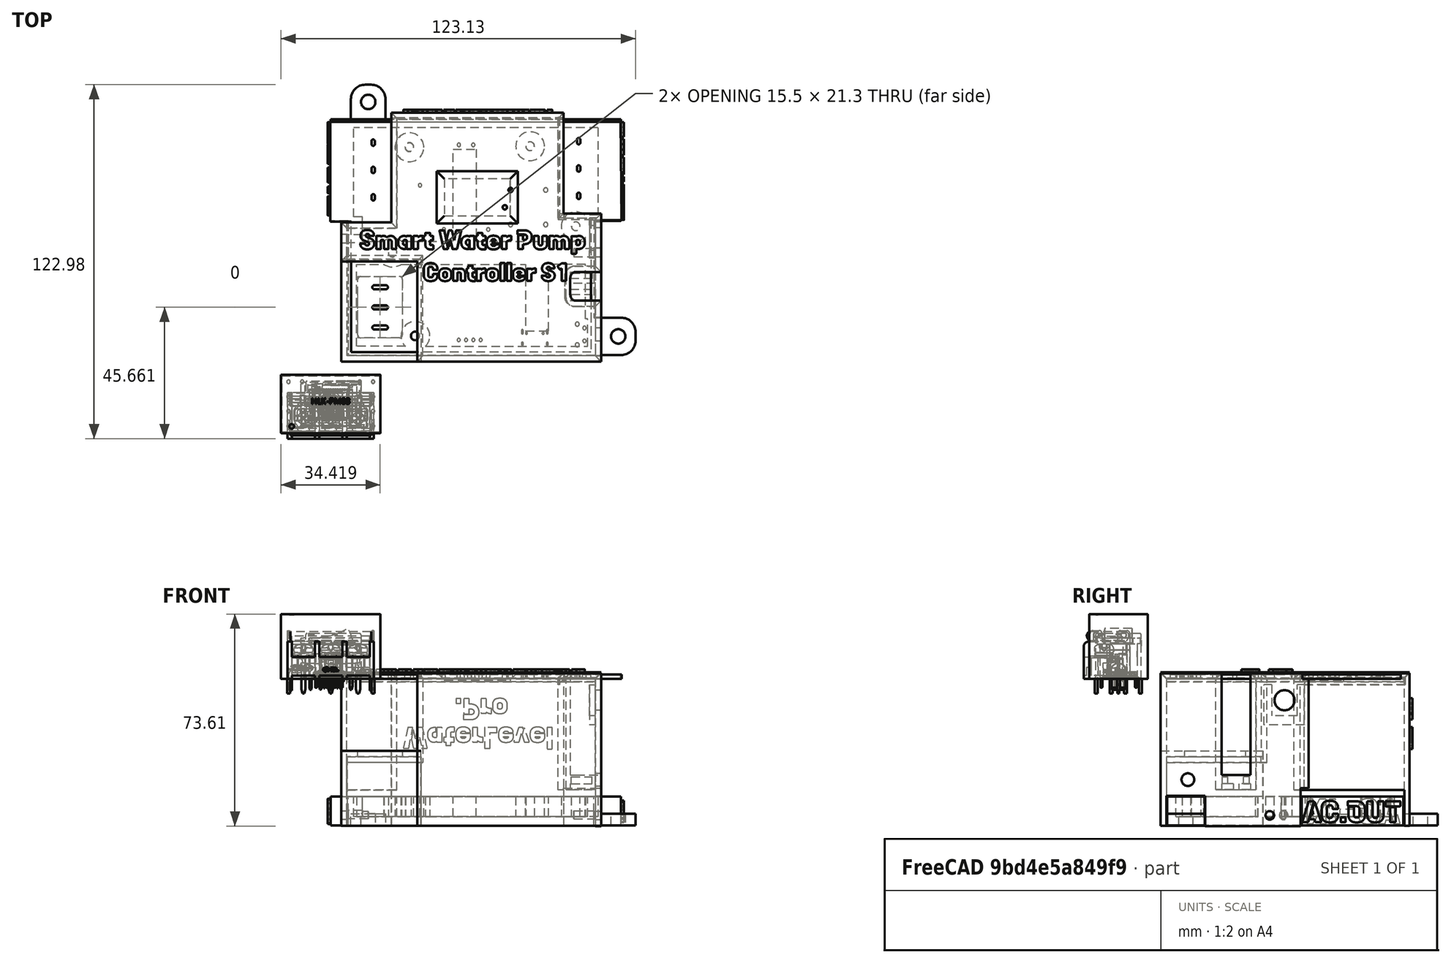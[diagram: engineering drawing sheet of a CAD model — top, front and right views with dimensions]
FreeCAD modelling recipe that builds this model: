
FCSTD DOCUMENT  (FreeCAD 0.21R33771 (Git))
Label: PumpControllerS1_caseV5
License: GPLv3
LicenseURL: https://en.wikipedia.org/wiki/All_rights_reserved
objects: Part::Feature×416, PartDesign::Pad×159, Sketcher::SketchObject×120, PartDesign::Pocket×106, App::Part×69, Part::Part2DObjectPython×20, PartDesign::Fillet×11, PartDesign::Draft×8, PartDesign::Chamfer×8, PartDesign::Body×7, PartDesign::Boolean×3, Part::Cut×1
note: 1151 computed .brp shape members not serialized (recipe doc carries the construction recipe); baked Part::Feature solids carry a one-line shape summary decoded from their .brp

FEATURE [Sketcher::SketchObject] Sketch
  FullyConstrained = true
  MapMode = 5
  Support = -> [XY_Plane049]
  sketch-geometry (8):
    g0: LineSegment StartX=0 StartY=63.64 StartZ=0 EndX=0 EndY=97.92 EndZ=0
    g1: LineSegment StartX=0 StartY=97.92 StartZ=0 EndX=100.82 EndY=97.92 EndZ=0
    g2: LineSegment StartX=100.82 StartY=97.92 StartZ=0 EndX=100.82 EndY=63.64 EndZ=0
    g3: LineSegment StartX=100.82 StartY=63.64 StartZ=0 EndX=90.46 EndY=63.64 EndZ=0
    g4: LineSegment StartX=90.46 StartY=63.64 StartZ=0 EndX=90.46 EndY=17.97 EndZ=0
    g5: LineSegment StartX=90.46 StartY=17.97 StartZ=0 EndX=6.99 EndY=17.97 EndZ=0
    g6: LineSegment StartX=6.99 StartY=17.97 StartZ=0 EndX=6.99 EndY=63.64 EndZ=0
    g7: LineSegment StartX=6.99 StartY=63.64 StartZ=0 EndX=0 EndY=63.64 EndZ=0
  constraints (24):
    c: PointOnObject(g0,g-2)
    c: Coincident(g0,g1)
    c: Horizontal(g1)
    c: Coincident(g1,g2)
    c: Vertical(g2)
    c: Coincident(g2,g3)
    c: Horizontal(g3)
    c: Coincident(g3,g4)
    c: Vertical(g4)
    c: Coincident(g4,g5)
    c: Horizontal(g5)
    c: Coincident(g5,g6)
    c: Vertical(g6)
    c: Coincident(g6,g7)
    c: Coincident(g7,g0)
    c: Horizontal(g7)
    c: DistanceX(g0,g1) = 100.82
    c: DistanceX(g5,g4) = 83.47
    c: DistanceX(g3,g2) = 10.36
    c: DistanceY(g2,g1) = 34.28
    c: DistanceY(g4,g3) = 45.67
    c: DistanceY(g-1,g5) = 17.97
    c: Vertical(g0)
    c: Equal(g0,g2)
FEATURE [PartDesign::Pad] Pad
  Direction = (0,0,1)
  Length = 3
  Length2 = 10
  Profile = -> Sketch
  ReferenceAxis = -> Sketch [N_Axis]
  Refine = true
  Type = 0
FEATURE [Sketcher::SketchObject] Sketch001
  FullyConstrained = true
  MapMode = 5
  Placement = pos=(0,0,3) rot=(0,0,1;0rad)
  Support = -> [Pad]
  sketch-geometry (10):
    g0: Circle CenterX=29.39 CenterY=23.62 CenterZ=0 NormalX=0 NormalY=0 NormalZ=1 AngleXU=0 Radius=5
    g1: Circle CenterX=21.48 CenterY=52.55 CenterZ=0 NormalX=0 NormalY=0 NormalZ=1 AngleXU=0 Radius=5
    g2: Circle CenterX=85.08 CenterY=61.73 CenterZ=0 NormalX=0 NormalY=0 NormalZ=1 AngleXU=0 Radius=5
    g3: Circle CenterX=69.27 CenterY=89.53 CenterZ=0 NormalX=0 NormalY=0 NormalZ=1 AngleXU=0 Radius=5
    g4: Circle CenterX=27.31 CenterY=89.16 CenterZ=0 NormalX=0 NormalY=0 NormalZ=1 AngleXU=0 Radius=5
    g5: Circle CenterX=29.39 CenterY=23.62 CenterZ=0 NormalX=0 NormalY=0 NormalZ=1 AngleXU=0 Radius=1.5
    g6: Circle CenterX=21.48 CenterY=52.55 CenterZ=0 NormalX=0 NormalY=0 NormalZ=1 AngleXU=0 Radius=1.5
    g7: Circle CenterX=27.31 CenterY=89.16 CenterZ=0 NormalX=0 NormalY=0 NormalZ=1 AngleXU=0 Radius=1.5
    g8: Circle CenterX=69.27 CenterY=89.53 CenterZ=0 NormalX=0 NormalY=0 NormalZ=1 AngleXU=0 Radius=1.5
    g9: Circle CenterX=85.08 CenterY=61.73 CenterZ=0 NormalX=0 NormalY=0 NormalZ=1 AngleXU=0 Radius=1.5
  constraints (25):
    c: Diameter(g4) = 10
    c: Diameter(g1) = 10
    c: Diameter(g0) = 10
    c: Diameter(g2) = 10
    c: Diameter(g3) = 10
    c: DistanceX(g4,g3) = 41.96
    c: DistanceX(g1,g4) = 5.83
    c: DistanceX(g3,g2) = 15.81
    c: DistanceX(g1,g0) = 7.91
    c: DistanceX(g-1,g0) = 29.39
    c: DistanceY(g4,g3) = 0.37
    c: DistanceY(g2,g3) = 27.8
    c: DistanceY(g1,g4) = 36.61
    c: DistanceY(g0,g1) = 28.93
    c: DistanceY(g-1,g0) = 23.62
    c: Coincident(g5,g0)
    c: Diameter(g5) = 3
    c: Coincident(g6,g1)
    c: Coincident(g7,g4)
    c: Coincident(g8,g3)
    c: Coincident(g9,g2)
    c: Diameter(g7) = 3
    c: Diameter(g8) = 3
    c: Diameter(g9) = 3
    c: Diameter(g6) = 3
FEATURE [PartDesign::Pad] Pad001
  BaseFeature = -> Pad
  Direction = (0,0,1)
  Length = 7
  Length2 = 10
  Profile = -> Sketch001
  ReferenceAxis = -> Sketch001 [N_Axis]
  Refine = true
  Type = 0
FEATURE [Sketcher::SketchObject] Sketch002
  ExternalGeometry = -> [Pad001]
  FullyConstrained = false
  MapMode = 5
  Placement = pos=(0,0,3) rot=(0,0,1;0rad)
  Support = -> [Pad001]
  sketch-geometry (21):
    g0: LineSegment StartX=90.46 StartY=56.5 StartZ=0 EndX=90.46 EndY=48.4293 EndZ=0
    g1: LineSegment StartX=7 StartY=48.5 StartZ=0 EndX=7 EndY=56.5 EndZ=0
    g2: Circle CenterX=21.48 CenterY=52.55 CenterZ=0 NormalX=0 NormalY=0 NormalZ=1 AngleXU=0 Radius=1.5
    g3: LineSegment StartX=42.46 StartY=56.5 StartZ=0 EndX=42.46 EndY=88.5 EndZ=0
    g4: LineSegment StartX=42.46 StartY=88.5 StartZ=0 EndX=50.46 EndY=88.5 EndZ=0
    g5: LineSegment StartX=50.46 StartY=88.5 StartZ=0 EndX=50.46 EndY=56.5 EndZ=0
    g6: LineSegment StartX=67.69 StartY=48.5 StartZ=0 EndX=67.69 EndY=25.4293 EndZ=0
    g7: LineSegment StartX=67.69 StartY=25.4293 StartZ=0 EndX=75.69 EndY=25.4293 EndZ=0
    g8: LineSegment StartX=75.69 StartY=25.4293 StartZ=0 EndX=75.69 EndY=48.4293 EndZ=0
    g9: LineSegment StartX=8 StartY=97.92 StartZ=0 EndX=0 EndY=97.92 EndZ=0
    g10: LineSegment StartX=0 StartY=97.92 StartZ=0 EndX=0 EndY=63.64 EndZ=0
    g11: LineSegment StartX=0 StartY=63.64 StartZ=0 EndX=8 EndY=63.64 EndZ=0
    g12: LineSegment StartX=8 StartY=63.64 StartZ=0 EndX=8 EndY=97.92 EndZ=0
    g13: LineSegment StartX=100.82 StartY=97.92 StartZ=0 EndX=92.82 EndY=97.92 EndZ=0
    g14: LineSegment StartX=92.82 StartY=97.92 StartZ=0 EndX=92.82 EndY=63.64 EndZ=0
    g15: LineSegment StartX=92.82 StartY=63.64 StartZ=0 EndX=100.82 EndY=63.64 EndZ=0
    g16: LineSegment StartX=100.82 StartY=63.64 StartZ=0 EndX=100.82 EndY=97.92 EndZ=0
    g17: LineSegment StartX=7 StartY=56.5 StartZ=0 EndX=42.46 EndY=56.5 EndZ=0
    g18: LineSegment StartX=7 StartY=48.5 StartZ=0 EndX=67.69 EndY=48.5 EndZ=0
    g19: LineSegment StartX=50.46 StartY=56.5 StartZ=0 EndX=90.46 EndY=56.5 EndZ=0
    g20: LineSegment StartX=90.46 StartY=48.4293 StartZ=0 EndX=75.69 EndY=48.4293 EndZ=0
  constraints (58):
    c: Vertical(g0)
    c: Vertical(g1)
    c: DistanceY(g1,g1) = 8
    c: DistanceY(g-1,g1) = 48.5
    c: Coincident(g2,g-3)
    c: Diameter(g2) = 3
    c: Coincident(g3,g4)
    c: Coincident(g4,g5)
    c: Horizontal(g4)
    c: Vertical(g3)
    c: Vertical(g5)
    c: Coincident(g6,g7)
    c: Coincident(g7,g8)
    c: Horizontal(g7)
    c: Vertical(g6)
    c: Vertical(g8)
    c: DistanceX(g4,g4) = 8
    c: DistanceX(g7,g7) = 8
    c: Coincident(g9,g10)
    c: Coincident(g10,g11)
    c: Coincident(g11,g12)
    c: Coincident(g12,g9)
    c: Horizontal(g9)
    c: Horizontal(g11)
    c: Vertical(g10)
    c: Vertical(g12)
    c: PointOnObject(g9,g-4)
    c: Coincident(g10,g-8)
    c: Coincident(g13,g14)
    c: Coincident(g14,g15)
    c: Coincident(g15,g16)
    c: Coincident(g16,g13)
    c: Horizontal(g13)
    c: Horizontal(g15)
    c: Vertical(g14)
    c: Vertical(g16)
    c: Coincident(g13,g-7)
    c: PointOnObject(g14,g-6)
    c: DistanceX(g13,g13) = 8
    c: DistanceX(g9,g9) = 8
    c: DistanceY(g8,g8) = 23
    c: DistanceY(g5,g5) = 32
    c: DistanceX(g5,g0) = 40
    c: DistanceX(g-1,g1) = 7
    c: DistanceX(g1,g0) = 83.46
    c: DistanceX(g8,g0) = 14.77
    c: Coincident(g1,g17)
    c: Coincident(g17,g3)
    c: Horizontal(g17)
    c: Coincident(g1,g18)
    c: Coincident(g18,g6)
    c: Horizontal(g18)
    c: Coincident(g5,g19)
    c: Coincident(g19,g0)
    c: Horizontal(g19)
    c: Coincident(g0,g20)
    c: Coincident(g20,g8)
    c: Horizontal(g20)
FEATURE [PartDesign::Pad] Pad002
  BaseFeature = -> Pad001
  Direction = (0,0,1)
  Length = 7
  Length2 = 10
  Profile = -> Sketch002
  ReferenceAxis = -> Sketch002 [N_Axis]
  Refine = true
  Type = 0
FEATURE [Sketcher::SketchObject] Sketch003
  ExternalGeometry = -> [Pad002]
  FullyConstrained = true
  MapMode = 5
  Placement = pos=(0,0,3) rot=(0,0,1;0rad)
  Support = -> [Pad002]
  sketch-geometry (20):
    g0: LineSegment StartX=5 StartY=97.92 StartZ=0 EndX=94 EndY=97.92 EndZ=0
    g1: LineSegment StartX=94 StartY=97.92 StartZ=0 EndX=94 EndY=95.92 EndZ=0
    g2: LineSegment StartX=94 StartY=95.92 StartZ=0 EndX=5 EndY=95.92 EndZ=0
    g3: LineSegment StartX=5 StartY=95.92 StartZ=0 EndX=5 EndY=97.92 EndZ=0
    g4: LineSegment StartX=6.99 StartY=17.97 StartZ=0 EndX=8.99 EndY=17.97 EndZ=0
    g5: LineSegment StartX=8.99 StartY=17.97 StartZ=0 EndX=8.99 EndY=64.97 EndZ=0
    g6: LineSegment StartX=8.99 StartY=64.97 StartZ=0 EndX=6.99 EndY=64.97 EndZ=0
    g7: LineSegment StartX=6.99 StartY=64.97 StartZ=0 EndX=6.99 EndY=17.97 EndZ=0
    g8: LineSegment StartX=90.46 StartY=29.6 StartZ=0 EndX=88.46 EndY=29.6 EndZ=0
    g9: LineSegment StartX=88.46 StartY=29.6 StartZ=0 EndX=88.46 EndY=64.6 EndZ=0
    g10: LineSegment StartX=88.46 StartY=64.6 StartZ=0 EndX=90.46 EndY=64.6 EndZ=0
    g11: LineSegment StartX=90.46 StartY=64.6 StartZ=0 EndX=90.46 EndY=29.6 EndZ=0
    g12: LineSegment StartX=90.46 StartY=17.97 StartZ=0 EndX=89.21 EndY=17.97 EndZ=0
    g13: LineSegment StartX=89.21 StartY=17.97 StartZ=0 EndX=89.21 EndY=26.97 EndZ=0
    g14: LineSegment StartX=89.21 StartY=26.97 StartZ=0 EndX=90.46 EndY=26.97 EndZ=0
    g15: LineSegment StartX=90.46 StartY=26.97 StartZ=0 EndX=90.46 EndY=17.97 EndZ=0
    g16: LineSegment StartX=35.93 StartY=17.97 StartZ=0 EndX=75.93 EndY=17.97 EndZ=0
    g17: LineSegment StartX=75.93 StartY=17.97 StartZ=0 EndX=75.93 EndY=19.97 EndZ=0
    g18: LineSegment StartX=75.93 StartY=19.97 StartZ=0 EndX=35.93 EndY=19.97 EndZ=0
    g19: LineSegment StartX=35.93 StartY=19.97 StartZ=0 EndX=35.93 EndY=17.97 EndZ=0
  constraints (58):
    c: Coincident(g0,g1)
    c: Coincident(g1,g2)
    c: Coincident(g2,g3)
    c: Coincident(g3,g0)
    c: Horizontal(g0)
    c: Horizontal(g2)
    c: Vertical(g1)
    c: Vertical(g3)
    c: PointOnObject(g0,g-3)
    c: DistanceY(g1,g1) = 2
    c: DistanceX(g-1,g0) = 5
    c: DistanceX(g0,g0) = 89
    c: Coincident(g4,g5)
    c: Coincident(g5,g6)
    c: Coincident(g6,g7)
    c: Coincident(g7,g4)
    c: Horizontal(g4)
    c: Horizontal(g6)
    c: Vertical(g5)
    c: Vertical(g7)
    c: Coincident(g4,g-7)
    c: DistanceY(g5,g5) = 47
    c: DistanceX(g6,g5) = 2
    c: Coincident(g8,g9)
    c: Coincident(g9,g10)
    c: Coincident(g10,g11)
    c: Coincident(g11,g8)
    c: Horizontal(g8)
    c: Horizontal(g10)
    c: Vertical(g9)
    c: Vertical(g11)
    c: PointOnObject(g8,g-8)
    c: DistanceX(g9,g10) = 2
    c: DistanceY(g9,g9) = 35
    c: DistanceY(g-8,g8) = 11.63
    c: Coincident(g12,g13)
    c: Coincident(g13,g14)
    c: Coincident(g14,g15)
    c: Coincident(g15,g12)
    c: Horizontal(g12)
    c: Horizontal(g14)
    c: Vertical(g13)
    c: Vertical(g15)
    c: Coincident(g12,g-8)
    c: DistanceX(g14,g14) = 1.25
    c: DistanceY(g13,g13) = 9
    c: Coincident(g16,g17)
    c: Coincident(g17,g18)
    c: Coincident(g18,g19)
    c: Coincident(g19,g16)
    c: Horizontal(g16)
    c: Horizontal(g18)
    c: Vertical(g17)
    c: Vertical(g19)
    c: PointOnObject(g16,g-7)
    c: DistanceY(g17,g17) = 2
    c: DistanceX(g18,g18) = 40
    c: DistanceX(g-1,g16) = 35.93
FEATURE [PartDesign::Pad] Pad003
  BaseFeature = -> Pad002
  Direction = (0,0,1)
  Length = 7
  Length2 = 10
  Profile = -> Sketch003
  ReferenceAxis = -> Sketch003 [N_Axis]
  Refine = true
  Type = 0
FEATURE [PartDesign::Pad] Pad004
  BaseFeature = -> Pad003
  Direction = (0,1,0)
  Length = 4
  Length2 = 10
  Profile = -> Pad003 [Face33]
  Refine = true
  Type = 0
FEATURE [PartDesign::Pad] Pad005
  BaseFeature = -> Pad004
  Direction = (1,0,0)
  Length = 14
  Length2 = 10
  Profile = -> Pad004 [Face13]
  Refine = true
  Type = 0
FEATURE [PartDesign::Pad] Pad006
  BaseFeature = -> Pad005
  Direction = (-1,0,0)
  Length = 28
  Length2 = 10
  Profile = -> Pad005 [Face36]
  Refine = true
  Type = 0
FEATURE [Sketcher::SketchObject] Sketch004
  ExternalGeometry = -> [Pad006]
  FullyConstrained = true
  MapMode = 5
  Placement = pos=(92.82,0,0) rot=(0.57735,-0.57735,-0.57735;2.0944rad)
  Support = -> [Pad006]
  sketch-geometry (4):
    g0: LineSegment StartX=-63.64 StartY=3 StartZ=0 EndX=-65.64 EndY=3 EndZ=0
    g1: LineSegment StartX=-65.64 StartY=3 StartZ=0 EndX=-65.64 EndY=10 EndZ=0
    g2: LineSegment StartX=-65.64 StartY=10 StartZ=0 EndX=-63.64 EndY=10 EndZ=0
    g3: LineSegment StartX=-63.64 StartY=10 StartZ=0 EndX=-63.64 EndY=3 EndZ=0
  constraints (11):
    c: Coincident(g0,g1)
    c: Coincident(g1,g2)
    c: Coincident(g2,g3)
    c: Coincident(g3,g0)
    c: Horizontal(g0)
    c: Horizontal(g2)
    c: Vertical(g1)
    c: Vertical(g3)
    c: Coincident(g0,g-5)
    c: PointOnObject(g1,g-4)
    c: DistanceX(g1,g2) = 2
FEATURE [PartDesign::Pad] Pad007
  BaseFeature = -> Pad006
  Direction = (-1,0,0)
  Length = 10
  Length2 = 10
  Profile = -> Sketch004
  ReferenceAxis = -> Sketch004 [N_Axis]
  Refine = true
  Type = 0
FEATURE [Sketcher::SketchObject] Sketch005
  ExternalGeometry = -> [Pad007]
  FullyConstrained = true
  MapMode = 5
  Placement = pos=(90.46,0,0) rot=(0.57735,0.57735,0.57735;2.0944rad)
  Support = -> [Pad007]
  sketch-geometry (4):
    g0: LineSegment StartX=17.97 StartY=10 StartZ=0 EndX=29.97 EndY=10 EndZ=0
    g1: LineSegment StartX=29.97 StartY=10 StartZ=0 EndX=29.97 EndY=0 EndZ=0
    g2: LineSegment StartX=29.97 StartY=0 StartZ=0 EndX=17.97 EndY=0 EndZ=0
    g3: LineSegment StartX=17.97 StartY=0 StartZ=0 EndX=17.97 EndY=10 EndZ=0
  constraints (11):
    c: Coincident(g0,g1)
    c: Coincident(g1,g2)
    c: Coincident(g2,g3)
    c: Coincident(g3,g0)
    c: Horizontal(g0)
    c: Horizontal(g2)
    c: Vertical(g1)
    c: Vertical(g3)
    c: Coincident(g0,g-4)
    c: PointOnObject(g1,g-5)
    c: DistanceX(g0,g0) = 12
FEATURE [PartDesign::Pad] Pad008
  BaseFeature = -> Pad007
  Direction = (1,0,0)
  Length = 1.5
  Length2 = 10
  Profile = -> Sketch005
  ReferenceAxis = -> Sketch005 [N_Axis]
  Refine = true
  Type = 0
FEATURE [Sketcher::SketchObject] Sketch006
  ExternalGeometry = -> [Pad008]
  FullyConstrained = true
  MapMode = 5
  Placement = pos=(0,0,10) rot=(0,0,1;0rad)
  Support = -> [Pad008]
  sketch-geometry (4):
    g0: LineSegment StartX=90.46 StartY=29.97 StartZ=0 EndX=91.96 EndY=29.97 EndZ=0
    g1: LineSegment StartX=91.96 StartY=29.97 StartZ=0 EndX=91.96 EndY=17.97 EndZ=0
    g2: LineSegment StartX=91.96 StartY=17.97 StartZ=0 EndX=90.46 EndY=17.97 EndZ=0
    g3: LineSegment StartX=90.46 StartY=17.97 StartZ=0 EndX=90.46 EndY=29.97 EndZ=0
  constraints (10):
    c: Coincident(g0,g1)
    c: Coincident(g1,g2)
    c: Coincident(g2,g3)
    c: Coincident(g3,g0)
    c: Horizontal(g0)
    c: Horizontal(g2)
    c: Vertical(g1)
    c: Vertical(g3)
    c: Coincident(g0,g-3)
    c: Coincident(g1,g-5)
FEATURE [PartDesign::Pad] Pad009
  BaseFeature = -> Pad008
  Direction = (0,0,1)
  Length = 12
  Length2 = 10
  Profile = -> Sketch006
  ReferenceAxis = -> Sketch006 [N_Axis]
  Refine = true
  Type = 0
FEATURE [Sketcher::SketchObject] Sketch007
  FullyConstrained = false
  MapMode = 5
  Placement = pos=(91.96,0,0) rot=(0.57735,0.57735,0.57735;2.0944rad)
  Support = -> [Pad009]
  sketch-geometry (1):
    g0: Circle CenterX=24.1415 CenterY=15.9066 CenterZ=0 NormalX=0 NormalY=0 NormalZ=1 AngleXU=0 Radius=2.2
  constraints (1):
    c: Diameter(g0) = 4.4
FEATURE [PartDesign::Pocket] Pocket
  BaseFeature = -> Pad009
  Direction = (-1,0,0)
  Length = 5
  Length2 = 5
  Profile = -> Sketch007
  ReferenceAxis = -> Sketch007 [N_Axis]
  Refine = true
  Type = 0
FEATURE [PartDesign::Pad] Pad010
  BaseFeature = -> Pocket
  Direction = (0,1,0)
  Length = 1
  Length2 = 10
  Profile = -> Pocket [Face4]
  Refine = true
  Type = 0
FEATURE [PartDesign::Pad] Pad011
  BaseFeature = -> Pad010
  Direction = (0,-1,0)
  Length = 1
  Length2 = 10
  Profile = -> Pad010 [Face5]
  Refine = true
  Type = 0
FEATURE [PartDesign::Pad] Pad012
  BaseFeature = -> Pad011
  Direction = (-1,0,0)
  Length = 1
  Length2 = 10
  Profile = -> Pad011 [Face59]
  Refine = true
  Type = 0
FEATURE [PartDesign::Pad] Pad013
  BaseFeature = -> Pad012
  Direction = (1,0,0)
  Length = 1
  Length2 = 10
  Profile = -> Pad012 [Face5]
  Refine = true
  Type = 0
FEATURE [Sketcher::SketchObject] Sketch008
  FullyConstrained = true
  MapMode = 5
  Support = -> [XY_Plane050]
  sketch-geometry (10):
    g0: LineSegment StartX=21 StartY=100.55 StartZ=0 EndX=21 EndY=64.55 EndZ=0
    g1: LineSegment StartX=21 StartY=64.55 StartZ=0 EndX=4.2 EndY=64.55 EndZ=0
    g2: LineSegment StartX=93.5 StartY=15.2 StartZ=0 EndX=93.5 EndY=65.2 EndZ=0
    g3: LineSegment StartX=93.5 StartY=65.2 StartZ=0 EndX=80.9 EndY=65.2 EndZ=0
    g4: LineSegment StartX=80.9 StartY=65.2 StartZ=0 EndX=80.9 EndY=100.55 EndZ=0
    g5: LineSegment StartX=80.9 StartY=100.55 StartZ=0 EndX=21 EndY=100.55 EndZ=0
    g6: LineSegment StartX=93.5 StartY=15.2 StartZ=0 EndX=30 EndY=15.2 EndZ=0
    g7: LineSegment StartX=30 StartY=15.2 StartZ=0 EndX=30 EndY=49.55 EndZ=0
    g8: LineSegment StartX=30 StartY=49.55 StartZ=0 EndX=4.2 EndY=49.55 EndZ=0
    g9: LineSegment StartX=4.2 StartY=49.55 StartZ=0 EndX=4.2 EndY=64.55 EndZ=0
  constraints (30):
    c: Vertical(g0)
    c: Coincident(g0,g1)
    c: Horizontal(g1)
    c: Vertical(g2)
    c: Coincident(g2,g3)
    c: Coincident(g3,g4)
    c: Vertical(g4)
    c: Coincident(g4,g5)
    c: Coincident(g5,g0)
    c: Horizontal(g5)
    c: Horizontal(g3)
    c: Coincident(g2,g6)
    c: Horizontal(g6)
    c: Coincident(g6,g7)
    c: Vertical(g7)
    c: Coincident(g7,g8)
    c: Horizontal(g8)
    c: Coincident(g8,g9)
    c: Coincident(g9,g1)
    c: Vertical(g9)
    c: DistanceY(g-1,g6) = 15.2
    c: DistanceX(g-1,g6) = 30
    c: DistanceX(g8,g7) = 25.8
    c: DistanceX(g6,g6) = 63.5
    c: DistanceY(g2,g2) = 50
    c: DistanceY(g7,g7) = 34.35
    c: DistanceY(g9,g9) = 15
    c: DistanceY(g0,g0) = 36
    c: DistanceX(g5,g5) = 59.9
    c: DistanceX(g3,g3) = 12.6
FEATURE [PartDesign::Pad] Pad014
  Direction = (0,0,1)
  Length = 2
  Length2 = 10
  Profile = -> Sketch008
  ReferenceAxis = -> Sketch008 [N_Axis]
  Refine = true
  Type = 0
FEATURE [Sketcher::SketchObject] Sketch009
  FullyConstrained = false
  MapMode = 5
  Support = -> [XY_Plane051]
  sketch-geometry (4):
    g0: LineSegment StartX=4.34912 StartY=50.7797 StartZ=0 EndX=32.5138 EndY=50.7797 EndZ=0
    g1: LineSegment StartX=32.5138 StartY=50.7797 StartZ=0 EndX=32.5138 EndY=14.7356 EndZ=0
    g2: LineSegment StartX=32.5138 StartY=14.7356 StartZ=0 EndX=4.34912 EndY=14.7356 EndZ=0
    g3: LineSegment StartX=4.34912 StartY=14.7356 StartZ=0 EndX=4.34912 EndY=50.7797 EndZ=0
  constraints (8):
    c: Coincident(g0,g1)
    c: Coincident(g1,g2)
    c: Coincident(g2,g3)
    c: Coincident(g3,g0)
    c: Horizontal(g0)
    c: Horizontal(g2)
    c: Vertical(g1)
    c: Vertical(g3)
FEATURE [PartDesign::Pad] Pad015
  Direction = (0,0,1)
  Length = 2
  Length2 = 10
  Profile = -> Sketch009
  ReferenceAxis = -> Sketch009 [N_Axis]
  Refine = true
  Type = 0
FEATURE [Sketcher::SketchObject] Sketch010
  ExternalGeometry = -> [Pad015]
  FullyConstrained = true
  MapMode = 5
  Placement = pos=(0,0,0) rot=(1,0,0;3.14159rad)
  Support = -> [Pad015]
  sketch-geometry (6):
    g0: LineSegment StartX=4.34912 StartY=-50.7797 StartZ=0 EndX=4.34912 EndY=-14.7356 EndZ=0
    g1: LineSegment StartX=4.34912 StartY=-14.7356 StartZ=0 EndX=32.5138 EndY=-14.7356 EndZ=0
    g2: LineSegment StartX=32.5138 StartY=-14.7356 StartZ=0 EndX=32.5138 EndY=-16.2356 EndZ=0
    g3: LineSegment StartX=32.5138 StartY=-16.2356 StartZ=0 EndX=5.84912 EndY=-16.2356 EndZ=0
    g4: LineSegment StartX=5.84912 StartY=-16.2356 StartZ=0 EndX=5.84912 EndY=-50.7797 EndZ=0
    g5: LineSegment StartX=5.84912 StartY=-50.7797 StartZ=0 EndX=4.34912 EndY=-50.7797 EndZ=0
  constraints (15):
    c: Coincident(g-3,g0)
    c: Coincident(g0,g-4)
    c: Coincident(g0,g1)
    c: Coincident(g1,g-4)
    c: Coincident(g1,g2)
    c: Vertical(g2)
    c: Coincident(g2,g3)
    c: Horizontal(g3)
    c: Coincident(g3,g4)
    c: Vertical(g4)
    c: Coincident(g4,g5)
    c: Coincident(g5,g0)
    c: DistanceY(g2,g1) = 1.5
    c: DistanceX(g0,g4) = 1.5
    c: PointOnObject(g4,g-5)
FEATURE [PartDesign::Pad] Pad016
  BaseFeature = -> Pad015
  Direction = (0,0,-1)
  Length = 22
  Length2 = 10
  Profile = -> Sketch010
  ReferenceAxis = -> Sketch010 [N_Axis]
  Refine = true
  Type = 0
FEATURE [Sketcher::SketchObject] Sketch011
  ExternalGeometry = -> [Pad016]
  FullyConstrained = true
  MapMode = 5
  Placement = pos=(0,0,2) rot=(0,0,1;0rad)
  Support = -> [Pad016]
  sketch-geometry (4):
    g0: LineSegment StartX=9.59912 StartY=43.7856 StartZ=0 EndX=25.0991 EndY=43.7856 EndZ=0
    g1: LineSegment StartX=25.0991 StartY=43.7856 StartZ=0 EndX=25.0991 EndY=22.4856 EndZ=0
    g2: LineSegment StartX=25.0991 StartY=22.4856 StartZ=0 EndX=9.59912 EndY=22.4856 EndZ=0
    g3: LineSegment StartX=9.59912 StartY=22.4856 StartZ=0 EndX=9.59912 EndY=43.7856 EndZ=0
  constraints (12):
    c: Coincident(g0,g1)
    c: Coincident(g1,g2)
    c: Coincident(g2,g3)
    c: Coincident(g3,g0)
    c: Horizontal(g0)
    c: Horizontal(g2)
    c: Vertical(g1)
    c: Vertical(g3)
    c: DistanceX(g0,g0) = 15.5
    c: DistanceY(g1,g0) = 21.3
    c: DistanceY(g-4,g2) = 7.75
    c: DistanceX(g-4,g2) = 5.25
FEATURE [PartDesign::Pocket] Pocket001
  BaseFeature = -> Pad016
  Direction = (0,0,-1)
  Length = 5
  Length2 = 5
  Profile = -> Sketch011
  ReferenceAxis = -> Sketch011 [N_Axis]
  Refine = true
  Type = 0
FEATURE [Sketcher::SketchObject] Sketch012
  ExternalGeometry = -> [Pad014]
  FullyConstrained = true
  MapMode = 5
  Placement = pos=(0,0,0) rot=(1,0,0;3.14159rad)
  Support = -> [Pad014]
  sketch-geometry (8):
    g0: LineSegment StartX=30 StartY=-15.2 StartZ=0 EndX=93.5 EndY=-15.2 EndZ=0
    g1: LineSegment StartX=93.5 StartY=-15.2 StartZ=0 EndX=93.5 EndY=-16.7 EndZ=0
    g2: LineSegment StartX=93.5 StartY=-16.7 StartZ=0 EndX=30 EndY=-16.7 EndZ=0
    g3: LineSegment StartX=30 StartY=-16.7 StartZ=0 EndX=30 EndY=-15.2 EndZ=0
    g4: LineSegment StartX=21 StartY=-100.55 StartZ=0 EndX=80.9 EndY=-100.55 EndZ=0
    g5: LineSegment StartX=80.9 StartY=-100.55 StartZ=0 EndX=80.9 EndY=-99.35 EndZ=0
    g6: LineSegment StartX=80.9 StartY=-99.35 StartZ=0 EndX=21 EndY=-99.35 EndZ=0
    g7: LineSegment StartX=21 StartY=-99.35 StartZ=0 EndX=21 EndY=-100.55 EndZ=0
  constraints (22):
    c: Coincident(g0,g1)
    c: Coincident(g1,g2)
    c: Coincident(g2,g3)
    c: Coincident(g3,g0)
    c: Horizontal(g0)
    c: Horizontal(g2)
    c: Vertical(g1)
    c: Vertical(g3)
    c: Coincident(g0,g-4)
    c: PointOnObject(g1,g-5)
    c: DistanceY(g1,g1) = 1.5
    c: Coincident(g4,g5)
    c: Coincident(g5,g6)
    c: Coincident(g6,g7)
    c: Coincident(g7,g4)
    c: Horizontal(g4)
    c: Horizontal(g6)
    c: Vertical(g5)
    c: Vertical(g7)
    c: Coincident(g4,g-10)
    c: DistanceY(g5,g5) = 1.2
    c: PointOnObject(g5,g-11)
FEATURE [PartDesign::Pad] Pad017
  BaseFeature = -> Pad014
  Direction = (0,0,-1)
  Length = 51
  Length2 = 10
  Profile = -> Sketch012
  ReferenceAxis = -> Sketch012 [N_Axis]
  Refine = true
  Type = 0
FEATURE [PartDesign::Pad] Pad018
  BaseFeature = -> Pad017
  Direction = (0,1,0)
  Length = 0.6
  Length2 = 10
  Profile = -> Pad017 [Face16]
  Refine = true
  Type = 0
FEATURE [PartDesign::Pad] Pad019
  BaseFeature = -> Pad018
  Direction = (0,-1,0)
  Length = 0.5
  Length2 = 10
  Profile = -> Pad018 [Face4]
  Refine = true
  Type = 0
FEATURE [PartDesign::Pad] Pad020
  BaseFeature = -> Pocket001
  Direction = (0,-1,0)
  Length = 0.5
  Length2 = 10
  Profile = -> Pocket001 [Face5]
  Refine = true
  Type = 0
FEATURE [PartDesign::Pad] Pad021
  BaseFeature = -> Pad020
  Direction = (-1,0,0)
  Length = 0.5
  Length2 = 10
  Profile = -> Pad020 [Face11]
  Refine = true
  Type = 0
FEATURE [Sketcher::SketchObject] Sketch013
  ExternalGeometry = -> [Pad019]
  FullyConstrained = true
  MapMode = 5
  Placement = pos=(0,0,0) rot=(1,0,0;3.14159rad)
  Support = -> [Pad019]
  sketch-geometry (6):
    g0: LineSegment StartX=30 StartY=-16.7 StartZ=0 EndX=32 EndY=-16.7 EndZ=0
    g1: LineSegment StartX=32 StartY=-16.7 StartZ=0 EndX=32 EndY=-51.55 EndZ=0
    g2: LineSegment StartX=32 StartY=-51.55 StartZ=0 EndX=4.2 EndY=-51.55 EndZ=0
    g3: LineSegment StartX=4.2 StartY=-51.55 StartZ=0 EndX=4.2 EndY=-49.55 EndZ=0
    g4: LineSegment StartX=4.2 StartY=-49.55 StartZ=0 EndX=30 EndY=-49.55 EndZ=0
    g5: LineSegment StartX=30 StartY=-49.55 StartZ=0 EndX=30 EndY=-16.7 EndZ=0
  constraints (15):
    c: Coincident(g-4,g0)
    c: PointOnObject(g0,g-4)
    c: Coincident(g0,g1)
    c: Vertical(g1)
    c: Coincident(g1,g2)
    c: Horizontal(g2)
    c: Coincident(g2,g3)
    c: Coincident(g3,g-5)
    c: Coincident(g3,g4)
    c: Coincident(g4,g-5)
    c: Coincident(g4,g5)
    c: Coincident(g5,g0)
    c: Vertical(g3)
    c: DistanceY(g3,g3) = 2
    c: DistanceX(g0,g0) = 2
FEATURE [PartDesign::Pad] Pad022
  BaseFeature = -> Pad019
  Direction = (0,0,-1)
  Length = 29
  Length2 = 10
  Profile = -> Sketch013
  ReferenceAxis = -> Sketch013 [N_Axis]
  Refine = true
  Type = 0
FEATURE [Sketcher::SketchObject] Sketch014
  ExternalGeometry = -> [Pad022]
  FullyConstrained = true
  MapMode = 5
  Placement = pos=(0,0,0) rot=(1,0,0;3.14159rad)
  Support = -> [Pad022]
  sketch-geometry (4):
    g0: LineSegment StartX=4.2 StartY=-64.55 StartZ=0 EndX=6.2 EndY=-64.55 EndZ=0
    g1: LineSegment StartX=6.2 StartY=-64.55 StartZ=0 EndX=6.2 EndY=-51.55 EndZ=0
    g2: LineSegment StartX=6.2 StartY=-51.55 StartZ=0 EndX=4.2 EndY=-51.55 EndZ=0
    g3: LineSegment StartX=4.2 StartY=-51.55 StartZ=0 EndX=4.2 EndY=-64.55 EndZ=0
  constraints (11):
    c: Coincident(g0,g1)
    c: Coincident(g1,g2)
    c: Coincident(g2,g3)
    c: Coincident(g3,g0)
    c: Horizontal(g0)
    c: Horizontal(g2)
    c: Vertical(g1)
    c: Vertical(g3)
    c: Coincident(g0,g-4)
    c: PointOnObject(g1,g-5)
    c: DistanceX(g2,g2) = 2
FEATURE [PartDesign::Pad] Pad023
  BaseFeature = -> Pad022
  Direction = (0,0,-1)
  Length = 51
  Length2 = 10
  Profile = -> Sketch014
  ReferenceAxis = -> Sketch014 [N_Axis]
  Refine = true
  Type = 0
FEATURE [PartDesign::Pocket] Pocket002
  BaseFeature = -> Pad023
  Direction = (0,-1,0)
  Length = 1.5
  Length2 = 5
  Profile = -> Pad023 [Face21]
  Refine = true
  Type = 0
FEATURE [PartDesign::Pad] Pad024
  BaseFeature = -> Pocket002
  Direction = (-1,0,0)
  Length = 0.55
  Length2 = 10
  Profile = -> Pocket002 [Face18]
  Refine = true
  Type = 0
FEATURE [PartDesign::Pad] Pad025
  BaseFeature = -> Pad024
  Direction = (0,-1,0)
  Length = 1
  Length2 = 10
  Profile = -> Pad024 [Face19]
  Refine = true
  Type = 0
FEATURE [Sketcher::SketchObject] Sketch015
  ExternalGeometry = -> [Pad025]
  FullyConstrained = true
  MapMode = 5
  Placement = pos=(0,0,0) rot=(1,0,0;3.14159rad)
  Support = -> [Pad025]
  sketch-geometry (6):
    g0: LineSegment StartX=6.2 StartY=-63.05 StartZ=0 EndX=21 EndY=-63.05 EndZ=0
    g1: LineSegment StartX=21 StartY=-63.05 StartZ=0 EndX=21 EndY=-99.35 EndZ=0
    g2: LineSegment StartX=21 StartY=-99.35 StartZ=0 EndX=23 EndY=-99.35 EndZ=0
    g3: LineSegment StartX=23 StartY=-99.35 StartZ=0 EndX=23 EndY=-61.05 EndZ=0
    g4: LineSegment StartX=23 StartY=-61.05 StartZ=0 EndX=6.2 EndY=-61.05 EndZ=0
    g5: LineSegment StartX=6.2 StartY=-61.05 StartZ=0 EndX=6.2 EndY=-63.05 EndZ=0
  constraints (15):
    c: Coincident(g-4,g0)
    c: Coincident(g0,g-4)
    c: Coincident(g0,g1)
    c: Coincident(g1,g-3)
    c: Coincident(g1,g2)
    c: Horizontal(g2)
    c: Coincident(g2,g3)
    c: Vertical(g3)
    c: Coincident(g3,g4)
    c: Horizontal(g4)
    c: Coincident(g4,g5)
    c: Coincident(g5,g0)
    c: Vertical(g5)
    c: DistanceX(g2,g2) = 2
    c: DistanceY(g5,g5) = 2
FEATURE [PartDesign::Pad] Pad026
  BaseFeature = -> Pad025
  Direction = (0,0,-1)
  Length = 38.6
  Length2 = 10
  Profile = -> Sketch015
  ReferenceAxis = -> Sketch015 [N_Axis]
  Refine = true
  Type = 0
FEATURE [Sketcher::SketchObject] Sketch016
  ExternalGeometry = -> [Pad026]
  FullyConstrained = true
  MapMode = 5
  Placement = pos=(0,0,0) rot=(1,0,0;3.14159rad)
  Support = -> [Pad026]
  sketch-geometry (4):
    g0: LineSegment StartX=93.5 StartY=-65.2 StartZ=0 EndX=91.5 EndY=-65.2 EndZ=0
    g1: LineSegment StartX=91.5 StartY=-65.2 StartZ=0 EndX=91.5 EndY=-16.7 EndZ=0
    g2: LineSegment StartX=91.5 StartY=-16.7 StartZ=0 EndX=93.5 EndY=-16.7 EndZ=0
    g3: LineSegment StartX=93.5 StartY=-16.7 StartZ=0 EndX=93.5 EndY=-65.2 EndZ=0
  constraints (11):
    c: Coincident(g0,g1)
    c: Coincident(g1,g2)
    c: Coincident(g2,g3)
    c: Coincident(g3,g0)
    c: Horizontal(g0)
    c: Horizontal(g2)
    c: Vertical(g1)
    c: Vertical(g3)
    c: Coincident(g0,g-5)
    c: PointOnObject(g1,g-4)
    c: DistanceX(g0,g0) = 2
FEATURE [PartDesign::Pad] Pad027
  BaseFeature = -> Pad026
  Direction = (0,0,-1)
  Length = 28.7
  Length2 = 10
  Profile = -> Sketch016
  ReferenceAxis = -> Sketch016 [N_Axis]
  Refine = true
  Type = 0
FEATURE [Sketcher::SketchObject] Sketch017
  ExternalGeometry = -> [Pad027]
  FullyConstrained = true
  MapMode = 5
  Placement = pos=(0,0,-28.7) rot=(1,0,0;3.14159rad)
  Support = -> [Pad027]
  sketch-geometry (4):
    g0: LineSegment StartX=91.5 StartY=-65.2 StartZ=0 EndX=93.5 EndY=-65.2 EndZ=0
    g1: LineSegment StartX=93.5 StartY=-65.2 StartZ=0 EndX=93.5 EndY=-30.4 EndZ=0
    g2: LineSegment StartX=93.5 StartY=-30.4 StartZ=0 EndX=91.5 EndY=-30.4 EndZ=0
    g3: LineSegment StartX=91.5 StartY=-30.4 StartZ=0 EndX=91.5 EndY=-65.2 EndZ=0
  constraints (11):
    c: Coincident(g0,g1)
    c: Coincident(g1,g2)
    c: Coincident(g2,g3)
    c: Coincident(g3,g0)
    c: Horizontal(g0)
    c: Horizontal(g2)
    c: Vertical(g1)
    c: Vertical(g3)
    c: Coincident(g0,g-5)
    c: PointOnObject(g1,g-3)
    c: DistanceY(g1,g1) = 34.8
FEATURE [PartDesign::Pad] Pad028
  BaseFeature = -> Pad027
  Direction = (0,0,-1)
  Length = 22.4
  Length2 = 10
  Profile = -> Sketch017
  ReferenceAxis = -> Sketch017 [N_Axis]
  Refine = true
  Type = 0
FEATURE [PartDesign::Pocket] Pocket003
  BaseFeature = -> Pad028
  Direction = (0,-1,0)
  Length = 1.9
  Length2 = 5
  Profile = -> Pad028 [Face27]
  Refine = true
  Type = 0
FEATURE [Sketcher::SketchObject] Sketch018
  ExternalGeometry = -> [Pocket003]
  FullyConstrained = true
  MapMode = 5
  Placement = pos=(0,0,0) rot=(1,0,0;3.14159rad)
  Support = -> [Pocket003]
  sketch-geometry (4):
    g0: LineSegment StartX=80.9 StartY=-63.3 StartZ=0 EndX=78.9 EndY=-63.3 EndZ=0
    g1: LineSegment StartX=78.9 StartY=-63.3 StartZ=0 EndX=78.9 EndY=-99.35 EndZ=0
    g2: LineSegment StartX=78.9 StartY=-99.35 StartZ=0 EndX=80.9 EndY=-99.35 EndZ=0
    g3: LineSegment StartX=80.9 StartY=-99.35 StartZ=0 EndX=80.9 EndY=-63.3 EndZ=0
  constraints (11):
    c: Coincident(g0,g1)
    c: Coincident(g1,g2)
    c: Coincident(g2,g3)
    c: Coincident(g3,g0)
    c: Horizontal(g0)
    c: Horizontal(g2)
    c: Vertical(g1)
    c: Vertical(g3)
    c: Coincident(g0,g-3)
    c: PointOnObject(g1,g-4)
    c: DistanceX(g0,g0) = 2
FEATURE [PartDesign::Pad] Pad029
  BaseFeature = -> Pocket003
  Direction = (0,0,-1)
  Length = 38.6
  Length2 = 10
  Profile = -> Sketch018
  ReferenceAxis = -> Sketch018 [N_Axis]
  Refine = true
  Type = 0
FEATURE [Sketcher::SketchObject] Sketch019
  ExternalGeometry = -> [Pad029]
  FullyConstrained = true
  MapMode = 5
  Placement = pos=(0,63.3,0) rot=(0,0.707107,0.707107;3.14159rad)
  Support = -> [Pad029]
  sketch-geometry (4):
    g0: LineSegment StartX=-93.5 StartY=2 StartZ=0 EndX=-91.5 EndY=2 EndZ=0
    g1: LineSegment StartX=-91.5 StartY=2 StartZ=0 EndX=-91.5 EndY=-38 EndZ=0
    g2: LineSegment StartX=-91.5 StartY=-38 StartZ=0 EndX=-93.5 EndY=-38 EndZ=0
    g3: LineSegment StartX=-93.5 StartY=-38 StartZ=0 EndX=-93.5 EndY=2 EndZ=0
  constraints (11):
    c: Coincident(g0,g1)
    c: Coincident(g1,g2)
    c: Coincident(g2,g3)
    c: Coincident(g3,g0)
    c: Horizontal(g0)
    c: Horizontal(g2)
    c: Vertical(g1)
    c: Vertical(g3)
    c: Coincident(g0,g-4)
    c: PointOnObject(g1,g-6)
    c: DistanceY(g3,g3) = 40
FEATURE [PartDesign::Pad] Pad030
  BaseFeature = -> Pad029
  Direction = (0,1,-2e-16)
  Length = 2.8
  Length2 = 10
  Profile = -> Sketch019
  ReferenceAxis = -> Sketch019 [N_Axis]
  Refine = true
  Type = 0
FEATURE [Sketcher::SketchObject] Sketch020
  ExternalGeometry = -> [Pad030]
  FullyConstrained = true
  MapMode = 5
  Placement = pos=(91.5,0,0) rot=(0.57735,-0.57735,-0.57735;2.0944rad)
  Support = -> [Pad030]
  sketch-geometry (4):
    g0: LineSegment StartX=-66.1 StartY=-38 StartZ=0 EndX=-64.6 EndY=-38 EndZ=0
    g1: LineSegment StartX=-64.6 StartY=-38 StartZ=0 EndX=-64.6 EndY=2 EndZ=0
    g2: LineSegment StartX=-64.6 StartY=2 StartZ=0 EndX=-66.1 EndY=2 EndZ=0
    g3: LineSegment StartX=-66.1 StartY=2 StartZ=0 EndX=-66.1 EndY=-38 EndZ=0
  constraints (11):
    c: Coincident(g0,g1)
    c: Coincident(g1,g2)
    c: Coincident(g2,g3)
    c: Coincident(g3,g0)
    c: Horizontal(g0)
    c: Horizontal(g2)
    c: Vertical(g1)
    c: Vertical(g3)
    c: Coincident(g0,g-5)
    c: PointOnObject(g1,g-4)
    c: DistanceX(g2,g2) = 1.5
FEATURE [PartDesign::Pad] Pad031
  BaseFeature = -> Pad030
  Direction = (-1,0,0)
  Length = 11
  Length2 = 10
  Profile = -> Sketch020
  ReferenceAxis = -> Sketch020 [N_Axis]
  Refine = true
  Type = 0
FEATURE [PartDesign::Pad] Pad032
  BaseFeature = -> Pad031
  Direction = (0,1,0)
  Length = 2
  Length2 = 10
  Profile = -> Pad031 [Face11]
  Refine = true
  Type = 0
FEATURE [PartDesign::Pocket] Pocket004
  BaseFeature = -> Pad032
  Direction = (-1,0,0)
  Length = 0.6
  Length2 = 5
  Profile = -> Pad032 [Face4]
  Refine = true
  Type = 0
FEATURE [PartDesign::Pocket] Pocket005
  BaseFeature = -> Pocket004
  Direction = (1,0,0)
  Length = 0.4
  Length2 = 5
  Profile = -> Pocket004 [Face10]
  Refine = true
  Type = 0
FEATURE [PartDesign::Pad] Pad033
  BaseFeature = -> Pocket005
  Direction = (1,0,-1e-16)
  Length = 0.4
  Length2 = 10
  Profile = -> Pocket005 [Face21]
  Refine = true
  Type = 0
FEATURE [Sketcher::SketchObject] Sketch021
  ExternalGeometry = -> [Pad033]
  FullyConstrained = true
  MapMode = 5
  Placement = pos=(93.9,1.9e-15,-1.13e-14) rot=(0.57735,0.57735,0.57735;2.0944rad)
  Support = -> [Pad033]
  sketch-geometry (1):
    g0: Circle CenterX=52.6 CenterY=-47.4 CenterZ=0 NormalX=0 NormalY=0 NormalZ=1 AngleXU=0 Radius=1.5
  constraints (3):
    c: Diameter(g0) = 3
    c: DistanceY(g-4,g0) = 3.7
    c: DistanceX(g0,g-4) = 10.7
FEATURE [PartDesign::Pocket] Pocket006
  BaseFeature = -> Pad033
  Direction = (-1,1e-16,1e-16)
  Length = 5
  Length2 = 5
  Profile = -> Sketch021
  ReferenceAxis = -> Sketch021 [N_Axis]
  Refine = true
  Type = 0
FEATURE [Sketcher::SketchObject] Sketch022
  ExternalGeometry = -> [Pad013]
  FullyConstrained = true
  MapMode = 5
  Placement = pos=(91.46,0,0) rot=(0.57735,0.57735,0.57735;2.0944rad)
  Support = -> [Pad013]
  sketch-geometry (1):
    g0: Circle CenterX=52.52 CenterY=3.72 CenterZ=0 NormalX=0 NormalY=0 NormalZ=1 AngleXU=0 Radius=1.4
  constraints (3):
    c: Diameter(g0) = 2.8
    c: DistanceY(g-3,g0) = 3.72
    c: DistanceX(g0,g-3) = 11.12
FEATURE [PartDesign::Pocket] Pocket007
  BaseFeature = -> Pad013
  Direction = (-1,0,0)
  Length = 7
  Length2 = 5
  Profile = -> Sketch022
  ReferenceAxis = -> Sketch022 [N_Axis]
  Refine = true
  Type = 0
FEATURE [Sketcher::SketchObject] Sketch023
  ExternalGeometry = -> [Pocket006]
  FullyConstrained = true
  MapMode = 5
  Placement = pos=(3.65,0,0) rot=(0.57735,-0.57735,-0.57735;2.0944rad)
  Support = -> [Pocket006]
  sketch-geometry (1):
    g0: Circle CenterX=-57.43 CenterY=-47.38 CenterZ=0 NormalX=0 NormalY=0 NormalZ=1 AngleXU=0 Radius=1.5
  constraints (3):
    c: Diameter(g0) = 3
    c: DistanceY(g-3,g0) = 3.62
    c: DistanceX(g-3,g0) = 5.62
FEATURE [PartDesign::Pocket] Pocket008
  BaseFeature = -> Pocket006
  Direction = (1,0,0)
  Length = 5
  Length2 = 5
  Profile = -> Sketch023
  ReferenceAxis = -> Sketch023 [N_Axis]
  Refine = true
  Type = 0
FEATURE [Sketcher::SketchObject] Sketch024
  ExternalGeometry = -> [Pocket007]
  FullyConstrained = true
  MapMode = 5
  Placement = pos=(5.99,0,0) rot=(0.57735,-0.57735,-0.57735;2.0944rad)
  Support = -> [Pocket007]
  sketch-geometry (1):
    g0: Circle CenterX=-57.37 CenterY=3.74 CenterZ=0 NormalX=0 NormalY=0 NormalZ=1 AngleXU=0 Radius=1.4
  constraints (3):
    c: Diameter(g0) = 2.8
    c: DistanceY(g-3,g0) = 3.74
    c: DistanceX(g-3,g0) = 6.27
FEATURE [PartDesign::Pocket] Pocket009
  BaseFeature = -> Pocket007
  Direction = (1,0,0)
  Length = 7
  Length2 = 5
  Profile = -> Sketch024
  ReferenceAxis = -> Sketch024 [N_Axis]
  Refine = true
  Type = 0
FEATURE [PartDesign::Pad] Pad034
  BaseFeature = -> Pocket009
  Direction = (1,0,0)
  Length = 2
  Length2 = 10
  Profile = -> Pocket009 [Face16]
  Refine = true
  Type = 0
FEATURE [PartDesign::Pocket] Pocket010
  BaseFeature = -> Pocket008
  Direction = (1,0,0)
  Length = 0.5
  Length2 = 5
  Profile = -> Pocket008 [Face19]
  Refine = true
  Type = 0
FEATURE [PartDesign::Pocket] Pocket011
  BaseFeature = -> Pocket010
  Direction = (0,1,0)
  Length = 1.2
  Length2 = 5
  Profile = -> Pocket010 [Face1]
  Refine = true
  Type = 0
FEATURE [Sketcher::SketchObject] Sketch025
  ExternalGeometry = -> [Pocket011]
  FullyConstrained = true
  MapMode = 5
  Placement = pos=(0,1e-16,2) rot=(0,0,1;0rad)
  Support = -> [Pocket011]
  sketch-geometry (2):
    g0: Circle CenterX=85.55 CenterY=36.6 CenterZ=0 NormalX=0 NormalY=0 NormalZ=1 AngleXU=0 Radius=2.5
    g1: Circle CenterX=85.55 CenterY=44 CenterZ=0 NormalX=0 NormalY=0 NormalZ=1 AngleXU=0 Radius=2.5
  constraints (6):
    c: Diameter(g1) = 5
    c: Diameter(g0) = 5
    c: DistanceY(g0,g1) = 7.4
    c: DistanceY(g-4,g0) = 21.9
    c: DistanceX(g0,g-4) = 8.35
    c: DistanceX(g1,g0) = 0
FEATURE [PartDesign::Pocket] Pocket012
  BaseFeature = -> Pocket011
  Direction = (0,0,-1)
  Length = 5
  Length2 = 5
  Profile = -> Sketch025
  ReferenceAxis = -> Sketch025 [N_Axis]
  Refine = true
  Type = 0
FEATURE [Sketcher::SketchObject] Sketch026
  ExternalGeometry = -> [Pocket012]
  FullyConstrained = true
  MapMode = 5
  Placement = pos=(0,0,0) rot=(1,0,0;3.14159rad)
  Support = -> [Pocket012]
  sketch-geometry (4):
    g0: Circle CenterX=85.55 CenterY=-36.6 CenterZ=0 NormalX=0 NormalY=0 NormalZ=1 AngleXU=0 Radius=2.5
    g1: Circle CenterX=85.55 CenterY=-44 CenterZ=0 NormalX=0 NormalY=0 NormalZ=1 AngleXU=0 Radius=2.5
    g2: Circle CenterX=85.55 CenterY=-36.6 CenterZ=0 NormalX=0 NormalY=0 NormalZ=1 AngleXU=0 Radius=4
    g3: Circle CenterX=85.55 CenterY=-44 CenterZ=0 NormalX=0 NormalY=0 NormalZ=1 AngleXU=0 Radius=4
  constraints (8):
    c: Coincident(g0,g-3)
    c: Coincident(g1,g-4)
    c: Diameter(g0) = 5
    c: Diameter(g1) = 5
    c: Coincident(g2,g0)
    c: Coincident(g3,g1)
    c: Diameter(g2) = 8
    c: Diameter(g3) = 8
FEATURE [Sketcher::SketchObject] Sketch032
  ExternalGeometry = -> [Pad034]
  FullyConstrained = true
  MapMode = 5
  Placement = pos=(91.96,0,0) rot=(0.57735,0.57735,0.57735;2.0944rad)
  Support = -> [Pad034]
  sketch-geometry (4):
    g0: LineSegment StartX=16.97 StartY=0 StartZ=0 EndX=29.97 EndY=0 EndZ=0
    g1: LineSegment StartX=29.97 StartY=0 StartZ=0 EndX=29.97 EndY=11 EndZ=0
    g2: LineSegment StartX=29.97 StartY=11 StartZ=0 EndX=16.97 EndY=11 EndZ=0
    g3: LineSegment StartX=16.97 StartY=11 StartZ=0 EndX=16.97 EndY=0 EndZ=0
  constraints (11):
    c: Coincident(g0,g1)
    c: Coincident(g1,g2)
    c: Coincident(g2,g3)
    c: Coincident(g3,g0)
    c: Horizontal(g0)
    c: Horizontal(g2)
    c: Vertical(g1)
    c: Vertical(g3)
    c: Coincident(g0,g-4)
    c: PointOnObject(g1,g-5)
    c: DistanceY(g1,g1) = 11
FEATURE [PartDesign::Pad] Pad039
  BaseFeature = -> Pad034
  Direction = (1,0,0)
  Length = 1.9
  Length2 = 10
  Profile = -> Sketch032
  ReferenceAxis = -> Sketch032 [N_Axis]
  Refine = true
  Type = 0
FEATURE [Sketcher::SketchObject] Sketch033
  ExternalGeometry = -> [Pad039]
  FullyConstrained = true
  MapMode = 5
  Placement = pos=(93.86,0,0) rot=(0.57735,0.57735,0.57735;2.0944rad)
  Support = -> [Pad039]
  sketch-geometry (4):
    g0: LineSegment StartX=16.97 StartY=0 StartZ=0 EndX=29.97 EndY=0 EndZ=0
    g1: LineSegment StartX=29.97 StartY=0 StartZ=0 EndX=29.97 EndY=4 EndZ=0
    g2: LineSegment StartX=29.97 StartY=4 StartZ=0 EndX=16.97 EndY=4 EndZ=0
    g3: LineSegment StartX=16.97 StartY=4 StartZ=0 EndX=16.97 EndY=0 EndZ=0
  constraints (11):
    c: Coincident(g0,g1)
    c: Coincident(g1,g2)
    c: Coincident(g2,g3)
    c: Coincident(g3,g0)
    c: Horizontal(g0)
    c: Horizontal(g2)
    c: Vertical(g1)
    c: Vertical(g3)
    c: Coincident(g0,g-4)
    c: PointOnObject(g1,g-5)
    c: DistanceY(g3,g3) = 4
FEATURE [PartDesign::Pad] Pad040
  BaseFeature = -> Pad039
  Direction = (1,0,0)
  Length = 12
  Length2 = 10
  Profile = -> Sketch033
  ReferenceAxis = -> Sketch033 [N_Axis]
  Refine = true
  Type = 0
FEATURE [Sketcher::SketchObject] Sketch034
  ExternalGeometry = -> [Pad040]
  FullyConstrained = true
  MapMode = 5
  Placement = pos=(0,0,4) rot=(0,0,1;0rad)
  Support = -> [Pad040]
  sketch-geometry (1):
    g0: Circle CenterX=99.86 CenterY=23.47 CenterZ=0 NormalX=0 NormalY=0 NormalZ=1 AngleXU=0 Radius=2.5
  constraints (5):
    c: Diameter(g0) = 5
    c: DistanceY(g0,g-5) = 6.5
    c: DistanceY(g-5,g0) = 6.5
    c: DistanceX(g-3,g0) = 6
    c: DistanceX(g0,g-5) = 6
FEATURE [PartDesign::Pocket] Pocket016
  BaseFeature = -> Pad040
  Direction = (0,0,-1)
  Length = 5
  Length2 = 5
  Profile = -> Sketch034
  ReferenceAxis = -> Sketch034 [N_Axis]
  Refine = true
  Type = 0
FEATURE [PartDesign::Fillet] Fillet
  Base = -> Pocket016 [Edge68,Edge72]
  BaseFeature = -> Pocket016
  Radius = 5
  Refine = true
  SupportTransform = false
  UseAllEdges = false
FEATURE [Sketcher::SketchObject] Sketch035
  ExternalGeometry = -> [Fillet]
  FullyConstrained = true
  MapMode = 5
  Placement = pos=(0,98.92,0) rot=(0,0.707107,0.707107;3.14159rad)
  Support = -> [Fillet]
  sketch-geometry (4):
    g0: LineSegment StartX=-19 StartY=0 StartZ=0 EndX=-7 EndY=0 EndZ=0
    g1: LineSegment StartX=-7 StartY=0 StartZ=0 EndX=-7 EndY=4 EndZ=0
    g2: LineSegment StartX=-7 StartY=4 StartZ=0 EndX=-19 EndY=4 EndZ=0
    g3: LineSegment StartX=-19 StartY=4 StartZ=0 EndX=-19 EndY=0 EndZ=0
  constraints (12):
    c: Coincident(g0,g1)
    c: Coincident(g1,g2)
    c: Coincident(g2,g3)
    c: Coincident(g3,g0)
    c: Horizontal(g0)
    c: Horizontal(g2)
    c: Vertical(g1)
    c: Vertical(g3)
    c: PointOnObject(g0,g-3)
    c: DistanceX(g2,g2) = 12
    c: DistanceY(g1,g1) = 4
    c: DistanceX(g0,g-3) = 7
FEATURE [PartDesign::Pad] Pad041
  BaseFeature = -> Fillet
  Direction = (0,1,-2e-16)
  Length = 12
  Length2 = 10
  Profile = -> Sketch035
  ReferenceAxis = -> Sketch035 [N_Axis]
  Refine = true
  Type = 0
FEATURE [Sketcher::SketchObject] Sketch036
  ExternalGeometry = -> [Pad041]
  FullyConstrained = true
  MapMode = 5
  Placement = pos=(0,9e-16,4) rot=(0,0,1;0rad)
  Support = -> [Pad041]
  sketch-geometry (1):
    g0: Circle CenterX=13 CenterY=104.92 CenterZ=0 NormalX=0 NormalY=0 NormalZ=1 AngleXU=0 Radius=2.5
  constraints (5):
    c: Diameter(g0) = 5
    c: DistanceX(g-4,g0) = 6
    c: DistanceX(g0,g-5) = 6
    c: DistanceY(g0,g-4) = 6
    c: DistanceY(g-3,g0) = 6
FEATURE [PartDesign::Pocket] Pocket017
  BaseFeature = -> Pad041
  Direction = (0,-2e-16,-1)
  Length = 5
  Length2 = 5
  Profile = -> Sketch036
  ReferenceAxis = -> Sketch036 [N_Axis]
  Refine = true
  Type = 0
FEATURE [PartDesign::Fillet] Fillet001
  Base = -> Pocket017 [Edge102,Edge105]
  BaseFeature = -> Pocket017
  Radius = 5
  Refine = true
  SupportTransform = false
  UseAllEdges = false
FEATURE [Part::Part2DObjectPython] ShapeString  # Draft 2D object (typed FeaturePython)
  FontFile = <userpath>/Documents/FreeCad/Fonts/Stencil_tenada/Tenada.ttf
  MakeFace = true
  Placement = pos=(0,98.11,0.84) rot=(0.57735,-0.57735,-0.57735;2.0944rad)
  Size = 3.5
  String = AC-IN
  Tracking = 0
FEATURE [PartDesign::Pad] Pad042
  BaseFeature = -> Fillet001
  Direction = (-1,0,0)
  Length = 1
  Length2 = 10
  Profile = -> ShapeString
  ReferenceAxis = -> ShapeString [N_Axis]
  Refine = true
  Type = 0
FEATURE [Part::Part2DObjectPython] ShapeString001  # Draft 2D object (typed FeaturePython)
  FontFile = <userpath>/Documents/FreeCad/Fonts/Stencil_tenada/Tenada.ttf
  MakeFace = true
  Placement = pos=(100.82,63.75,1.31) rot=(0.57735,0.57735,0.57735;2.0944rad)
  Size = 3
  String = AC.OUT
  Tracking = 0
FEATURE [PartDesign::Pad] Pad043
  BaseFeature = -> Pad042
  Direction = (1,0,0)
  Length = 1
  Length2 = 10
  Profile = -> ShapeString001
  ReferenceAxis = -> ShapeString001 [N_Axis]
  Refine = true
  Type = 0
FEATURE [PartDesign::Pocket] Pocket020
  BaseFeature = -> Pad021
  Direction = (0,-1,-1e-16)
  Length = 1
  Length2 = 5
  Profile = -> Pad021 [Face9]
  Refine = true
  Type = 0
FEATURE [PartDesign::Pocket] Pocket021
  BaseFeature = -> Pocket020
  Direction = (-1,0,0)
  Length = 1
  Length2 = 5
  Profile = -> Pocket020 [Face1]
  Refine = true
  Type = 0
FEATURE [PartDesign::Fillet] Fillet002
  Base = -> Pocket021 [Edge27,Edge22,Edge25,Edge23]
  BaseFeature = -> Pocket021
  Radius = 1
  Refine = true
  SupportTransform = false
  UseAllEdges = false
FEATURE [PartDesign::Pad] Pad045
  BaseFeature = -> Fillet002
  Direction = (0,0,1)
  Length = 2
  Length2 = 10
  Profile = -> Fillet002 [Face14]
  Refine = true
  Type = 0
FEATURE [PartDesign::Pocket] Pocket022
  BaseFeature = -> Pad045
  Direction = (0,0,1)
  Length = 2
  Length2 = 5
  Profile = -> Pad045 [Face1]
  Refine = true
  Type = 0
FEATURE [PartDesign::Body] Body002  label="LidBoton"
  Group = -> [Sketch009,Pad015,Sketch010,Pad016,Sketch011,Pocket001,Pad020,Pad021,Pocket020,Pocket021,Fillet002,Pad045,Pocket022]
  Origin = -> Origin051
  Placement = pos=(-0.2,0.465,-28.99) rot=(0,0,1;0rad)
  Tip = -> Pocket022
FEATURE [PartDesign::Pad] Pad035
  BaseFeature = -> Pocket012
  Direction = (0,0,-1)
  Length = 38
  Length2 = 10
  Profile = -> Sketch026
  ReferenceAxis = -> Sketch026 [N_Axis]
  Refine = true
  Type = 0
FEATURE [Sketcher::SketchObject] Sketch027
  ExternalGeometry = -> [Pad035]
  FullyConstrained = true
  MapMode = 5
  Placement = pos=(91.9,0,0) rot=(0.57735,-0.57735,-0.57735;2.0944rad)
  Support = -> [Pad035]
  sketch-geometry (4):
    g0: LineSegment StartX=-62.1 StartY=-11.8 StartZ=0 EndX=-53.3 EndY=-11.8 EndZ=0
    g1: LineSegment StartX=-53.3 StartY=-11.8 StartZ=0 EndX=-53.3 EndY=-3 EndZ=0
    g2: LineSegment StartX=-53.3 StartY=-3 StartZ=0 EndX=-62.1 EndY=-3 EndZ=0
    g3: LineSegment StartX=-62.1 StartY=-3 StartZ=0 EndX=-62.1 EndY=-11.8 EndZ=0
  constraints (12):
    c: Coincident(g0,g1)
    c: Coincident(g1,g2)
    c: Coincident(g2,g3)
    c: Coincident(g3,g0)
    c: Horizontal(g0)
    c: Horizontal(g2)
    c: Vertical(g1)
    c: Vertical(g3)
    c: DistanceY(g3,g3) = 8.8
    c: DistanceX(g2,g2) = 8.8
    c: DistanceY(g1,g-4) = 5
    c: DistanceX(g-4,g2) = 4
FEATURE [PartDesign::Pocket] Pocket013
  BaseFeature = -> Pad035
  Direction = (1,0,0)
  Length = 1
  Length2 = 5
  Profile = -> Sketch027
  ReferenceAxis = -> Sketch027 [N_Axis]
  Refine = true
  Type = 0
FEATURE [Sketcher::SketchObject] Sketch028
  ExternalGeometry = -> [Pocket013]
  FullyConstrained = true
  MapMode = 5
  Placement = pos=(92.9,0,0) rot=(0.57735,-0.57735,-0.57735;2.0944rad)
  Support = -> [Pocket013]
  sketch-geometry (1):
    g0: Circle CenterX=-57.7 CenterY=-7.4 CenterZ=0 NormalX=0 NormalY=0 NormalZ=1 AngleXU=0 Radius=3.5
  constraints (5):
    c: Diameter(g0) = 7
    c: DistanceX(g0,g-5) = 4.4
    c: DistanceX(g-4,g0) = 4.4
    c: DistanceY(g0,g-5) = 4.4
    c: DistanceY(g-5,g0) = 4.4
FEATURE [PartDesign::Pocket] Pocket014
  BaseFeature = -> Pocket013
  Direction = (1,0,0)
  Length = 5
  Length2 = 5
  Profile = -> Sketch028
  ReferenceAxis = -> Sketch028 [N_Axis]
  Refine = true
  Type = 0
FEATURE [Sketcher::SketchObject] Sketch029
  ExternalGeometry = -> [Pocket014]
  FullyConstrained = true
  MapMode = 5
  Placement = pos=(91.9,0,0) rot=(0.57735,-0.57735,-0.57735;2.0944rad)
  Support = -> [Pocket014]
  sketch-geometry (8):
    g0: LineSegment StartX=-64.6 StartY=-16 StartZ=0 EndX=-50.6 EndY=-16 EndZ=0
    g1: LineSegment StartX=-50.6 StartY=-16 StartZ=0 EndX=-50.6 EndY=0 EndZ=0
    g2: LineSegment StartX=-50.6 StartY=0 StartZ=0 EndX=-64.6 EndY=0 EndZ=0
    g3: LineSegment StartX=-64.6 StartY=0 StartZ=0 EndX=-64.6 EndY=-16 EndZ=0
    g4: LineSegment StartX=-62.1 StartY=-11.8 StartZ=0 EndX=-53.3 EndY=-11.8 EndZ=0
    g5: LineSegment StartX=-53.3 StartY=-11.8 StartZ=0 EndX=-53.3 EndY=-3 EndZ=0
    g6: LineSegment StartX=-53.3 StartY=-3 StartZ=0 EndX=-62.1 EndY=-3 EndZ=0
    g7: LineSegment StartX=-62.1 StartY=-3 StartZ=0 EndX=-62.1 EndY=-11.8 EndZ=0
  constraints (21):
    c: Coincident(g0,g1)
    c: Coincident(g1,g2)
    c: Coincident(g2,g3)
    c: Coincident(g3,g0)
    c: Horizontal(g0)
    c: Horizontal(g2)
    c: Vertical(g1)
    c: Vertical(g3)
    c: Coincident(g2,g-4)
    c: DistanceX(g2,g2) = 14
    c: DistanceY(g1,g1) = 16
    c: Coincident(g4,g5)
    c: Coincident(g5,g6)
    c: Coincident(g6,g7)
    c: Coincident(g7,g4)
    c: Horizontal(g4)
    c: Horizontal(g6)
    c: Vertical(g5)
    c: Vertical(g7)
    c: Coincident(g4,g-8)
    c: Coincident(g5,g-7)
FEATURE [PartDesign::Pad] Pad036
  BaseFeature = -> Pocket014
  Direction = (-1,0,0)
  Length = 2
  Length2 = 10
  Profile = -> Sketch029
  ReferenceAxis = -> Sketch029 [N_Axis]
  Refine = true
  Type = 0
FEATURE [PartDesign::Pad] Pad037
  BaseFeature = -> Pad036
  Direction = (-1,0,0)
  Length = 1
  Length2 = 10
  Profile = -> Pad036 [Face48]
  Refine = true
  Type = 0
FEATURE [Sketcher::SketchObject] Sketch030
  ExternalGeometry = -> [Pad037]
  FullyConstrained = true
  MapMode = 5
  Placement = pos=(0,1e-16,2) rot=(0,0,1;0rad)
  Support = -> [Pad037]
  sketch-geometry (4):
    g0: LineSegment StartX=39.5 StartY=78.15 StartZ=0 EndX=62.3 EndY=78.15 EndZ=0
    g1: LineSegment StartX=62.3 StartY=78.15 StartZ=0 EndX=62.3 EndY=65.35 EndZ=0
    g2: LineSegment StartX=62.3 StartY=65.35 StartZ=0 EndX=39.5 EndY=65.35 EndZ=0
    g3: LineSegment StartX=39.5 StartY=65.35 StartZ=0 EndX=39.5 EndY=78.15 EndZ=0
  constraints (12):
    c: Coincident(g0,g1)
    c: Coincident(g1,g2)
    c: Coincident(g2,g3)
    c: Coincident(g3,g0)
    c: Horizontal(g0)
    c: Horizontal(g2)
    c: Vertical(g1)
    c: Vertical(g3)
    c: DistanceX(g0,g0) = 22.8
    c: DistanceY(g1,g1) = 12.8
    c: DistanceY(g0,g-3) = 23
    c: DistanceX(g-4,g0) = 18.5
FEATURE [PartDesign::Pocket] Pocket015
  BaseFeature = -> Pad037
  Direction = (0,0,-1)
  Length = 5
  Length2 = 5
  Profile = -> Sketch030
  ReferenceAxis = -> Sketch030 [N_Axis]
  Refine = true
  Type = 0
FEATURE [Sketcher::SketchObject] Sketch031
  ExternalGeometry = -> [Pocket015]
  FullyConstrained = true
  MapMode = 5
  Placement = pos=(0,0,0) rot=(1,0,0;3.14159rad)
  Support = -> [Pocket015]
  sketch-geometry (8):
    g0: LineSegment StartX=37 StartY=-55.85 StartZ=0 EndX=64.8 EndY=-55.85 EndZ=0
    g1: LineSegment StartX=64.8 StartY=-55.85 StartZ=0 EndX=64.8 EndY=-84.65 EndZ=0
    g2: LineSegment StartX=64.8 StartY=-84.65 StartZ=0 EndX=37 EndY=-84.65 EndZ=0
    g3: LineSegment StartX=37 StartY=-84.65 StartZ=0 EndX=37 EndY=-55.85 EndZ=0
    g4: LineSegment StartX=35 StartY=-53.85 StartZ=0 EndX=66.8 EndY=-53.85 EndZ=0
    g5: LineSegment StartX=66.8 StartY=-53.85 StartZ=0 EndX=66.8 EndY=-86.65 EndZ=0
    g6: LineSegment StartX=66.8 StartY=-86.65 StartZ=0 EndX=35 EndY=-86.65 EndZ=0
    g7: LineSegment StartX=35 StartY=-86.65 StartZ=0 EndX=35 EndY=-53.85 EndZ=0
  constraints (24):
    c: Coincident(g0,g1)
    c: Coincident(g1,g2)
    c: Coincident(g2,g3)
    c: Coincident(g3,g0)
    c: Horizontal(g0)
    c: Horizontal(g2)
    c: Vertical(g1)
    c: Vertical(g3)
    c: Coincident(g4,g5)
    c: Coincident(g5,g6)
    c: Coincident(g6,g7)
    c: Coincident(g7,g4)
    c: Horizontal(g4)
    c: Horizontal(g6)
    c: Vertical(g5)
    c: Vertical(g7)
    c: DistanceY(g2,g-3) = 6.5
    c: DistanceY(g-4,g0) = 9.5
    c: DistanceY(g6,g2) = 2
    c: DistanceY(g0,g4) = 2
    c: DistanceX(g-3,g1) = 2.5
    c: DistanceX(g2,g-3) = 2.5
    c: DistanceX(g1,g5) = 2
    c: DistanceX(g4,g0) = 2
FEATURE [PartDesign::Pad] Pad038
  BaseFeature = -> Pocket015
  Direction = (0,0,-1)
  Length = 3
  Length2 = 10
  Profile = -> Sketch031
  ReferenceAxis = -> Sketch031 [N_Axis]
  Refine = true
  Type = 0
FEATURE [Part::Part2DObjectPython] ShapeString002  # Draft 2D object (typed FeaturePython)
  AttachmentOffset = pos=(22,53,0) rot=(0,0,1;0rad)
  FontFile = <userpath>/Documents/FreeCad/Fonts/Stencil_tenada/Tenada.ttf
  MakeFace = true
  MapMode = 5
  Placement = pos=(22,14.7,53) rot=(1,0,0;1.5708rad)
  Size = 2.5
  String = WiFi Smart Pump
  Support = -> [Pad038]
  Tracking = 0
FEATURE [PartDesign::Pocket] Pocket018
  BaseFeature = -> Pad038
  Direction = (0,1,-2e-16)
  Length = 0.7
  Length2 = 5
  Profile = -> ShapeString002
  ReferenceAxis = -> ShapeString002 [N_Axis]
  Refine = true
  Type = 0
FEATURE [Part::Part2DObjectPython] ShapeString003  # Draft 2D object (typed FeaturePython)
  AttachmentOffset = pos=(33,43,0) rot=(0,0,1;0rad)
  FontFile = <userpath>/Documents/FreeCad/Fonts/Stencil_tenada/Tenada.ttf
  MakeFace = true
  MapMode = 5
  Placement = pos=(33,14.7,43) rot=(1,0,0;1.5708rad)
  Size = 2.4
  String = Controller S1
  Support = -> [Pocket018]
  Tracking = 0
FEATURE [PartDesign::Pocket] Pocket019
  BaseFeature = -> Pocket018
  Direction = (0,1,-2e-16)
  Length = 0.7
  Length2 = 5
  Profile = -> ShapeString003
  ReferenceAxis = -> ShapeString003 [N_Axis]
  Refine = true
  Type = 0
FEATURE [PartDesign::Pad] Pad044
  BaseFeature = -> Pocket019
  Direction = (0,-1,0)
  Length = 1
  Length2 = 10
  Profile = -> Pocket019 [Face29]
  Refine = true
  Type = 0
FEATURE [Sketcher::SketchObject] Sketch037
  ExternalGeometry = -> [Pad044]
  FullyConstrained = false
  MapMode = 5
  Placement = pos=(0,1e-16,2) rot=(0,0,1;0rad)
  Support = -> [Pad044]
  sketch-geometry (4):
    g0: LineSegment StartX=93.9 StartY=48.3611 StartZ=0 EndX=81.2 EndY=48.3611 EndZ=0
    g1: LineSegment StartX=81.2 StartY=48.3611 StartZ=0 EndX=81.2 EndY=32.3611 EndZ=0
    g2: LineSegment StartX=81.2 StartY=32.3611 StartZ=0 EndX=93.9 EndY=32.3611 EndZ=0
    g3: LineSegment StartX=93.9 StartY=32.3611 StartZ=0 EndX=93.9 EndY=48.3611 EndZ=0
  constraints (11):
    c: Coincident(g0,g1)
    c: Coincident(g1,g2)
    c: Coincident(g2,g3)
    c: Coincident(g3,g0)
    c: Horizontal(g0)
    c: Horizontal(g2)
    c: Vertical(g1)
    c: Vertical(g3)
    c: PointOnObject(g0,g-3)
    c: DistanceY(g1,g1) = 16
    c: DistanceX(g0,g0) = 12.7
FEATURE [PartDesign::Pocket] Pocket023
  BaseFeature = -> Pad044
  Direction = (0,0,-1)
  Length = 122
  Length2 = 5
  Profile = -> Sketch037
  ReferenceAxis = -> Sketch037 [N_Axis]
  Refine = true
  Type = 0
FEATURE [PartDesign::Pocket] Pocket024
  BaseFeature = -> Pocket023
  Direction = (0,0,1)
  Length = 1
  Length2 = 5
  Profile = -> Pocket023 [Face46]
  Refine = true
  Type = 0
FEATURE [PartDesign::Pocket] Pocket025
  BaseFeature = -> Pocket024
  Direction = (0,0,-1)
  Length = 1
  Length2 = 5
  Profile = -> Pocket024 [Face45]
  Refine = true
  Type = 0
FEATURE [PartDesign::Pad] Pad046
  BaseFeature = -> Pocket025
  Direction = (1,0,0)
  Length = 2
  Length2 = 10
  Profile = -> Pocket025 [Face13]
  Refine = true
  Type = 0
FEATURE [PartDesign::Pad] Pad047
  BaseFeature = -> Pad046
  Direction = (0,-1,0)
  Length = 2.5
  Length2 = 10
  Profile = -> Pad046 [Face1]
  Refine = true
  Type = 0
FEATURE [PartDesign::Pad] Pad048
  BaseFeature = -> Pad047
  Direction = (0,1,0)
  Length = 3.5
  Length2 = 10
  Profile = -> Pad047 [Face19]
  Refine = true
  Type = 0
FEATURE [Sketcher::SketchObject] Sketch038
  ExternalGeometry = -> [Pad048]
  FullyConstrained = true
  MapMode = 5
  Placement = pos=(0,0,0) rot=(1,0,0;3.14159rad)
  Support = -> [Pad048]
  sketch-geometry (4):
    g0: LineSegment StartX=83.2 StartY=-33.8611 StartZ=0 EndX=81.7 EndY=-33.8611 EndZ=0
    g1: LineSegment StartX=81.7 StartY=-33.8611 StartZ=0 EndX=81.7 EndY=-47.8611 EndZ=0
    g2: LineSegment StartX=81.7 StartY=-47.8611 StartZ=0 EndX=83.2 EndY=-47.8611 EndZ=0
    g3: LineSegment StartX=83.2 StartY=-47.8611 StartZ=0 EndX=83.2 EndY=-33.8611 EndZ=0
  constraints (12):
    c: Coincident(g0,g1)
    c: Coincident(g1,g2)
    c: Coincident(g2,g3)
    c: Coincident(g3,g0)
    c: Horizontal(g0)
    c: Horizontal(g2)
    c: Vertical(g1)
    c: Vertical(g3)
    c: PointOnObject(g0,g-3)
    c: DistanceY(g-3,g0) = 2
    c: DistanceY(g2,g-3) = 2
    c: DistanceX(g0,g0) = 1.5
FEATURE [PartDesign::Pad] Pad049
  BaseFeature = -> Pad048
  Direction = (0,0,-1)
  Length = 38.4
  Length2 = 10
  Profile = -> Sketch038
  ReferenceAxis = -> Sketch038 [N_Axis]
  Refine = true
  Type = 0
FEATURE [Sketcher::SketchObject] Sketch039
  ExternalGeometry = -> [Pad049]
  FullyConstrained = true
  MapMode = 5
  Placement = pos=(83.2,0,3.24e-14) rot=(0.57735,0.57735,0.57735;2.0944rad)
  Support = -> [Pad049]
  sketch-geometry (8):
    g0: LineSegment StartX=47.8611 StartY=-3.55e-14 StartZ=0 EndX=45.8611 EndY=-3.55e-14 EndZ=0
    g1: LineSegment StartX=45.8611 StartY=-3.55e-14 StartZ=0 EndX=45.8611 EndY=-38.4 EndZ=0
    g2: LineSegment StartX=45.8611 StartY=-38.4 StartZ=0 EndX=47.8611 EndY=-38.4 EndZ=0
    g3: LineSegment StartX=47.8611 StartY=-38.4 StartZ=0 EndX=47.8611 EndY=-3.55e-14 EndZ=0
    g4: LineSegment StartX=33.8611 StartY=0 StartZ=0 EndX=35.8611 EndY=0 EndZ=0
    g5: LineSegment StartX=35.8611 StartY=0 StartZ=0 EndX=35.8611 EndY=-38.4 EndZ=0
    g6: LineSegment StartX=35.8611 StartY=-38.4 StartZ=0 EndX=33.8611 EndY=-38.4 EndZ=0
    g7: LineSegment StartX=33.8611 StartY=-38.4 StartZ=0 EndX=33.8611 EndY=0 EndZ=0
  constraints (23):
    c: Coincident(g0,g1)
    c: Coincident(g1,g2)
    c: Coincident(g2,g3)
    c: Coincident(g3,g0)
    c: Horizontal(g0)
    c: Horizontal(g2)
    c: Vertical(g1)
    c: Vertical(g3)
    c: Coincident(g0,g-4)
    c: PointOnObject(g1,g-5)
    c: DistanceX(g2,g2) = 2
    c: Coincident(g4,g5)
    c: Coincident(g5,g6)
    c: Coincident(g6,g7)
    c: Coincident(g7,g4)
    c: Horizontal(g4)
    c: Horizontal(g6)
    c: Vertical(g5)
    c: Vertical(g7)
    c: PointOnObject(g4,g-3)
    c: DistanceX(g4,g4) = 2
    c: PointOnObject(g5,g-5)
    c: PointOnObject(g4,g-1)
FEATURE [PartDesign::Pad] Pad050
  BaseFeature = -> Pad049
  Direction = (1,0,4e-16)
  Length = 9
  Length2 = 10
  Profile = -> Sketch039
  ReferenceAxis = -> Sketch039 [N_Axis]
  Refine = true
  Type = 0
FEATURE [Sketcher::SketchObject] Sketch040
  ExternalGeometry = -> [Pad050]
  FullyConstrained = true
  MapMode = 5
  Placement = pos=(83.2,0,3.24e-14) rot=(0.57735,0.57735,0.57735;2.0944rad)
  Support = -> [Pad050]
  sketch-geometry (4):
    g0: LineSegment StartX=35.8611 StartY=-33.4 StartZ=0 EndX=45.8611 EndY=-33.4 EndZ=0
    g1: LineSegment StartX=45.8611 StartY=-33.4 StartZ=0 EndX=45.8611 EndY=-36.4 EndZ=0
    g2: LineSegment StartX=45.8611 StartY=-36.4 StartZ=0 EndX=35.8611 EndY=-36.4 EndZ=0
    g3: LineSegment StartX=35.8611 StartY=-36.4 StartZ=0 EndX=35.8611 EndY=-33.4 EndZ=0
  constraints (12):
    c: Coincident(g0,g1)
    c: Coincident(g1,g2)
    c: Coincident(g2,g3)
    c: Coincident(g3,g0)
    c: Horizontal(g0)
    c: Horizontal(g2)
    c: Vertical(g1)
    c: Vertical(g3)
    c: DistanceY(g-3,g2) = 2
    c: DistanceY(g3,g3) = 3
    c: PointOnObject(g0,g-5)
    c: PointOnObject(g0,g-4)
FEATURE [PartDesign::Pad] Pad051
  BaseFeature = -> Pad050
  Direction = (1,0,4e-16)
  Length = 10.7
  Length2 = 10
  Profile = -> Sketch040
  ReferenceAxis = -> Sketch040 [N_Axis]
  Refine = true
  Type = 0
FEATURE [Sketcher::SketchObject] Sketch041
  ExternalGeometry = -> [Pad051]
  FullyConstrained = true
  MapMode = 5
  Placement = pos=(0,45.8611,0) rot=(1,0,0;1.5708rad)
  Support = -> [Pad051]
  sketch-geometry (4):
    g0: LineSegment StartX=91.9 StartY=-51.1 StartZ=0 EndX=93.9 EndY=-51.1 EndZ=0
    g1: LineSegment StartX=93.9 StartY=-51.1 StartZ=0 EndX=93.9 EndY=-36.4 EndZ=0
    g2: LineSegment StartX=93.9 StartY=-36.4 StartZ=0 EndX=91.9 EndY=-36.4 EndZ=0
    g3: LineSegment StartX=91.9 StartY=-36.4 StartZ=0 EndX=91.9 EndY=-51.1 EndZ=0
  constraints (11):
    c: Coincident(g0,g1)
    c: Coincident(g1,g2)
    c: Coincident(g2,g3)
    c: Coincident(g3,g0)
    c: Horizontal(g0)
    c: Horizontal(g2)
    c: Vertical(g1)
    c: Vertical(g3)
    c: Coincident(g0,g-3)
    c: PointOnObject(g0,g-5)
    c: PointOnObject(g1,g-4)
FEATURE [PartDesign::Pad] Pad052
  BaseFeature = -> Pad051
  Direction = (0,-1,2e-16)
  Length = 10
  Length2 = 10
  Profile = -> Sketch041
  ReferenceAxis = -> Sketch041 [N_Axis]
  Refine = true
  Type = 0
FEATURE [PartDesign::Fillet] Fillet003
  Base = -> Pad052 [Edge32,Edge28]
  BaseFeature = -> Pad052
  Radius = 2
  Refine = true
  SupportTransform = false
  UseAllEdges = false
FEATURE [PartDesign::Fillet] Fillet004
  Base = -> Fillet003 [Edge166,Edge164]
  BaseFeature = -> Fillet003
  Radius = 3
  Refine = true
  SupportTransform = false
  UseAllEdges = false
FEATURE [Sketcher::SketchObject] Sketch042
  ExternalGeometry = -> [Fillet004]
  FullyConstrained = true
  MapMode = 5
  Placement = pos=(1.6e-14,0,-36.4) rot=(1,0,0;3.14159rad)
  Support = -> [Fillet004]
  sketch-geometry (8):
    g0: LineSegment StartX=83.51 StartY=-36.0511 StartZ=0 EndX=86.81 EndY=-36.0511 EndZ=0
    g1: LineSegment StartX=86.81 StartY=-36.0511 StartZ=0 EndX=86.81 EndY=-38.0511 EndZ=0
    g2: LineSegment StartX=86.81 StartY=-38.0511 StartZ=0 EndX=83.51 EndY=-38.0511 EndZ=0
    g3: LineSegment StartX=83.51 StartY=-38.0511 StartZ=0 EndX=83.51 EndY=-36.0511 EndZ=0
    g4: LineSegment StartX=83.51 StartY=-45.4811 StartZ=0 EndX=86.81 EndY=-45.4811 EndZ=0
    g5: LineSegment StartX=86.81 StartY=-45.4811 StartZ=0 EndX=86.81 EndY=-43.4811 EndZ=0
    g6: LineSegment StartX=86.81 StartY=-43.4811 StartZ=0 EndX=83.51 EndY=-43.4811 EndZ=0
    g7: LineSegment StartX=83.51 StartY=-43.4811 StartZ=0 EndX=83.51 EndY=-45.4811 EndZ=0
  constraints (24):
    c: Coincident(g0,g1)
    c: Coincident(g1,g2)
    c: Coincident(g2,g3)
    c: Coincident(g3,g0)
    c: Horizontal(g0)
    c: Horizontal(g2)
    c: Vertical(g1)
    c: Vertical(g3)
    c: Coincident(g4,g5)
    c: Coincident(g5,g6)
    c: Coincident(g6,g7)
    c: Coincident(g7,g4)
    c: Horizontal(g4)
    c: Horizontal(g6)
    c: Vertical(g5)
    c: Vertical(g7)
    c: DistanceX(g0,g0) = 3.3
    c: DistanceY(g1,g1) = 2
    c: DistanceY(g5,g5) = 2
    c: DistanceX(g6,g6) = 3.3
    c: DistanceX(g-3,g2) = 0.31
    c: DistanceX(g-3,g4) = 0.31
    c: DistanceY(g2,g-3) = 2.19
    c: DistanceY(g-3,g6) = 2.38
FEATURE [PartDesign::Pocket] Pocket026
  BaseFeature = -> Fillet004
  Direction = (-4e-16,0,1)
  Length = 2.4
  Length2 = 5
  Profile = -> Sketch042
  ReferenceAxis = -> Sketch042 [N_Axis]
  Refine = true
  Type = 0
FEATURE [Sketcher::SketchObject] Sketch043
  ExternalGeometry = -> [Pocket026]
  FullyConstrained = true
  MapMode = 5
  Placement = pos=(1.6e-14,0,-36.4) rot=(1,0,0;3.14159rad)
  Support = -> [Pocket026]
  sketch-geometry (4):
    g0: LineSegment StartX=83.2 StartY=-39.8611 StartZ=0 EndX=91.9 EndY=-39.8611 EndZ=0
    g1: LineSegment StartX=91.9 StartY=-39.8611 StartZ=0 EndX=91.9 EndY=-41.8611 EndZ=0
    g2: LineSegment StartX=91.9 StartY=-41.8611 StartZ=0 EndX=83.2 EndY=-41.8611 EndZ=0
    g3: LineSegment StartX=83.2 StartY=-41.8611 StartZ=0 EndX=83.2 EndY=-39.8611 EndZ=0
  constraints (13):
    c: Coincident(g0,g1)
    c: Coincident(g1,g2)
    c: Coincident(g2,g3)
    c: Coincident(g3,g0)
    c: Horizontal(g0)
    c: Horizontal(g2)
    c: Vertical(g1)
    c: Vertical(g3)
    c: PointOnObject(g0,g-3)
    c: PointOnObject(g1,g-4)
    c: DistanceY(g3,g3) = 2
    c: DistanceY(g0,g-3) = 4
    c: DistanceY(g-3,g2) = 4
FEATURE [PartDesign::Pad] Pad053
  BaseFeature = -> Pocket026
  Direction = (4e-16,0,-1)
  Length = 2
  Length2 = 10
  Profile = -> Sketch043
  ReferenceAxis = -> Sketch043 [N_Axis]
  Refine = true
  Type = 0
FEATURE [PartDesign::Pad] Pad054
  BaseFeature = -> Pad053
  Direction = (0,-1,0)
  Length = 0.3
  Length2 = 10
  Profile = -> Pad053 [Face26]
  Refine = true
  Type = 0
FEATURE [PartDesign::Pad] Pad055
  BaseFeature = -> Pad054
  Direction = (0,0,-1)
  Length = 0.1
  Length2 = 10
  Profile = -> Pad054 [Face25]
  Refine = true
  Type = 0
FEATURE [Sketcher::SketchObject] Sketch044
  ExternalGeometry = -> [Pad055]
  FullyConstrained = true
  MapMode = 5
  Placement = pos=(-2e-16,16.7,-1e-15) rot=(0,0.707107,0.707107;3.14159rad)
  Support = -> [Pad055]
  sketch-geometry (4):
    g0: LineSegment StartX=-93.9 StartY=-28.8 StartZ=0 EndX=-92.2 EndY=-28.8 EndZ=0
    g1: LineSegment StartX=-92.2 StartY=-28.8 StartZ=0 EndX=-92.2 EndY=-39.8 EndZ=0
    g2: LineSegment StartX=-92.2 StartY=-39.8 StartZ=0 EndX=-93.9 EndY=-39.8 EndZ=0
    g3: LineSegment StartX=-93.9 StartY=-39.8 StartZ=0 EndX=-93.9 EndY=-28.8 EndZ=0
  constraints (11):
    c: Coincident(g0,g1)
    c: Coincident(g1,g2)
    c: Coincident(g2,g3)
    c: Coincident(g3,g0)
    c: Horizontal(g0)
    c: Horizontal(g2)
    c: Vertical(g1)
    c: Vertical(g3)
    c: Coincident(g0,g-3)
    c: DistanceY(g3,g3) = 11
    c: DistanceX(g0,g0) = 1.7
FEATURE [PartDesign::Pad] Pad056
  BaseFeature = -> Pad055
  Direction = (0,1,-2e-16)
  Length = 2
  Length2 = 10
  Profile = -> Sketch044
  ReferenceAxis = -> Sketch044 [N_Axis]
  Refine = true
  Type = 0
FEATURE [Part::Part2DObjectPython] ShapeString004  # Draft 2D object (typed FeaturePython)
  AttachmentOffset = pos=(-25,-17,0) rot=(0,0,1;3.14159rad)
  FontFile = <userpath>/Documents/FreeCad/Fonts/Stencil_tenada/Tenada.ttf
  MakeFace = true
  MapMode = 5
  Placement = pos=(25,101.15,-17) rot=(1,0,0;4.71239rad)
  Size = 3
  String = WaterLevel
  Support = -> [Pad056]
  Tracking = 0
FEATURE [PartDesign::Pad] Pad057
  BaseFeature = -> Pad056
  Direction = (0,1,-2e-16)
  Length = 1
  Length2 = 10
  Profile = -> ShapeString004
  ReferenceAxis = -> ShapeString004 [N_Axis]
  Refine = true
  Type = 0
FEATURE [Part::Part2DObjectPython] ShapeString005  # Draft 2D object (typed FeaturePython)
  AttachmentOffset = pos=(-43,-7,0) rot=(0,0,1;3.14159rad)
  FontFile = <userpath>/Documents/FreeCad/Fonts/Stencil_tenada/Tenada.ttf
  MakeFace = true
  MapMode = 5
  Placement = pos=(43,101.15,-7) rot=(1,0,0;4.71239rad)
  Size = 3
  String = .Pro
  Support = -> [Pad057]
  Tracking = 0
FEATURE [PartDesign::Pad] Pad058
  BaseFeature = -> Pad057
  Direction = (0,1,-2e-16)
  Length = 1
  Length2 = 10
  Profile = -> ShapeString005
  ReferenceAxis = -> ShapeString005 [N_Axis]
  Refine = true
  Type = 0
FEATURE [Part::Part2DObjectPython] ShapeString006  # Draft 2D object (typed FeaturePython)
  FontFile = <userpath>/Documents/FreeCad/Fonts/Stencil_tenada/Tenada.ttf
  MakeFace = true
  Placement = pos=(9.94,53.93,2) rot=(0,0,1;0rad)
  Size = 2.7
  String = Smart Water Pump
  Tracking = 0
FEATURE [Part::Part2DObjectPython] ShapeString007  # Draft 2D object (typed FeaturePython)
  FontFile = <userpath>/Documents/FreeCad/Fonts/Stencil_tenada/Tenada.ttf
  MakeFace = true
  Placement = pos=(32,42.9,2) rot=(0,0,1;0rad)
  Size = 2.5
  String = Controller S1
  Tracking = 0
FEATURE [PartDesign::Pocket] Pocket027
  BaseFeature = -> Pad058
  Direction = (0,0,-1)
  Length = 0.7
  Length2 = 5
  Profile = -> ShapeString006
  ReferenceAxis = -> ShapeString006 [N_Axis]
  Refine = true
  Type = 0
FEATURE [PartDesign::Pocket] Pocket028
  BaseFeature = -> Pocket027
  Direction = (0,0,-1)
  Length = 0.7
  Length2 = 5
  Profile = -> ShapeString007
  ReferenceAxis = -> ShapeString007 [N_Axis]
  Refine = true
  Type = 0
FEATURE [PartDesign::Boolean] Boolean
  BaseFeature = -> Pocket028
  Group = -> [Body002]
  Refine = true
  Type = 0
FEATURE [PartDesign::Pad] Pad059
  BaseFeature = -> Pad043
  Direction = (1,0,0)
  Length = 0.4
  Length2 = 10
  Profile = -> Pad043 [Face131]
  Refine = true
  Type = 0
FEATURE [PartDesign::Pocket] Pocket029
  BaseFeature = -> Pad059
  Direction = (1,0,0)
  Length = 0.4
  Length2 = 5
  Profile = -> Pad059 [Face126]
  Refine = true
  Type = 0
FEATURE [PartDesign::Pocket] Pocket030
  BaseFeature = -> Boolean
  Direction = (0,-1,0)
  Length = 1.85
  Length2 = 5
  Profile = -> Boolean [Face74]
  Refine = true
  Type = 0
FEATURE [PartDesign::Pad] Pad060
  BaseFeature = -> Pocket029
  Direction = (1,0,0)
  Length = 1.5
  Length2 = 10
  Profile = -> Pocket029 [Face127]
  Refine = true
  Type = 0
FEATURE [PartDesign::Pad] Pad061
  BaseFeature = -> Pocket030
  Direction = (0,0,-1)
  Length = 0.01
  Length2 = 10
  Profile = -> Pocket030 [Face40]
  Refine = true
  Type = 0
FEATURE [Part::Feature] Part__Feature  label="TopSilk"
  Placement = pos=(0,0,1.62005) rot=(0,0,1;0rad)
  shape: bbox 1.968 x 2.555 x 2e-07 mm, 1 faces, 0 solids (baked)
FEATURE [Part::Feature] Part__Feature001  label="TopSilk001"
  Placement = pos=(0,0,1.62005) rot=(0,0,1;0rad)
  shape: bbox 1.872 x 2.555 x 2e-07 mm, 1 faces, 0 solids (baked)
FEATURE [Part::Feature] Part__Feature002  label="TopSilk002"
  Placement = pos=(0,0,1.62005) rot=(0,0,1;0rad)
  shape: bbox 1.676 x 2.555 x 2e-07 mm, 1 faces, 0 solids (baked)
FEATURE [Part::Feature] Part__Feature003  label="TopSilk003"
  Placement = pos=(0,0,1.62005) rot=(0,0,1;0rad)
  shape: bbox 0.3 x 1.875 x 2e-07 mm, 1 faces, 0 solids (baked)
FEATURE [Part::Feature] Part__Feature004  label="TopSilk004"
  Placement = pos=(0,0,1.62005) rot=(0,0,1;0rad)
  shape: bbox 1.349 x 1.875 x 2e-07 mm, 1 faces, 0 solids (baked)
FEATURE [Part::Feature] Part__Feature005  label="TopSilk005"
  Placement = pos=(0,0,1.62005) rot=(0,0,1;0rad)
  shape: bbox 16.25 x 30.25 x 2e-07 mm, 1 faces, 0 solids (baked)
FEATURE [Part::Feature] Part__Feature006  label="TopSilk006"
  Placement = pos=(0,0,1.62005) rot=(0,0,1;0rad)
  shape: bbox 1.649 x 0.3 x 2e-07 mm, 1 faces, 0 solids (baked)
FEATURE [Part::Feature] Part__Feature007  label="TopSilk007"
  Placement = pos=(0,0,1.62005) rot=(0,0,1;0rad)
  shape: bbox 1.499 x 1.875 x 2e-07 mm, 1 faces, 0 solids (baked)
FEATURE [Part::Feature] Part__Feature008  label="TopSilk008"
  Placement = pos=(0,0,1.62005) rot=(0,0,1;0rad)
  shape: bbox 1.425 x 1.875 x 2e-07 mm, 1 faces, 0 solids (baked)
FEATURE [Part::Feature] Part__Feature009  label="TopSilk009"
  Placement = pos=(0,0,1.62005) rot=(0,0,1;0rad)
  shape: bbox 1.126 x 1.492 x 2e-07 mm, 1 faces, 0 solids (baked)
FEATURE [Part::Feature] Part__Feature010  label="TopSilk010"
  Placement = pos=(0,0,1.62005) rot=(0,0,1;0rad)
  shape: bbox 15.25 x 21.25 x 2e-07 mm, 1 faces, 0 solids (baked)
FEATURE [Part::Feature] Part__Feature011  label="TopSilk011"
  Placement = pos=(0,0,1.62005) rot=(0,0,1;0rad)
  shape: bbox 2.154 x 15.45 x 2e-07 mm, 1 faces, 0 solids (baked)
FEATURE [Part::Feature] Part__Feature012  label="TopSilk012"
  Placement = pos=(0,0,1.62005) rot=(0,0,1;0rad)
  shape: bbox 2.286 x 2.286 x 2e-07 mm, 1 faces, 0 solids (baked)
FEATURE [Part::Feature] Part__Feature013  label="TopSilk013"
  Placement = pos=(0,0,1.62005) rot=(0,0,1;0rad)
  shape: bbox 0.6985 x 2.794 x 2e-07 mm, 1 faces, 0 solids (baked)
FEATURE [Part::Feature] Part__Feature014  label="TopSilk014"
  Placement = pos=(0,0,1.62005) rot=(0,0,1;0rad)
  shape: bbox 2.154 x 15.45 x 2e-07 mm, 1 faces, 0 solids (baked)
FEATURE [Part::Feature] Part__Feature015  label="TopSilk015"
  Placement = pos=(0,0,1.62005) rot=(0,0,1;0rad)
  shape: bbox 0.9715 x 1.129 x 2e-07 mm, 1 faces, 0 solids (baked)
FEATURE [Part::Feature] Part__Feature016  label="TopSilk016"
  Placement = pos=(0,0,1.62005) rot=(0,0,1;0rad)
  shape: bbox 1.543 x 1.129 x 2e-07 mm, 1 faces, 0 solids (baked)
FEATURE [Part::Feature] Part__Feature017  label="TopSilk017"
  Placement = pos=(0,0,1.62005) rot=(0,0,1;0rad)
  shape: bbox 1.025 x 1.492 x 2e-07 mm, 1 faces, 0 solids (baked)
FEATURE [Part::Feature] Part__Feature018  label="TopSilk018"
  Placement = pos=(0,0,1.62005) rot=(0,0,1;0rad)
  shape: bbox 1.182 x 1.492 x 2e-07 mm, 1 faces, 0 solids (baked)
FEATURE [Part::Feature] Part__Feature019  label="TopSilk019"
  Placement = pos=(0,0,1.62005) rot=(0,0,1;0rad)
  shape: bbox 0.8166 x 1.492 x 2e-07 mm, 1 faces, 0 solids (baked)
FEATURE [Part::Feature] Part__Feature020  label="TopSilk020"
  Placement = pos=(0,0,1.62005) rot=(0,0,1;0rad)
  shape: bbox 0.8166 x 1.129 x 2e-07 mm, 1 faces, 0 solids (baked)
FEATURE [Part::Feature] Part__Feature021  label="TopSilk021"
  Placement = pos=(0,0,1.62005) rot=(0,0,1;0rad)
  shape: bbox 0.1524 x 1.013 x 2e-07 mm, 1 faces, 0 solids (baked)
FEATURE [Part::Feature] Part__Feature022  label="TopSilk022"
  Placement = pos=(0,0,1.62005) rot=(0,0,1;0rad)
  shape: bbox 1.158 x 0.823 x 2e-07 mm, 1 faces, 0 solids (baked)
FEATURE [Part::Feature] Part__Feature023  label="TopSilk023"
  Placement = pos=(0,0,1.62005) rot=(0,0,1;0rad)
  shape: bbox 1.158 x 0.9195 x 2e-07 mm, 1 faces, 0 solids (baked)
FEATURE [Part::Feature] Part__Feature024  label="TopSilk024"
  Placement = pos=(0,0,1.62005) rot=(0,0,1;0rad)
  shape: bbox 1.158 x 0.1524 x 2e-07 mm, 1 faces, 0 solids (baked)
FEATURE [Part::Feature] Part__Feature025  label="TopSilk025"
  Placement = pos=(0,0,1.62005) rot=(0,0,1;0rad)
  shape: bbox 1.158 x 0.878 x 2e-07 mm, 1 faces, 0 solids (baked)
FEATURE [Part::Feature] Part__Feature026  label="TopSilk026"
  Placement = pos=(0,0,1.62005) rot=(0,0,1;0rad)
  shape: bbox 1.233 x 1.492 x 2e-07 mm, 1 faces, 0 solids (baked)
FEATURE [Part::Feature] Part__Feature027  label="TopSilk027"
  Placement = pos=(0,0,1.62005) rot=(0,0,1;0rad)
  shape: bbox 1.13 x 1.492 x 2e-07 mm, 1 faces, 0 solids (baked)
FEATURE [Part::Feature] Part__Feature028  label="TopSilk028"
  Placement = pos=(0,0,1.62005) rot=(0,0,1;0rad)
  shape: bbox 0.5041 x 0.5016 x 2e-07 mm, 1 faces, 0 solids (baked)
FEATURE [Part::Feature] Part__Feature029  label="TopSilk029"
  Placement = pos=(0,0,1.62005) rot=(0,0,1;0rad)
  shape: bbox 1.132 x 1.495 x 2e-07 mm, 1 faces, 0 solids (baked)
FEATURE [Part::Feature] Part__Feature030  label="TopSilk030"
  Placement = pos=(0,0,1.62005) rot=(0,0,1;0rad)
  shape: bbox 0.8136 x 0.5867 x 2e-07 mm, 1 faces, 0 solids (baked)
FEATURE [Part::Feature] Part__Feature031  label="TopSilk031"
  Placement = pos=(0,0,1.62005) rot=(0,0,1;0rad)
  shape: bbox 0.8026 x 0.5842 x 2e-07 mm, 1 faces, 0 solids (baked)
FEATURE [Part::Feature] Part__Feature032  label="TopSilk032"
  Placement = pos=(0,0,1.62005) rot=(0,0,1;0rad)
  shape: bbox 0.8026 x 0.7696 x 2e-07 mm, 1 faces, 0 solids (baked)
FEATURE [Part::Feature] Part__Feature033  label="TopSilk033"
  Placement = pos=(0,0,1.62005) rot=(0,0,1;0rad)
  shape: bbox 5.764 x 21.24 x 2e-07 mm, 1 faces, 0 solids (baked)
FEATURE [Part::Feature] Part__Feature034  label="TopSilk034"
  Placement = pos=(0,0,1.62005) rot=(0,0,1;0rad)
  shape: bbox 1.158 x 0.8712 x 2e-07 mm, 1 faces, 0 solids (baked)
FEATURE [Part::Feature] Part__Feature035  label="TopSilk035"
  Placement = pos=(0,0,1.62005) rot=(0,0,1;0rad)
  shape: bbox 1.158 x 0.8687 x 2e-07 mm, 1 faces, 0 solids (baked)
FEATURE [Part::Feature] Part__Feature036  label="TopSilk036"
  Placement = pos=(0,0,1.62005) rot=(0,0,1;0rad)
  shape: bbox 3.596 x 8.555 x 2e-07 mm, 1 faces, 0 solids (baked)
FEATURE [Part::Feature] Part__Feature037  label="TopSilk037"
  Placement = pos=(0,0,1.62005) rot=(0,0,1;0rad)
  shape: bbox 0.8136 x 0.5842 x 2e-07 mm, 1 faces, 0 solids (baked)
FEATURE [Part::Feature] Part__Feature038  label="TopSilk038"
  Placement = pos=(0,0,1.62005) rot=(0,0,1;0rad)
  shape: bbox 0.8045 x 0.5842 x 2e-07 mm, 1 faces, 0 solids (baked)
FEATURE [Part::Feature] Part__Feature039  label="TopSilk039"
  Placement = pos=(0,0,1.62005) rot=(0,0,1;0rad)
  shape: bbox 0.8026 x 0.5537 x 2e-07 mm, 1 faces, 0 solids (baked)
FEATURE [Part::Feature] Part__Feature040  label="TopSilk040"
  Placement = pos=(0,0,1.62005) rot=(0,0,1;0rad)
  shape: bbox 0.8026 x 0.5537 x 2e-07 mm, 1 faces, 0 solids (baked)
FEATURE [Part::Feature] Part__Feature041  label="TopSilk041"
  Placement = pos=(0,0,1.62005) rot=(0,0,1;0rad)
  shape: bbox 20.57 x 34.8 x 2e-07 mm, 1 faces, 0 solids (baked)
FEATURE [Part::Feature] Part__Feature042  label="TopSilk042"
  Placement = pos=(0,0,1.62005) rot=(0,0,1;0rad)
  shape: bbox 3.596 x 8.555 x 2e-07 mm, 1 faces, 0 solids (baked)
FEATURE [Part::Feature] Part__Feature043  label="TopSilk043"
  Placement = pos=(0,0,1.62005) rot=(0,0,1;0rad)
  shape: bbox 1.158 x 0.3912 x 2e-07 mm, 1 faces, 0 solids (baked)
FEATURE [Part::Feature] Part__Feature044  label="TopSilk044"
  Placement = pos=(0,0,1.62005) rot=(0,0,1;0rad)
  shape: bbox 1.158 x 0.8712 x 2e-07 mm, 1 faces, 0 solids (baked)
FEATURE [Part::Feature] Part__Feature045  label="TopSilk045"
  Placement = pos=(0,0,1.62005) rot=(0,0,1;0rad)
  shape: bbox 1.66 x 0.996 x 2e-07 mm, 1 faces, 0 solids (baked)
FEATURE [Part::Feature] Part__Feature046  label="TopSilk046"
  Placement = pos=(0,0,1.62005) rot=(0,0,1;0rad)
  shape: bbox 0.249 x 0.996 x 2e-07 mm, 1 faces, 0 solids (baked)
FEATURE [Part::Feature] Part__Feature047  label="TopSilk047"
  Placement = pos=(0,0,1.62005) rot=(0,0,1;0rad)
  shape: bbox 2.338 x 1.79 x 2e-07 mm, 1 faces, 0 solids (baked)
FEATURE [Part::Feature] Part__Feature048  label="TopSilk048"
  Placement = pos=(0,0,1.62005) rot=(0,0,1;0rad)
  shape: bbox 2.338 x 1.79 x 2e-07 mm, 1 faces, 0 solids (baked)
FEATURE [Part::Feature] Part__Feature049  label="TopSilk049"
  Placement = pos=(0,0,1.62005) rot=(0,0,1;0rad)
  shape: bbox 10.83 x 2.794 x 2e-07 mm, 1 faces, 0 solids (baked)
FEATURE [Part::Feature] Part__Feature050  label="TopSilk050"
  Placement = pos=(0,0,1.62005) rot=(0,0,1;0rad)
  shape: bbox 1.136 x 1.555 x 2e-07 mm, 1 faces, 0 solids (baked)
FEATURE [Part::Feature] Part__Feature051  label="TopSilk051"
  Placement = pos=(0,0,1.62005) rot=(0,0,1;0rad)
  shape: bbox 0.8704 x 1.15 x 2e-07 mm, 1 faces, 0 solids (baked)
FEATURE [Part::Feature] Part__Feature052  label="TopSilk052"
  Placement = pos=(0,0,1.62005) rot=(0,0,1;0rad)
  shape: bbox 0.823 x 1.158 x 2e-07 mm, 1 faces, 0 solids (baked)
FEATURE [Part::Feature] Part__Feature053  label="TopSilk053"
  Placement = pos=(0,0,1.62005) rot=(0,0,1;0rad)
  shape: bbox 1.095 x 1.15 x 2e-07 mm, 1 faces, 0 solids (baked)
FEATURE [Part::Feature] Part__Feature054  label="TopSilk054"
  Placement = pos=(0,0,1.62005) rot=(0,0,1;0rad)
  shape: bbox 0.7539 x 0.7539 x 2e-07 mm, 1 faces, 0 solids (baked)
FEATURE [Part::Feature] Part__Feature055  label="TopSilk055"
  Placement = pos=(0,0,1.62005) rot=(0,0,1;0rad)
  shape: bbox 0.8712 x 1.158 x 2e-07 mm, 1 faces, 0 solids (baked)
FEATURE [Part::Feature] Part__Feature056  label="TopSilk056"
  Placement = pos=(0,0,1.62005) rot=(0,0,1;0rad)
  shape: bbox 0.823 x 1.158 x 2e-07 mm, 1 faces, 0 solids (baked)
FEATURE [Part::Feature] Part__Feature057  label="TopSilk057"
  Placement = pos=(0,0,1.62005) rot=(0,0,1;0rad)
  shape: bbox 0.823 x 1.158 x 2e-07 mm, 1 faces, 0 solids (baked)
FEATURE [Part::Feature] Part__Feature058  label="TopSilk058"
  Placement = pos=(0,0,1.62005) rot=(0,0,1;0rad)
  shape: bbox 0.8704 x 1.15 x 2e-07 mm, 1 faces, 0 solids (baked)
FEATURE [Part::Feature] Part__Feature059  label="TopSilk059"
  Placement = pos=(0,0,1.62005) rot=(0,0,1;0rad)
  shape: bbox 13.65 x 12.95 x 2e-07 mm, 1 faces, 0 solids (baked)
FEATURE [Part::Feature] Part__Feature060  label="TopSilk060"
  Placement = pos=(0,0,1.62005) rot=(0,0,1;0rad)
  shape: bbox 1.095 x 1.15 x 2e-07 mm, 1 faces, 0 solids (baked)
FEATURE [Part::Feature] Part__Feature061  label="TopSilk061"
  Placement = pos=(0,0,1.62005) rot=(0,0,1;0rad)
  shape: bbox 0.878 x 1.158 x 2e-07 mm, 1 faces, 0 solids (baked)
FEATURE [Part::Feature] Part__Feature062  label="TopSilk062"
  Placement = pos=(0,0,1.62005) rot=(0,0,1;0rad)
  shape: bbox 1.197 x 1.555 x 2e-07 mm, 1 faces, 0 solids (baked)
FEATURE [Part::Feature] Part__Feature063  label="TopSilk063"
  Placement = pos=(0,0,1.62005) rot=(0,0,1;0rad)
  shape: bbox 0.823 x 1.158 x 2e-07 mm, 1 faces, 0 solids (baked)
FEATURE [Part::Feature] Part__Feature064  label="TopSilk064"
  Placement = pos=(0,0,1.62005) rot=(0,0,1;0rad)
  shape: bbox 0.823 x 1.158 x 2e-07 mm, 1 faces, 0 solids (baked)
FEATURE [Part::Feature] Part__Feature065  label="TopSilk065"
  Placement = pos=(0,0,1.62005) rot=(0,0,1;0rad)
  shape: bbox 0.7747 x 1.158 x 2e-07 mm, 1 faces, 0 solids (baked)
FEATURE [Part::Feature] Part__Feature066  label="TopSilk066"
  Placement = pos=(0,0,1.62005) rot=(0,0,1;0rad)
  shape: bbox 1.139 x 1.562 x 2e-07 mm, 1 faces, 0 solids (baked)
FEATURE [Part::Feature] Part__Feature067  label="TopSilk067"
  Placement = pos=(0,0,1.62005) rot=(0,0,1;0rad)
  shape: bbox 0.7747 x 1.158 x 2e-07 mm, 1 faces, 0 solids (baked)
FEATURE [Part::Feature] Part__Feature068  label="TopSilk068"
  Placement = pos=(0,0,1.62005) rot=(0,0,1;0rad)
  shape: bbox 0.823 x 1.158 x 2e-07 mm, 1 faces, 0 solids (baked)
FEATURE [Part::Feature] Part__Feature069  label="TopSilk069"
  Placement = pos=(0,0,1.62005) rot=(0,0,1;0rad)
  shape: bbox 1.197 x 1.555 x 2e-07 mm, 1 faces, 0 solids (baked)
FEATURE [Part::Feature] Part__Feature070  label="TopSilk070"
  Placement = pos=(0,0,1.62005) rot=(0,0,1;0rad)
  shape: bbox 0.823 x 1.158 x 2e-07 mm, 1 faces, 0 solids (baked)
FEATURE [Part::Feature] Part__Feature071  label="TopSilk071"
  Placement = pos=(0,0,1.62005) rot=(0,0,1;0rad)
  shape: bbox 0.823 x 1.158 x 2e-07 mm, 1 faces, 0 solids (baked)
FEATURE [Part::Feature] Part__Feature072  label="TopSilk072"
  Placement = pos=(0,0,1.62005) rot=(0,0,1;0rad)
  shape: bbox 2.252 x 0.2719 x 2e-07 mm, 1 faces, 0 solids (baked)
FEATURE [Part::Feature] Part__Feature073  label="TopSilk073"
  Placement = pos=(0,0,1.62005) rot=(0,0,1;0rad)
  shape: bbox 2.252 x 0.2719 x 2e-07 mm, 1 faces, 0 solids (baked)
FEATURE [Part::Feature] Part__Feature074  label="TopSilk074"
  Placement = pos=(0,0,1.62005) rot=(0,0,1;0rad)
  shape: bbox 0.5867 x 0.8026 x 2e-07 mm, 1 faces, 0 solids (baked)
FEATURE [Part::Feature] Part__Feature075  label="TopSilk075"
  Placement = pos=(0,0,1.62005) rot=(0,0,1;0rad)
  shape: bbox 0.5867 x 0.8026 x 2e-07 mm, 1 faces, 0 solids (baked)
FEATURE [Part::Feature] Part__Feature076  label="TopSilk076"
  Placement = pos=(0,0,1.62005) rot=(0,0,1;0rad)
  shape: bbox 0.7 x 0.8 x 2e-07 mm, 1 faces, 0 solids (baked)
FEATURE [Part::Feature] Part__Feature077  label="TopSilk077"
  Placement = pos=(0,0,1.62005) rot=(0,0,1;0rad)
  shape: bbox 0.5842 x 0.8026 x 2e-07 mm, 1 faces, 0 solids (baked)
FEATURE [Part::Feature] Part__Feature078  label="TopSilk078"
  Placement = pos=(0,0,1.62005) rot=(0,0,1;0rad)
  shape: bbox 4.357 x 0.8104 x 2e-07 mm, 1 faces, 0 solids (baked)
FEATURE [Part::Feature] Part__Feature079  label="TopSilk079"
  Placement = pos=(0,0,1.62005) rot=(0,0,1;0rad)
  shape: bbox 4.357 x 0.8104 x 2e-07 mm, 1 faces, 0 solids (baked)
FEATURE [Part::Feature] Part__Feature080  label="TopSilk080"
  Placement = pos=(0,0,1.62005) rot=(0,0,1;0rad)
  shape: bbox 0.6563 x 0.8026 x 2e-07 mm, 1 faces, 0 solids (baked)
FEATURE [Part::Feature] Part__Feature081  label="TopSilk081"
  Placement = pos=(0,0,1.62005) rot=(0,0,1;0rad)
  shape: bbox 1.276 x 2.074 x 2e-07 mm, 1 faces, 0 solids (baked)
FEATURE [Part::Feature] Part__Feature082  label="TopSilk082"
  Placement = pos=(0,0,1.62005) rot=(0,0,1;0rad)
  shape: bbox 0.6563 x 0.8026 x 2e-07 mm, 1 faces, 0 solids (baked)
FEATURE [Part::Feature] Part__Feature083  label="TopSilk083"
  Placement = pos=(0,0,1.62005) rot=(0,0,1;0rad)
  shape: bbox 2.054 x 2.054 x 2e-07 mm, 1 faces, 0 solids (baked)
FEATURE [Part::Feature] Part__Feature084  label="TopSilk084"
  Placement = pos=(0,0,1.62005) rot=(0,0,1;0rad)
  shape: bbox 0.5842 x 0.8026 x 2e-07 mm, 1 faces, 0 solids (baked)
FEATURE [Part::Feature] Part__Feature085  label="TopSilk085"
  Placement = pos=(0,0,1.62005) rot=(0,0,1;0rad)
  shape: bbox 1.038 x 2.074 x 2e-07 mm, 1 faces, 0 solids (baked)
FEATURE [Part::Feature] Part__Feature086  label="TopSilk086"
  Placement = pos=(0,0,1.62005) rot=(0,0,1;0rad)
  shape: bbox 20.46 x 15.85 x 2e-07 mm, 1 faces, 0 solids (baked)
FEATURE [Part::Feature] Part__Feature087  label="TopSilk087"
  Placement = pos=(0,0,1.62005) rot=(0,0,1;0rad)
  shape: bbox 0.1524 x 1.013 x 2e-07 mm, 1 faces, 0 solids (baked)
FEATURE [Part::Feature] Part__Feature088  label="TopSilk088"
  Placement = pos=(0,0,1.62005) rot=(0,0,1;0rad)
  shape: bbox 0.1524 x 1.013 x 2e-07 mm, 1 faces, 0 solids (baked)
FEATURE [Part::Feature] Part__Feature089  label="TopSilk089"
  Placement = pos=(0,0,1.62005) rot=(0,0,1;0rad)
  shape: bbox 1.038 x 2.074 x 2e-07 mm, 1 faces, 0 solids (baked)
FEATURE [Part::Feature] Part__Feature090  label="TopSilk090"
  Placement = pos=(0,0,1.62005) rot=(0,0,1;0rad)
  shape: bbox 0.5867 x 0.8026 x 2e-07 mm, 1 faces, 0 solids (baked)
FEATURE [Part::Feature] Part__Feature091  label="TopSilk091"
  Placement = pos=(0,0,1.62005) rot=(0,0,1;0rad)
  shape: bbox 0.5867 x 0.8026 x 2e-07 mm, 1 faces, 0 solids (baked)
FEATURE [Part::Feature] Part__Feature092  label="TopSilk092"
  Placement = pos=(0,0,1.62005) rot=(0,0,1;0rad)
  shape: bbox 0.254 x 1.016 x 2e-07 mm, 1 faces, 0 solids (baked)
FEATURE [Part::Feature] Part__Feature093  label="TopSilk093"
  Placement = pos=(0,0,1.62005) rot=(0,0,1;0rad)
  shape: bbox 0.3048 x 0.8026 x 2e-07 mm, 1 faces, 0 solids (baked)
FEATURE [Part::Feature] Part__Feature094  label="TopSilk094"
  Placement = pos=(0,0,1.62005) rot=(0,0,1;0rad)
  shape: bbox 1.254 x 1.254 x 2e-07 mm, 1 faces, 0 solids (baked)
FEATURE [Part::Feature] Part__Feature095  label="TopSilk095"
  Placement = pos=(0,0,1.62005) rot=(0,0,1;0rad)
  shape: bbox 1.651 x 0.2541 x 2e-07 mm, 1 faces, 0 solids (baked)
FEATURE [Part::Feature] Part__Feature096  label="TopSilk096"
  Placement = pos=(0,0,1.62005) rot=(0,0,1;0rad)
  shape: bbox 0.3048 x 0.8026 x 2e-07 mm, 1 faces, 0 solids (baked)
FEATURE [Part::Feature] Part__Feature097  label="TopSilk097"
  Placement = pos=(0,0,1.62005) rot=(0,0,1;0rad)
  shape: bbox 1.099 x 0.254 x 2e-07 mm, 1 faces, 0 solids (baked)
FEATURE [Part::Feature] Part__Feature098  label="TopSilk098"
  Placement = pos=(0,0,1.62005) rot=(0,0,1;0rad)
  shape: bbox 1.355 x 2.071 x 2e-07 mm, 1 faces, 0 solids (baked)
FEATURE [Part::Feature] Part__Feature099  label="TopSilk099"
  Placement = pos=(0,0,1.62005) rot=(0,0,1;0rad)
  shape: bbox 15.13 x 12.3 x 2e-07 mm, 1 faces, 0 solids (baked)
FEATURE [Part::Feature] Part__Feature100  label="TopSilk100"
  Placement = pos=(0,0,1.62005) rot=(0,0,1;0rad)
  shape: bbox 1.276 x 1.515 x 2e-07 mm, 1 faces, 0 solids (baked)
FEATURE [Part::Feature] Part__Feature101  label="TopSilk101"
  Placement = pos=(0,0,1.62005) rot=(0,0,1;0rad)
  shape: bbox 0.56 x 1.119 x 2e-07 mm, 1 faces, 0 solids (baked)
FEATURE [Part::Feature] Part__Feature102  label="TopSilk102"
  Placement = pos=(0,0,1.62005) rot=(0,0,1;0rad)
  shape: bbox 1.158 x 0.8712 x 2e-07 mm, 1 faces, 0 solids (baked)
FEATURE [Part::Feature] Part__Feature103  label="TopSilk103"
  Placement = pos=(0,0,1.62005) rot=(0,0,1;0rad)
  shape: bbox 1.158 x 0.823 x 2e-07 mm, 1 faces, 0 solids (baked)
FEATURE [Part::Feature] Part__Feature104  label="TopSilk104"
  Placement = pos=(0,0,1.62005) rot=(0,0,1;0rad)
  shape: bbox 3.418 x 1.587 x 2e-07 mm, 1 faces, 0 solids (baked)
FEATURE [Part::Feature] Part__Feature105  label="TopSilk105"
  Placement = pos=(0,0,1.62005) rot=(0,0,1;0rad)
  shape: bbox 3.418 x 1.587 x 2e-07 mm, 1 faces, 0 solids (baked)
FEATURE [Part::Feature] Part__Feature106  label="TopSilk106"
  Placement = pos=(0,0,1.62005) rot=(0,0,1;0rad)
  shape: bbox 1.835 x 2.948 x 2e-07 mm, 1 faces, 0 solids (baked)
FEATURE [Part::Feature] Part__Feature107  label="TopSilk107"
  Placement = pos=(0,0,1.62005) rot=(0,0,1;0rad)
  shape: bbox 2.338 x 1.79 x 2e-07 mm, 1 faces, 0 solids (baked)
FEATURE [Part::Feature] Part__Feature108  label="TopSilk108"
  Placement = pos=(0,0,1.62005) rot=(0,0,1;0rad)
  shape: bbox 2.338 x 1.79 x 2e-07 mm, 1 faces, 0 solids (baked)
FEATURE [Part::Feature] Part__Feature109  label="TopSilk109"
  Placement = pos=(0,0,1.62005) rot=(0,0,1;0rad)
  shape: bbox 0.5867 x 0.8026 x 2e-07 mm, 1 faces, 0 solids (baked)
FEATURE [Part::Feature] Part__Feature110  label="TopSilk110"
  Placement = pos=(0,0,1.62005) rot=(0,0,1;0rad)
  shape: bbox 1.474 x 1.111 x 2e-07 mm, 1 faces, 0 solids (baked)
FEATURE [Part::Feature] Part__Feature111  label="TopSilk111"
  Placement = pos=(0,0,1.62005) rot=(0,0,1;0rad)
  shape: bbox 1.474 x 1.111 x 2e-07 mm, 1 faces, 0 solids (baked)
FEATURE [Part::Feature] Part__Feature112  label="TopSilk112"
  Placement = pos=(0,0,1.62005) rot=(0,0,1;0rad)
  shape: bbox 9.326 x 1.876 x 2e-07 mm, 1 faces, 0 solids (baked)
FEATURE [Part::Feature] Part__Feature113  label="TopSilk113"
  Placement = pos=(0,0,1.62005) rot=(0,0,1;0rad)
  shape: bbox 0.254 x 2.242 x 2e-07 mm, 1 faces, 0 solids (baked)
FEATURE [Part::Feature] Part__Feature114  label="TopSilk114"
  Placement = pos=(0,0,1.62005) rot=(0,0,1;0rad)
  shape: bbox 1.835 x 2.948 x 2e-07 mm, 1 faces, 0 solids (baked)
FEATURE [Part::Feature] Part__Feature115  label="TopSilk115"
  Placement = pos=(0,0,1.62005) rot=(0,0,1;0rad)
  shape: bbox 0.8136 x 0.5842 x 2e-07 mm, 1 faces, 0 solids (baked)
FEATURE [Part::Feature] Part__Feature116  label="TopSilk116"
  Placement = pos=(0,0,1.62005) rot=(0,0,1;0rad)
  shape: bbox 0.8026 x 0.5867 x 2e-07 mm, 1 faces, 0 solids (baked)
FEATURE [Part::Feature] Part__Feature117  label="TopSilk117"
  Placement = pos=(0,0,1.62005) rot=(0,0,1;0rad)
  shape: bbox 0.5842 x 0.8136 x 2e-07 mm, 1 faces, 0 solids (baked)
FEATURE [Part::Feature] Part__Feature118  label="TopSilk118"
  Placement = pos=(0,0,1.62005) rot=(0,0,1;0rad)
  shape: bbox 0.5842 x 0.8026 x 2e-07 mm, 1 faces, 0 solids (baked)
FEATURE [Part::Feature] Part__Feature119  label="TopSilk119"
  Placement = pos=(0,0,1.62005) rot=(0,0,1;0rad)
  shape: bbox 1.158 x 0.823 x 2e-07 mm, 1 faces, 0 solids (baked)
FEATURE [Part::Feature] Part__Feature120  label="TopSilk120"
  Placement = pos=(0,0,1.62005) rot=(0,0,1;0rad)
  shape: bbox 1.158 x 0.823 x 2e-07 mm, 1 faces, 0 solids (baked)
FEATURE [Part::Feature] Part__Feature121  label="TopSilk121"
  Placement = pos=(0,0,1.62005) rot=(0,0,1;0rad)
  shape: bbox 1.474 x 1.067 x 2e-07 mm, 1 faces, 0 solids (baked)
FEATURE [Part::Feature] Part__Feature122  label="TopSilk122"
  Placement = pos=(0,0,1.62005) rot=(0,0,1;0rad)
  shape: bbox 1.474 x 1.066 x 2e-07 mm, 1 faces, 0 solids (baked)
FEATURE [Part::Feature] Part__Feature123  label="TopSilk123"
  Placement = pos=(0,0,1.62005) rot=(0,0,1;0rad)
  shape: bbox 0.5842 x 0.8026 x 2e-07 mm, 1 faces, 0 solids (baked)
FEATURE [Part::Feature] Part__Feature124  label="TopSilk124"
  Placement = pos=(0,0,1.62005) rot=(0,0,1;0rad)
  shape: bbox 0.8026 x 0.5232 x 2e-07 mm, 1 faces, 0 solids (baked)
FEATURE [Part::Feature] Part__Feature125  label="TopSilk125"
  Placement = pos=(0,0,1.62005) rot=(0,0,1;0rad)
  shape: bbox 0.8026 x 0.3048 x 2e-07 mm, 1 faces, 0 solids (baked)
FEATURE [Part::Feature] Part__Feature126  label="TopSilk126"
  Placement = pos=(0,0,1.62005) rot=(0,0,1;0rad)
  shape: bbox 1.675 x 1.515 x 2e-07 mm, 1 faces, 0 solids (baked)
FEATURE [Part::Feature] Part__Feature127  label="TopSilk127"
  Placement = pos=(0,0,1.62005) rot=(0,0,1;0rad)
  shape: bbox 1.158 x 0.3912 x 2e-07 mm, 1 faces, 0 solids (baked)
FEATURE [Part::Feature] Part__Feature128  label="TopSilk128"
  Placement = pos=(0,0,1.62005) rot=(0,0,1;0rad)
  shape: bbox 1.158 x 0.823 x 2e-07 mm, 1 faces, 0 solids (baked)
FEATURE [Part::Feature] Part__Feature129  label="TopSilk129"
  Placement = pos=(0,0,1.62005) rot=(0,0,1;0rad)
  shape: bbox 1.474 x 1.066 x 2e-07 mm, 1 faces, 0 solids (baked)
FEATURE [Part::Feature] Part__Feature130  label="TopSilk130"
  Placement = pos=(0,0,1.62005) rot=(0,0,1;0rad)
  shape: bbox 1.474 x 1.067 x 2e-07 mm, 1 faces, 0 solids (baked)
FEATURE [Part::Feature] Part__Feature131  label="TopSilk131"
  Placement = pos=(0,0,1.62005) rot=(0,0,1;0rad)
  shape: bbox 0.8026 x 0.5232 x 2e-07 mm, 1 faces, 0 solids (baked)
FEATURE [Part::Feature] Part__Feature132  label="TopSilk132"
  Placement = pos=(0,0,1.62005) rot=(0,0,1;0rad)
  shape: bbox 0.8026 x 0.5842 x 2e-07 mm, 1 faces, 0 solids (baked)
FEATURE [Part::Feature] Part__Feature133  label="TopSilk133"
  Placement = pos=(0,0,1.62005) rot=(0,0,1;0rad)
  shape: bbox 1.355 x 1.515 x 2e-07 mm, 1 faces, 0 solids (baked)
FEATURE [Part::Feature] Part__Feature134  label="TopSilk134"
  Placement = pos=(0,0,1.62005) rot=(0,0,1;0rad)
  shape: bbox 1.805 x 1.836 x 2e-07 mm, 1 faces, 0 solids (baked)
FEATURE [Part::Feature] Part__Feature135  label="TopSilk135"
  Placement = pos=(0,0,1.62005) rot=(0,0,1;0rad)
  shape: bbox 1.158 x 0.8712 x 2e-07 mm, 1 faces, 0 solids (baked)
FEATURE [Part::Feature] Part__Feature136  label="TopSilk136"
  Placement = pos=(0,0,1.62005) rot=(0,0,1;0rad)
  shape: bbox 1.158 x 0.823 x 2e-07 mm, 1 faces, 0 solids (baked)
FEATURE [Part::Feature] Part__Feature137  label="TopSilk137"
  Placement = pos=(0,0,1.62005) rot=(0,0,1;0rad)
  shape: bbox 1.474 x 1.111 x 2e-07 mm, 1 faces, 0 solids (baked)
FEATURE [Part::Feature] Part__Feature138  label="TopSilk138"
  Placement = pos=(0,0,1.62005) rot=(0,0,1;0rad)
  shape: bbox 1.474 x 1.111 x 2e-07 mm, 1 faces, 0 solids (baked)
FEATURE [Part::Feature] Part__Feature139  label="TopSilk139"
  Placement = pos=(0,0,1.62005) rot=(0,0,1;0rad)
  shape: bbox 1.038 x 2.074 x 2e-07 mm, 1 faces, 0 solids (baked)
FEATURE [Part::Feature] Part__Feature140  label="TopSilk140"
  Placement = pos=(0,0,1.62005) rot=(0,0,1;0rad)
  shape: bbox 3.596 x 8.555 x 2e-07 mm, 1 faces, 0 solids (baked)
FEATURE [Part::Feature] Part__Feature141  label="TopSilk141"
  Placement = pos=(0,0,1.62005) rot=(0,0,1;0rad)
  shape: bbox 0.8026 x 0.5867 x 2e-07 mm, 1 faces, 0 solids (baked)
FEATURE [Part::Feature] Part__Feature142  label="TopSilk142"
  Placement = pos=(0,0,1.62005) rot=(0,0,1;0rad)
  shape: bbox 0.8026 x 0.5582 x 2e-07 mm, 1 faces, 0 solids (baked)
FEATURE [Part::Feature] Part__Feature143  label="TopSilk143"
  Placement = pos=(0,0,1.62005) rot=(0,0,1;0rad)
  shape: bbox 1.355 x 1.515 x 2e-07 mm, 1 faces, 0 solids (baked)
FEATURE [Part::Feature] Part__Feature144  label="TopSilk144"
  Placement = pos=(0,0,1.62005) rot=(0,0,1;0rad)
  shape: bbox 0.254 x 2.482 x 2e-07 mm, 1 faces, 0 solids (baked)
FEATURE [Part::Feature] Part__Feature145  label="TopSilk145"
  Placement = pos=(0,0,1.62005) rot=(0,0,1;0rad)
  shape: bbox 0.3 x 4.245 x 2e-07 mm, 1 faces, 0 solids (baked)
FEATURE [Part::Feature] Part__Feature146  label="TopSilk146"
  Placement = pos=(0,0,1.62005) rot=(0,0,1;0rad)
  shape: bbox 0.254 x 2.248 x 2e-07 mm, 1 faces, 0 solids (baked)
FEATURE [Part::Feature] Part__Feature147  label="TopSilk147"
  Placement = pos=(0,0,1.62005) rot=(0,0,1;0rad)
  shape: bbox 1.038 x 1.515 x 2e-07 mm, 1 faces, 0 solids (baked)
FEATURE [Part::Feature] Part__Feature148  label="TopSilk148"
  Placement = pos=(0,0,1.62005) rot=(0,0,1;0rad)
  shape: bbox 0.8026 x 0.3048 x 2e-07 mm, 1 faces, 0 solids (baked)
FEATURE [Part::Feature] Part__Feature149  label="TopSilk149"
  Placement = pos=(0,0,1.62005) rot=(0,0,1;0rad)
  shape: bbox 0.8026 x 0.5867 x 2e-07 mm, 1 faces, 0 solids (baked)
FEATURE [Part::Feature] Part__Feature150  label="TopSilk150"
  Placement = pos=(0,0,1.62005) rot=(0,0,1;0rad)
  shape: bbox 0.8026 x 0.3048 x 2e-07 mm, 1 faces, 0 solids (baked)
FEATURE [Part::Feature] Part__Feature151  label="TopSilk151"
  Placement = pos=(0,0,1.62005) rot=(0,0,1;0rad)
  shape: bbox 3.418 x 1.587 x 2e-07 mm, 1 faces, 0 solids (baked)
FEATURE [Part::Feature] Part__Feature152  label="TopSilk152"
  Placement = pos=(0,0,1.62005) rot=(0,0,1;0rad)
  shape: bbox 3.418 x 1.587 x 2e-07 mm, 1 faces, 0 solids (baked)
FEATURE [Part::Feature] Part__Feature153  label="TopSilk153"
  Placement = pos=(0,0,1.62005) rot=(0,0,1;0rad)
  shape: bbox 0.4 x 2.074 x 2e-07 mm, 1 faces, 0 solids (baked)
FEATURE [Part::Feature] Part__Feature154  label="TopSilk154"
  Placement = pos=(0,0,1.62005) rot=(0,0,1;0rad)
  shape: bbox 3.596 x 8.555 x 2e-07 mm, 1 faces, 0 solids (baked)
FEATURE [Part::Feature] Part__Feature155  label="TopSilk155"
  Placement = pos=(0,0,1.62005) rot=(0,0,1;0rad)
  shape: bbox 1.355 x 1.515 x 2e-07 mm, 1 faces, 0 solids (baked)
FEATURE [Part::Feature] Part__Feature156  label="TopSilk156"
  Placement = pos=(0,0,1.62005) rot=(0,0,1;0rad)
  shape: bbox 1.66 x 0.996 x 2e-07 mm, 1 faces, 0 solids (baked)
FEATURE [Part::Feature] Part__Feature157  label="TopSilk157"
  Placement = pos=(0,0,1.62005) rot=(0,0,1;0rad)
  shape: bbox 0.9195 x 1.255 x 2e-07 mm, 1 faces, 0 solids (baked)
FEATURE [Part::Feature] Part__Feature158  label="TopSilk158"
  Placement = pos=(0,0,1.62005) rot=(0,0,1;0rad)
  shape: bbox 1.87 x 1.184 x 2e-07 mm, 1 faces, 0 solids (baked)
FEATURE [Part::Feature] Part__Feature159  label="TopSilk159"
  Placement = pos=(0,0,1.62005) rot=(0,0,1;0rad)
  shape: bbox 1.87 x 1.184 x 2e-07 mm, 1 faces, 0 solids (baked)
FEATURE [Part::Feature] Part__Feature160  label="TopSilk160"
  Placement = pos=(0,0,1.62005) rot=(0,0,1;0rad)
  shape: bbox 0.1524 x 1.063 x 2e-07 mm, 1 faces, 0 solids (baked)
FEATURE [Part::Feature] Part__Feature161  label="TopSilk161"
  Placement = pos=(0,0,1.62005) rot=(0,0,1;0rad)
  shape: bbox 0.249 x 0.996 x 2e-07 mm, 1 faces, 0 solids (baked)
FEATURE [Part::Feature] Part__Feature162  label="TopSilk162"
  Placement = pos=(0,0,1.62005) rot=(0,0,1;0rad)
  shape: bbox 0.6235 x 0.8026 x 2e-07 mm, 1 faces, 0 solids (baked)
FEATURE [Part::Feature] Part__Feature163  label="TopSilk163"
  Placement = pos=(0,0,1.62005) rot=(0,0,1;0rad)
  shape: bbox 1.364 x 1.674 x 2e-07 mm, 1 faces, 0 solids (baked)
FEATURE [Part::Feature] Part__Feature164  label="TopSilk164"
  Placement = pos=(0,0,1.62005) rot=(0,0,1;0rad)
  shape: bbox 0.3912 x 1.158 x 2e-07 mm, 1 faces, 0 solids (baked)
FEATURE [Part::Feature] Part__Feature165  label="TopSilk165"
  Placement = pos=(0,0,1.62005) rot=(0,0,1;0rad)
  shape: bbox 1.355 x 1.515 x 2e-07 mm, 1 faces, 0 solids (baked)
FEATURE [Part::Feature] Part__Feature166  label="TopSilk166"
  Placement = pos=(0,0,1.62005) rot=(0,0,1;0rad)
  shape: bbox 0.5583 x 0.8045 x 2e-07 mm, 1 faces, 0 solids (baked)
FEATURE [Part::Feature] Part__Feature167  label="TopSilk167"
  Placement = pos=(0,0,1.62005) rot=(0,0,1;0rad)
  shape: bbox 1.158 x 0.9195 x 2e-07 mm, 1 faces, 0 solids (baked)
FEATURE [Part::Feature] Part__Feature168  label="TopSilk168"
  Placement = pos=(0,0,1.62005) rot=(0,0,1;0rad)
  shape: bbox 1.158 x 0.878 x 2e-07 mm, 1 faces, 0 solids (baked)
FEATURE [Part::Feature] Part__Feature169  label="TopSilk169"
  Placement = pos=(0,0,1.62005) rot=(0,0,1;0rad)
  shape: bbox 1.158 x 0.9263 x 2e-07 mm, 1 faces, 0 solids (baked)
FEATURE [Part::Feature] Part__Feature170  label="TopSilk170"
  Placement = pos=(0,0,1.62005) rot=(0,0,1;0rad)
  shape: bbox 1.158 x 0.823 x 2e-07 mm, 1 faces, 0 solids (baked)
FEATURE [Part::Feature] Part__Feature171  label="TopSilk171"
  Placement = pos=(0,0,1.62005) rot=(0,0,1;0rad)
  shape: bbox 1.158 x 0.823 x 2e-07 mm, 1 faces, 0 solids (baked)
FEATURE [Part::Feature] Part__Feature172  label="TopSilk172"
  Placement = pos=(0,0,1.62005) rot=(0,0,1;0rad)
  shape: bbox 1.364 x 1.674 x 2e-07 mm, 1 faces, 0 solids (baked)
FEATURE [Part::Feature] Part__Feature173  label="TopSilk173"
  Placement = pos=(0,0,1.62005) rot=(0,0,1;0rad)
  shape: bbox 1.355 x 1.515 x 2e-07 mm, 1 faces, 0 solids (baked)
FEATURE [Part::Feature] Part__Feature174  label="TopSilk174"
  Placement = pos=(0,0,1.62005) rot=(0,0,1;0rad)
  shape: bbox 0.1524 x 1.013 x 2e-07 mm, 1 faces, 0 solids (baked)
FEATURE [Part::Feature] Part__Feature175  label="TopSilk175"
  Placement = pos=(0,0,1.62005) rot=(0,0,1;0rad)
  shape: bbox 16.25 x 30.25 x 2e-07 mm, 1 faces, 0 solids (baked)
FEATURE [Part::Feature] Part__Feature176  label="TopSilk176"
  Placement = pos=(0,0,1.62005) rot=(0,0,1;0rad)
  shape: bbox 0.4 x 2.074 x 2e-07 mm, 1 faces, 0 solids (baked)
FEATURE [Part::Feature] Part__Feature177  label="TopSilk177"
  Placement = pos=(0,0,1.62005) rot=(0,0,1;0rad)
  shape: bbox 0.5867 x 0.8026 x 2e-07 mm, 1 faces, 0 solids (baked)
FEATURE [Part::Feature] Part__Feature178  label="TopSilk178"
  Placement = pos=(0,0,1.62005) rot=(0,0,1;0rad)
  shape: bbox 1.587 x 3.418 x 2e-07 mm, 1 faces, 0 solids (baked)
FEATURE [Part::Feature] Part__Feature179  label="TopSilk179"
  Placement = pos=(0,0,1.62005) rot=(0,0,1;0rad)
  shape: bbox 0.56 x 0.56 x 2e-07 mm, 1 faces, 0 solids (baked)
FEATURE [Part::Feature] Part__Feature180  label="TopSilk180"
  Placement = pos=(0,0,1.62005) rot=(0,0,1;0rad)
  shape: bbox 1.158 x 0.823 x 2e-07 mm, 1 faces, 0 solids (baked)
FEATURE [Part::Feature] Part__Feature181  label="TopSilk181"
  Placement = pos=(0,0,1.62005) rot=(0,0,1;0rad)
  shape: bbox 1.158 x 0.823 x 2e-07 mm, 1 faces, 0 solids (baked)
FEATURE [Part::Feature] Part__Feature182  label="TopSilk182"
  Placement = pos=(0,0,1.62005) rot=(0,0,1;0rad)
  shape: bbox 1.158 x 0.823 x 2e-07 mm, 1 faces, 0 solids (baked)
FEATURE [Part::Feature] Part__Feature183  label="TopSilk183"
  Placement = pos=(0,0,1.62005) rot=(0,0,1;0rad)
  shape: bbox 0.4994 x 0.254 x 2e-07 mm, 1 faces, 0 solids (baked)
FEATURE [Part::Feature] Part__Feature184  label="TopSilk184"
  Placement = pos=(0,0,1.62005) rot=(0,0,1;0rad)
  shape: bbox 0.4994 x 0.254 x 2e-07 mm, 1 faces, 0 solids (baked)
FEATURE [Part::Feature] Part__Feature185  label="TopSilk185"
  Placement = pos=(0,0,1.62005) rot=(0,0,1;0rad)
  shape: bbox 0.3048 x 0.8026 x 2e-07 mm, 1 faces, 0 solids (baked)
FEATURE [Part::Feature] Part__Feature186  label="TopSilk186"
  Placement = pos=(0,0,1.62005) rot=(0,0,1;0rad)
  shape: bbox 0.5877 x 0.8063 x 2e-07 mm, 1 faces, 0 solids (baked)
FEATURE [Part::Feature] Part__Feature187  label="TopSilk187"
  Placement = pos=(0,0,1.62005) rot=(0,0,1;0rad)
  shape: bbox 1.355 x 2.071 x 2e-07 mm, 1 faces, 0 solids (baked)
FEATURE [Part::Feature] Part__Feature188  label="TopSilk188"
  Placement = pos=(0,0,1.62005) rot=(0,0,1;0rad)
  shape: bbox 0.5867 x 0.8026 x 2e-07 mm, 1 faces, 0 solids (baked)
FEATURE [Part::Feature] Part__Feature189  label="TopSilk189"
  Placement = pos=(0,0,1.62005) rot=(0,0,1;0rad)
  shape: bbox 1.5 x 1.65 x 2e-07 mm, 1 faces, 0 solids (baked)
FEATURE [Part::Feature] Part__Feature190  label="TopSilk190"
  Placement = pos=(0,0,1.62005) rot=(0,0,1;0rad)
  shape: bbox 1.5 x 1.65 x 2e-07 mm, 1 faces, 0 solids (baked)
FEATURE [Part::Feature] Part__Feature191  label="TopSilk191"
  Placement = pos=(0,0,1.62005) rot=(0,0,1;0rad)
  shape: bbox 0.5867 x 0.8136 x 2e-07 mm, 1 faces, 0 solids (baked)
FEATURE [Part::Feature] Part__Feature192  label="TopSilk192"
  Placement = pos=(0,0,1.62005) rot=(0,0,1;0rad)
  shape: bbox 0.7696 x 0.8026 x 2e-07 mm, 1 faces, 0 solids (baked)
FEATURE [Part::Feature] Part__Feature193  label="TopSilk193"
  Placement = pos=(0,0,1.62005) rot=(0,0,1;0rad)
  shape: bbox 0.7696 x 0.8026 x 2e-07 mm, 1 faces, 0 solids (baked)
FEATURE [Part::Feature] Part__Feature194  label="TopSilk194"
  Placement = pos=(0,0,1.62005) rot=(0,0,1;0rad)
  shape: bbox 0.1999 x 0.8 x 2e-07 mm, 1 faces, 0 solids (baked)
FEATURE [Part::Feature] Part__Feature195  label="TopSilk195"
  Placement = pos=(0,0,1.62005) rot=(0,0,1;0rad)
  shape: bbox 0.49 x 0.83 x 2e-07 mm, 1 faces, 0 solids (baked)
FEATURE [Part::Feature] Part__Feature196  label="TopSilk196"
  Placement = pos=(0,0,1.62005) rot=(0,0,1;0rad)
  shape: bbox 1.038 x 1.515 x 2e-07 mm, 1 faces, 0 solids (baked)
FEATURE [Part::Feature] Part__Feature197  label="TopSilk197"
  Placement = pos=(0,0,1.62005) rot=(0,0,1;0rad)
  shape: bbox 0.5842 x 0.8026 x 2e-07 mm, 1 faces, 0 solids (baked)
FEATURE [Part::Feature] Part__Feature198  label="TopSilk198"
  Placement = pos=(0,0,1.62005) rot=(0,0,1;0rad)
  shape: bbox 3.746 x 7.854 x 2e-07 mm, 1 faces, 0 solids (baked)
FEATURE [Part::Feature] Part__Feature199  label="TopSilk199"
  Placement = pos=(0,0,1.62005) rot=(0,0,1;0rad)
  shape: bbox 1.587 x 3.418 x 2e-07 mm, 1 faces, 0 solids (baked)
FEATURE [Part::Feature] Part__Feature200  label="TopSilk200"
  Placement = pos=(0,0,1.62005) rot=(0,0,1;0rad)
  shape: bbox 1.3 x 1.65 x 2e-07 mm, 1 faces, 0 solids (baked)
FEATURE [Part::Feature] Part__Feature201  label="TopSilk201"
  Placement = pos=(0,0,1.62005) rot=(0,0,1;0rad)
  shape: bbox 1.3 x 1.65 x 2e-07 mm, 1 faces, 0 solids (baked)
FEATURE [Part::Feature] Part__Feature202  label="TopSilk202"
  Placement = pos=(0,0,1.62005) rot=(0,0,1;0rad)
  shape: bbox 1.436 x 1.515 x 2e-07 mm, 1 faces, 0 solids (baked)
FEATURE [Part::Feature] Part__Feature203  label="TopSilk203"
  Placement = pos=(0,0,1.62005) rot=(0,0,1;0rad)
  shape: bbox 1.499 x 1.875 x 2e-07 mm, 1 faces, 0 solids (baked)
FEATURE [Part::Feature] Part__Feature204  label="TopSilk204"
  Placement = pos=(0,0,1.62005) rot=(0,0,1;0rad)
  shape: bbox 1.425 x 1.875 x 2e-07 mm, 1 faces, 0 solids (baked)
FEATURE [Part::Feature] Part__Feature205  label="TopSilk205"
  Placement = pos=(0,0,1.62005) rot=(0,0,1;0rad)
  shape: bbox 1.649 x 0.3 x 2e-07 mm, 1 faces, 0 solids (baked)
FEATURE [Part::Feature] Part__Feature206  label="TopSilk206"
  Placement = pos=(0,0,1.62005) rot=(0,0,1;0rad)
  shape: bbox 1.499 x 1.875 x 2e-07 mm, 1 faces, 0 solids (baked)
FEATURE [Part::Feature] Part__Feature207  label="TopSilk207"
  Placement = pos=(0,0,1.62005) rot=(0,0,1;0rad)
  shape: bbox 1.349 x 1.879 x 2e-07 mm, 1 faces, 0 solids (baked)
FEATURE [Part::Feature] Part__Feature208  label="TopSilk208"
  Placement = pos=(0,0,1.62005) rot=(0,0,1;0rad)
  shape: bbox 1.968 x 2.555 x 2e-07 mm, 1 faces, 0 solids (baked)
FEATURE [Part::Feature] Part__Feature209  label="TopSilk209"
  Placement = pos=(0,0,1.62005) rot=(0,0,1;0rad)
  shape: bbox 1.872 x 2.555 x 2e-07 mm, 1 faces, 0 solids (baked)
FEATURE [Part::Feature] Part__Feature210  label="TopSilk210"
  Placement = pos=(0,0,1.62005) rot=(0,0,1;0rad)
  shape: bbox 1.676 x 2.555 x 2e-07 mm, 1 faces, 0 solids (baked)
FEATURE [Part::Feature] Part__Feature211  label="TopSilk211"
  Placement = pos=(0,0,1.62005) rot=(0,0,1;0rad)
  shape: bbox 1.349 x 1.875 x 2e-07 mm, 1 faces, 0 solids (baked)
FEATURE [App::Part] TopSilk  label="TopSilk212"
  Group = -> [Part__Feature,Part__Feature001,Part__Feature002,Part__Feature003,Part__Feature004,Part__Feature005,Part__Feature006,Part__Feature007,Part__Feature008,Part__Feature009,Part__Feature010,Part__Feature011,Part__Feature012,Part__Feature013,Part__Feature014,Part__Feature015,Part__Feature016,Part__Feature017,Part__Feature018,Part__Feature019,Part__Feature020,Part__Feature021,Part__Feature022,+189 more]
  Origin = -> Origin
FEATURE [Part::Feature] Part__Feature212  label="BottomSilk"
  Placement = pos=(0,0,-0.02) rot=(0,0,1;0rad)
  shape: bbox 2.625 x 0.8753 x 2e-07 mm, 1 faces, 0 solids (baked)
FEATURE [Part::Feature] Part__Feature213  label="BottomSilk001"
  Placement = pos=(0,0,-0.02) rot=(0,0,1;0rad)
  shape: bbox 2.625 x 0.8753 x 2e-07 mm, 1 faces, 0 solids (baked)
FEATURE [Part::Feature] Part__Feature214  label="BottomSilk002"
  Placement = pos=(0,0,-0.02) rot=(0,0,1;0rad)
  shape: bbox 2.536 x 1.401 x 2e-07 mm, 1 faces, 0 solids (baked)
FEATURE [Part::Feature] Part__Feature215  label="BottomSilk003"
  Placement = pos=(0,0,-0.02) rot=(0,0,1;0rad)
  shape: bbox 2.536 x 1.924 x 2e-07 mm, 1 faces, 0 solids (baked)
FEATURE [Part::Feature] Part__Feature216  label="BottomSilk004"
  Placement = pos=(0,0,-0.02) rot=(0,0,1;0rad)
  shape: bbox 2.536 x 1.838 x 2e-07 mm, 1 faces, 0 solids (baked)
FEATURE [Part::Feature] Part__Feature217  label="BottomSilk005"
  Placement = pos=(0,0,-0.02) rot=(0,0,1;0rad)
  shape: bbox 2.536 x 1.401 x 2e-07 mm, 1 faces, 0 solids (baked)
FEATURE [Part::Feature] Part__Feature218  label="BottomSilk006"
  Placement = pos=(0,0,-0.02) rot=(0,0,1;0rad)
  shape: bbox 2.536 x 2.45 x 2e-07 mm, 1 faces, 0 solids (baked)
FEATURE [Part::Feature] Part__Feature219  label="BottomSilk007"
  Placement = pos=(0,0,-0.02) rot=(0,0,1;0rad)
  shape: bbox 2.536 x 2.45 x 2e-07 mm, 1 faces, 0 solids (baked)
FEATURE [Part::Feature] Part__Feature220  label="BottomSilk008"
  Placement = pos=(0,0,-0.02) rot=(0,0,1;0rad)
  shape: bbox 2.536 x 1.137 x 2e-07 mm, 1 faces, 0 solids (baked)
FEATURE [Part::Feature] Part__Feature221  label="BottomSilk009"
  Placement = pos=(0,0,-0.02) rot=(0,0,1;0rad)
  shape: bbox 2.536 x 1.924 x 2e-07 mm, 1 faces, 0 solids (baked)
FEATURE [Part::Feature] Part__Feature222  label="BottomSilk010"
  Placement = pos=(0,0,-0.02) rot=(0,0,1;0rad)
  shape: bbox 2.536 x 2.011 x 2e-07 mm, 1 faces, 0 solids (baked)
FEATURE [Part::Feature] Part__Feature223  label="BottomSilk011"
  Placement = pos=(0,0,-0.02) rot=(0,0,1;0rad)
  shape: bbox 2.536 x 1.924 x 2e-07 mm, 1 faces, 0 solids (baked)
FEATURE [Part::Feature] Part__Feature224  label="BottomSilk012"
  Placement = pos=(0,0,-0.02) rot=(0,0,1;0rad)
  shape: bbox 2.536 x 1.401 x 2e-07 mm, 1 faces, 0 solids (baked)
FEATURE [Part::Feature] Part__Feature225  label="BottomSilk013"
  Placement = pos=(0,0,-0.02) rot=(0,0,1;0rad)
  shape: bbox 2.536 x 0.7 x 2e-07 mm, 1 faces, 0 solids (baked)
FEATURE [Part::Feature] Part__Feature226  label="BottomSilk014"
  Placement = pos=(0,0,-0.02) rot=(0,0,1;0rad)
  shape: bbox 2.536 x 0.7 x 2e-07 mm, 1 faces, 0 solids (baked)
FEATURE [Part::Feature] Part__Feature227  label="BottomSilk015"
  Placement = pos=(0,0,-0.02) rot=(0,0,1;0rad)
  shape: bbox 1.924 x 1.401 x 2e-07 mm, 1 faces, 0 solids (baked)
FEATURE [Part::Feature] Part__Feature228  label="BottomSilk016"
  Placement = pos=(0,0,-0.02) rot=(0,0,1;0rad)
  shape: bbox 1.924 x 1.749 x 2e-07 mm, 1 faces, 0 solids (baked)
FEATURE [Part::Feature] Part__Feature229  label="BottomSilk017"
  Placement = pos=(0,0,-0.02) rot=(0,0,1;0rad)
  shape: bbox 1.924 x 1.663 x 2e-07 mm, 1 faces, 0 solids (baked)
FEATURE [Part::Feature] Part__Feature230  label="BottomSilk018"
  Placement = pos=(0,0,-0.02) rot=(0,0,1;0rad)
  shape: bbox 1.924 x 2.625 x 2e-07 mm, 1 faces, 0 solids (baked)
FEATURE [Part::Feature] Part__Feature231  label="BottomSilk019"
  Placement = pos=(0,0,-0.02) rot=(0,0,1;0rad)
  shape: bbox 1.924 x 1.749 x 2e-07 mm, 1 faces, 0 solids (baked)
FEATURE [Part::Feature] Part__Feature232  label="BottomSilk020"
  Placement = pos=(0,0,-0.02) rot=(0,0,1;0rad)
  shape: bbox 1.924 x 2.625 x 2e-07 mm, 1 faces, 0 solids (baked)
FEATURE [Part::Feature] Part__Feature233  label="BottomSilk021"
  Placement = pos=(0,0,-0.02) rot=(0,0,1;0rad)
  shape: bbox 1.924 x 1.401 x 2e-07 mm, 1 faces, 0 solids (baked)
FEATURE [Part::Feature] Part__Feature234  label="BottomSilk022"
  Placement = pos=(0,0,-0.02) rot=(0,0,1;0rad)
  shape: bbox 1.924 x 1.401 x 2e-07 mm, 1 faces, 0 solids (baked)
FEATURE [Part::Feature] Part__Feature235  label="BottomSilk023"
  Placement = pos=(0,0,-0.02) rot=(0,0,1;0rad)
  shape: bbox 1.924 x 1.838 x 2e-07 mm, 1 faces, 0 solids (baked)
FEATURE [Part::Feature] Part__Feature236  label="BottomSilk024"
  Placement = pos=(0,0,-0.02) rot=(0,0,1;0rad)
  shape: bbox 1.924 x 1.749 x 2e-07 mm, 1 faces, 0 solids (baked)
FEATURE [Part::Feature] Part__Feature237  label="BottomSilk025"
  Placement = pos=(0,0,-0.02) rot=(0,0,1;0rad)
  shape: bbox 2.536 x 1.749 x 2e-07 mm, 1 faces, 0 solids (baked)
FEATURE [Part::Feature] Part__Feature238  label="BottomSilk026"
  Placement = pos=(0,0,-0.02) rot=(0,0,1;0rad)
  shape: bbox 1.924 x 1.663 x 2e-07 mm, 1 faces, 0 solids (baked)
FEATURE [Part::Feature] Part__Feature239  label="BottomSilk027"
  Placement = pos=(0,0,-0.02) rot=(0,0,1;0rad)
  shape: bbox 1.924 x 1.838 x 2e-07 mm, 1 faces, 0 solids (baked)
FEATURE [Part::Feature] Part__Feature240  label="BottomSilk028"
  Placement = pos=(0,0,-0.02) rot=(0,0,1;0rad)
  shape: bbox 1.924 x 1.401 x 2e-07 mm, 1 faces, 0 solids (baked)
FEATURE [Part::Feature] Part__Feature241  label="BottomSilk029"
  Placement = pos=(0,0,-0.02) rot=(0,0,1;0rad)
  shape: bbox 1.924 x 1.749 x 2e-07 mm, 1 faces, 0 solids (baked)
FEATURE [Part::Feature] Part__Feature242  label="BottomSilk030"
  Placement = pos=(0,0,-0.02) rot=(0,0,1;0rad)
  shape: bbox 25 x 35 x 2e-07 mm, 1 faces, 0 solids (baked)
FEATURE [Part::Feature] Part__Feature243  label="BottomSilk031"
  Placement = pos=(0,0,-0.02) rot=(0,0,1;0rad)
  shape: bbox 2.211 x 2.606 x 2e-07 mm, 1 faces, 0 solids (baked)
FEATURE [Part::Feature] Part__Feature244  label="BottomSilk032"
  Placement = pos=(0,0,-0.02) rot=(0,0,1;0rad)
  shape: bbox 17.31 x 17.91 x 2e-07 mm, 1 faces, 0 solids (baked)
FEATURE [Part::Feature] Part__Feature245  label="BottomSilk033"
  Placement = pos=(0,0,-0.02) rot=(0,0,1;0rad)
  shape: bbox 1.37 x 2.502 x 2e-07 mm, 1 faces, 0 solids (baked)
FEATURE [Part::Feature] Part__Feature246  label="BottomSilk034"
  Placement = pos=(0,0,-0.02) rot=(0,0,1;0rad)
  shape: bbox 2.158 x 2.606 x 2e-07 mm, 1 faces, 0 solids (baked)
FEATURE [Part::Feature] Part__Feature247  label="BottomSilk035"
  Placement = pos=(0,0,-0.02) rot=(0,0,1;0rad)
  shape: bbox 2.139 x 2.537 x 2e-07 mm, 1 faces, 0 solids (baked)
FEATURE [Part::Feature] Part__Feature248  label="BottomSilk036"
  Placement = pos=(0,0,-0.02) rot=(0,0,1;0rad)
  shape: bbox 3.297 x 2.486 x 2e-07 mm, 1 faces, 0 solids (baked)
FEATURE [Part::Feature] Part__Feature249  label="BottomSilk037"
  Placement = pos=(0,0,-0.02) rot=(0,0,1;0rad)
  shape: bbox 2.206 x 2.64 x 2e-07 mm, 1 faces, 0 solids (baked)
FEATURE [Part::Feature] Part__Feature250  label="BottomSilk038"
  Placement = pos=(0,0,-0.02) rot=(0,0,1;0rad)
  shape: bbox 2.261 x 3.531 x 2e-07 mm, 1 faces, 0 solids (baked)
FEATURE [Part::Feature] Part__Feature251  label="BottomSilk039"
  Placement = pos=(0,0,-0.02) rot=(0,0,1;0rad)
  shape: bbox 2.258 x 3.43 x 2e-07 mm, 1 faces, 0 solids (baked)
FEATURE [Part::Feature] Part__Feature252  label="BottomSilk040"
  Placement = pos=(0,0,-0.02) rot=(0,0,1;0rad)
  shape: bbox 3.073 x 3.514 x 2e-07 mm, 1 faces, 0 solids (baked)
FEATURE [Part::Feature] Part__Feature253  label="BottomSilk041"
  Placement = pos=(0,0,-0.02) rot=(0,0,1;0rad)
  shape: bbox 1.37 x 2.502 x 2e-07 mm, 1 faces, 0 solids (baked)
FEATURE [Part::Feature] Part__Feature254  label="BottomSilk042"
  Placement = pos=(0,0,-0.02) rot=(0,0,1;0rad)
  shape: bbox 2.175 x 2.607 x 2e-07 mm, 1 faces, 0 solids (baked)
FEATURE [Part::Feature] Part__Feature255  label="BottomSilk043"
  Placement = pos=(0,0,-0.02) rot=(0,0,1;0rad)
  shape: bbox 2.574 x 3.334 x 2e-07 mm, 1 faces, 0 solids (baked)
FEATURE [Part::Feature] Part__Feature256  label="BottomSilk044"
  Placement = pos=(0,0,-0.02) rot=(0,0,1;0rad)
  shape: bbox 3.413 x 1.866 x 2e-07 mm, 1 faces, 0 solids (baked)
FEATURE [Part::Feature] Part__Feature257  label="BottomSilk045"
  Placement = pos=(0,0,-0.02) rot=(0,0,1;0rad)
  shape: bbox 33.69 x 11.68 x 2e-07 mm, 1 faces, 0 solids (baked)
FEATURE [Part::Feature] Part__Feature258  label="BottomSilk046"
  Placement = pos=(0,0,-0.02) rot=(0,0,1;0rad)
  shape: bbox 3.334 x 2.732 x 2e-07 mm, 1 faces, 0 solids (baked)
FEATURE [Part::Feature] Part__Feature259  label="BottomSilk047"
  Placement = pos=(0,0,-0.02) rot=(0,0,1;0rad)
  shape: bbox 2.176 x 1.861 x 2e-07 mm, 1 faces, 0 solids (baked)
FEATURE [Part::Feature] Part__Feature260  label="BottomSilk048"
  Placement = pos=(0,0,-0.02) rot=(0,0,1;0rad)
  shape: bbox 2.525 x 2.654 x 2e-07 mm, 1 faces, 0 solids (baked)
FEATURE [Part::Feature] Part__Feature261  label="BottomSilk049"
  Placement = pos=(0,0,-0.02) rot=(0,0,1;0rad)
  shape: bbox 1.982 x 1.856 x 2e-07 mm, 1 faces, 0 solids (baked)
FEATURE [Part::Feature] Part__Feature262  label="BottomSilk050"
  Placement = pos=(0,0,-0.02) rot=(0,0,1;0rad)
  shape: bbox 1.99 x 1.864 x 2e-07 mm, 1 faces, 0 solids (baked)
FEATURE [Part::Feature] Part__Feature263  label="BottomSilk051"
  Placement = pos=(0,0,-0.02) rot=(0,0,1;0rad)
  shape: bbox 1.745 x 1.861 x 2e-07 mm, 1 faces, 0 solids (baked)
FEATURE [Part::Feature] Part__Feature264  label="BottomSilk052"
  Placement = pos=(0,0,-0.02) rot=(0,0,1;0rad)
  shape: bbox 2.388 x 2.581 x 2e-07 mm, 1 faces, 0 solids (baked)
FEATURE [Part::Feature] Part__Feature265  label="BottomSilk053"
  Placement = pos=(0,0,-0.02) rot=(0,0,1;0rad)
  shape: bbox 2.242 x 1.811 x 2e-07 mm, 1 faces, 0 solids (baked)
FEATURE [Part::Feature] Part__Feature266  label="BottomSilk054"
  Placement = pos=(0,0,-0.02) rot=(0,0,1;0rad)
  shape: bbox 0.6978 x 0.6485 x 2e-07 mm, 1 faces, 0 solids (baked)
FEATURE [Part::Feature] Part__Feature267  label="BottomSilk055"
  Placement = pos=(0,0,-0.02) rot=(0,0,1;0rad)
  shape: bbox 1.109 x 1.791 x 2e-07 mm, 1 faces, 0 solids (baked)
FEATURE [Part::Feature] Part__Feature268  label="BottomSilk056"
  Placement = pos=(0,0,-0.02) rot=(0,0,1;0rad)
  shape: bbox 1.812 x 1.861 x 2e-07 mm, 1 faces, 0 solids (baked)
FEATURE [Part::Feature] Part__Feature269  label="BottomSilk057"
  Placement = pos=(0,0,-0.02) rot=(0,0,1;0rad)
  shape: bbox 2.267 x 1.862 x 2e-07 mm, 1 faces, 0 solids (baked)
FEATURE [Part::Feature] Part__Feature270  label="BottomSilk058"
  Placement = pos=(0,0,-0.02) rot=(0,0,1;0rad)
  shape: bbox 1.986 x 1.857 x 2e-07 mm, 1 faces, 0 solids (baked)
FEATURE [Part::Feature] Part__Feature271  label="BottomSilk059"
  Placement = pos=(0,0,-0.02) rot=(0,0,1;0rad)
  shape: bbox 1.998 x 1.863 x 2e-07 mm, 1 faces, 0 solids (baked)
FEATURE [Part::Feature] Part__Feature272  label="BottomSilk060"
  Placement = pos=(0,0,-0.02) rot=(0,0,1;0rad)
  shape: bbox 1.745 x 1.862 x 2e-07 mm, 1 faces, 0 solids (baked)
FEATURE [Part::Feature] Part__Feature273  label="BottomSilk061"
  Placement = pos=(0,0,-0.02) rot=(0,0,1;0rad)
  shape: bbox 2.394 x 2.58 x 2e-07 mm, 1 faces, 0 solids (baked)
FEATURE [App::Part] BottomSilk  label="BottomSilk062"
  Group = -> [Part__Feature212,Part__Feature213,Part__Feature214,Part__Feature215,Part__Feature216,Part__Feature217,Part__Feature218,Part__Feature219,Part__Feature220,Part__Feature221,Part__Feature222,Part__Feature223,Part__Feature224,Part__Feature225,Part__Feature226,Part__Feature227,Part__Feature228,Part__Feature229,Part__Feature230,Part__Feature231,Part__Feature232,Part__Feature233,Part__Feature234,+39 more]
  Origin = -> Origin052
FEATURE [Part::Feature] Part__Feature274  label="Board"
  shape: bbox 101.2 x 80.02 x 1.6 mm, 116 faces (baked)
FEATURE [Part::Feature] Part__Feature275  label="C1206"
  shape: bbox 0.762 x 0.762 x 0.762 mm, 6 faces (baked)
FEATURE [App::Part] pRkl_C1  label="pRkl-C1"
  Group = -> [Part__Feature275]
  Origin = -> Origin053
  Placement = pos=(41.4021,36.4491,1.60005) rot=(0,0,1;1.5708rad)
FEATURE [Part::Feature] Part__Feature276  label="C1207"
  shape: bbox 0.762 x 0.762 x 0.762 mm, 6 faces (baked)
FEATURE [App::Part] pRkl_C3  label="pRkl-C3"
  Group = -> [Part__Feature276]
  Origin = -> Origin054
  Placement = pos=(66.1671,49.5301,1.60005) rot=(0,0,1;1.5708rad)
FEATURE [Part::Feature] Part__Feature277  label="C0402"
  shape: bbox 0.762 x 0.762 x 0.762 mm, 6 faces (baked)
FEATURE [App::Part] pRkl_C5  label="pRkl-C5"
  Group = -> [Part__Feature277]
  Origin = -> Origin055
  Placement = pos=(45.8471,27.5591,1.60005) rot=(0,0,1;0rad)
FEATURE [Part::Feature] Part__Feature278  label="COMPOUND"
  shape: bbox 1.601 x 2.901 x 1.1 mm, 207 faces (baked)
FEATURE [Part::Feature] Part__Feature279  label="COMPOUND001"
  shape: bbox 0.6046 x 0.4 x 0.7911 mm, 51 faces (baked)
FEATURE [Part::Feature] Part__Feature280  label="COMPOUND002"
  shape: bbox 0.6046 x 0.4 x 0.7911 mm, 51 faces (baked)
FEATURE [Part::Feature] Part__Feature281  label="COMPOUND003"
  shape: bbox 0.6046 x 0.4 x 0.7911 mm, 51 faces (baked)
FEATURE [Part::Feature] Part__Feature282  label="COMPOUND004"
  shape: bbox 0.06101 x 0.03218 x 0.001 mm, 8 faces (baked)
FEATURE [Part::Feature] Part__Feature283  label="COMPOUND005"
  shape: bbox 0.06307 x 0.04568 x 0.001 mm, 16 faces (baked)
FEATURE [Part::Feature] Part__Feature284  label="COMPOUND006"
  shape: bbox 0.06101 x 0.03281 x 0.001 mm, 14 faces (baked)
FEATURE [Part::Feature] Part__Feature285  label="COMPOUND007"
  shape: bbox 0.06101 x 0.04967 x 0.001 mm, 16 faces (baked)
FEATURE [Part::Feature] Part__Feature286  label="COMPOUND008"
  shape: bbox 0.06101 x 0.0549 x 0.001 mm, 16 faces (baked)
FEATURE [Part::Feature] Part__Feature287  label="COMPOUND009"
  shape: bbox 0.06101 x 0.03281 x 0.001 mm, 14 faces (baked)
FEATURE [Part::Feature] Part__Feature288  label="COMPOUND010"
  shape: bbox 0.0456 x 0.03501 x 0.001 mm, 24 faces (baked)
FEATURE [Part::Feature] Part__Feature289  label="COMPOUND011"
  shape: bbox 0.0456 x 0.02943 x 0.001 mm, 23 faces (baked)
FEATURE [Part::Feature] Part__Feature290  label="COMPOUND012"
  shape: bbox 0.0641 x 0.04183 x 0.001 mm, 17 faces (baked)
FEATURE [Part::Feature] Part__Feature291  label="COMPOUND013"
  shape: bbox 0.06101 x 0.03281 x 0.001 mm, 14 faces (baked)
FEATURE [Part::Feature] Part__Feature292  label="COMPOUND014"
  shape: bbox 0.06101 x 0.04967 x 0.001 mm, 16 faces (baked)
FEATURE [Part::Feature] Part__Feature293  label="COMPOUND015"
  shape: bbox 0.06101 x 0.0549 x 0.001 mm, 16 faces (baked)
FEATURE [Part::Feature] Part__Feature294  label="COMPOUND016"
  shape: bbox 0.203 x 0.2768 x 0.001 mm, 37 faces (baked)
FEATURE [App::Part] COMPOUND  label="COMPOUND017"
  Group = -> [Part__Feature278,Part__Feature279,Part__Feature280,Part__Feature281,Part__Feature282,Part__Feature283,Part__Feature284,Part__Feature285,Part__Feature286,Part__Feature287,Part__Feature288,Part__Feature289,Part__Feature290,Part__Feature291,Part__Feature292,Part__Feature293,Part__Feature294]
  Origin = -> Origin056
FEATURE [App::Part] SOT_23_3_L3_0_W1_7_P0_95_LS2_9_BR  label="SOT-23-3_L3.0-W1.7-P0.95-LS2.9-BR"
  Group = -> [COMPOUND]
  Origin = -> Origin057
FEATURE [App::Part] pRkl_Q1  label="pRkl-Q1"
  Group = -> [SOT_23_3_L3_0_W1_7_P0_95_LS2_9_BR]
  Origin = -> Origin058
  Placement = pos=(79.6292,30.7341,1.60005) rot=(0,0,1;3.14159rad)
FEATURE [Part::Feature] Part__Feature295  label="SOLID"
  shape: bbox 3.1 x 2.601 x 0.55 mm, 250 faces (baked)
FEATURE [App::Part] R1210
  Group = -> [Part__Feature295]
  Origin = -> Origin059
FEATURE [App::Part] pRkl_R10  label="pRkl-R10"
  Group = -> [R1210]
  Origin = -> Origin060
  Placement = pos=(85.8941,49.6463,1.60005) rot=(0,0,1;0rad)
FEATURE [Part::Feature] Part__Feature296  label="SOLID001"
  shape: bbox 3.1 x 2.601 x 0.55 mm, 250 faces (baked)
FEATURE [App::Part] R1211
  Group = -> [Part__Feature296]
  Origin = -> Origin061
FEATURE [App::Part] pRkl_R11  label="pRkl-R11"
  Group = -> [R1211]
  Origin = -> Origin062
  Placement = pos=(78.4605,37.4543,1.60005) rot=(0,0,1;1.5708rad)
FEATURE [Part::Feature] Part__Feature297  label="SOLID002"
  shape: bbox 3.1 x 2.601 x 0.55 mm, 250 faces (baked)
FEATURE [App::Part] R1212
  Group = -> [Part__Feature297]
  Origin = -> Origin063
FEATURE [App::Part] pRkl_R2  label="pRkl-R2"
  Group = -> [R1212]
  Origin = -> Origin064
  Placement = pos=(65.6591,35.1791,1.60005) rot=(0,0,-1;1.5708rad)
FEATURE [Part::Feature] Part__Feature298  label="R0402"
  shape: bbox 0.762 x 0.762 x 0.762 mm, 6 faces (baked)
FEATURE [App::Part] pRkl_R3  label="pRkl-R3"
  Group = -> [Part__Feature298]
  Origin = -> Origin065
  Placement = pos=(45.3391,31.7501,1.60005) rot=(0,0,1;0rad)
FEATURE [Part::Feature] Part__Feature299  label="SOLID003"
  shape: bbox 34.54 x 20.32 x 27.51 mm, 472 faces (baked)
FEATURE [App::Part] PWRM_TH_HLK_PM03  label="PWRM-TH_HLK-PM03"
  Group = -> [Part__Feature299]
  Origin = -> Origin066
FEATURE [App::Part] pRkl_AC_DC_CONV  label="pRkl-AC-DC-CONV"
  Group = -> [PWRM_TH_HLK_PM03]
  Origin = -> Origin067
  Placement = pos=(46.9901,75.3112,1.60005) rot=(0,0,-1;1.5708rad)
FEATURE [Part::Feature] Part__Feature300  label="R0603"
  shape: bbox 1.62 x 0.81 x 0.762 mm, 6 faces (baked)
FEATURE [App::Part] pRkl_R8  label="pRkl-R8"
  Group = -> [Part__Feature300]
  Origin = -> Origin068
  Placement = pos=(66.9291,29.7181,1.60005) rot=(0,0,-1;1.5708rad)
FEATURE [Part::Feature] Part__Feature301  label="R1213"
  shape: bbox 1.62 x 0.81 x 0.762 mm, 6 faces (baked)
FEATURE [App::Part] pRkl_R9  label="pRkl-R9"
  Group = -> [Part__Feature301]
  Origin = -> Origin069
  Placement = pos=(72.7711,31.1151,1.60005) rot=(0,0,-1;1.5708rad)
FEATURE [Part::Feature] Part__Feature302  label="COMPOUND018"
  shape: bbox 6 x 5.5 x 10.3 mm, 117 faces (baked)
FEATURE [Part::Feature] Part__Feature303  label="COMPOUND019"
  shape: bbox 8.21 x 6.528 x 10.7 mm, 321 faces (baked)
FEATURE [App::Part] COMPOUND001  label="COMPOUND020"
  Group = -> [Part__Feature302,Part__Feature303]
  Origin = -> Origin070
FEATURE [App::Part] KEY_TH_K2_1102AQ_D4CW_01  label="KEY-TH_K2-1102AQ-D4CW-01"
  Group = -> [COMPOUND001]
  Origin = -> Origin071
FEATURE [App::Part] pRkl_BTN  label="pRkl-BTN"
  Group = -> [KEY_TH_K2_1102AQ_D4CW_01]
  Origin = -> Origin072
  Placement = pos=(86.8682,24.13,1.60005) rot=(0,0,1;1.5708rad)
FEATURE [Part::Feature] Part__Feature304  label="SOLID004"
  shape: bbox 10 x 8.659 x 10.05 mm, 286 faces (baked)
FEATURE [App::Part] CAP_SMD_BD8_0_L8_3_W8_3_FD  label="CAP-SMD_BD8.0-L8.3-W8.3-FD"
  Group = -> [Part__Feature304]
  Origin = -> Origin073
FEATURE [App::Part] pRkl_C4  label="pRkl-C4"
  Group = -> [CAP_SMD_BD8_0_L8_3_W8_3_FD]
  Origin = -> Origin074
  Placement = pos=(37.8461,26.7971,1.60005) rot=(0,0,1;1.5708rad)
FEATURE [Part::Feature] Part__Feature305  label="SOLID005"
  shape: bbox 10 x 8.659 x 10.05 mm, 286 faces (baked)
FEATURE [App::Part] CAP_SMD_BD8_0_L8_3_W8_3_FD001  label="CAP-SMD_BD8.0-L8.3-W8.3-FD001"
  Group = -> [Part__Feature305]
  Origin = -> Origin075
FEATURE [App::Part] pRkl_C2  label="pRkl-C2"
  Group = -> [CAP_SMD_BD8_0_L8_3_W8_3_FD001]
  Origin = -> Origin076
  Placement = pos=(76.9622,48.5141,1.60005) rot=(0,0,1;1.5708rad)
FEATURE [Part::Feature] Part__Feature306  label="COMPOUND021"
  shape: bbox 30 x 14.6 x 3 mm, 27 faces (baked)
FEATURE [Part::Feature] Part__Feature307  label="COMPOUND022"
  shape: bbox 30 x 16 x 21.8 mm, 984 faces (baked)
FEATURE [App::Part] COMPOUND002  label="COMPOUND023"
  Group = -> [Part__Feature306,Part__Feature307]
  Origin = -> Origin077
FEATURE [App::Part] CONN_TH_3P_P9_50_HB9500_9_5_3P  label="CONN-TH_3P-P9.50_HB9500-9.5-3P"
  Group = -> [COMPOUND002]
  Origin = -> Origin078
FEATURE [App::Part] pRkl_AC_OUT  label="pRkl-AC_OUT"
  Group = -> [CONN_TH_3P_P9_50_HB9500_9_5_3P]
  Origin = -> Origin079
  Placement = pos=(86.1062,81.7882,1.60005) rot=(0,0,1;1.5708rad)
FEATURE [Part::Feature] Part__Feature308  label="COMPOUND024"
  shape: bbox 30 x 14.6 x 3 mm, 27 faces (baked)
FEATURE [Part::Feature] Part__Feature309  label="COMPOUND025"
  shape: bbox 30 x 16 x 21.8 mm, 984 faces (baked)
FEATURE [App::Part] COMPOUND003  label="COMPOUND026"
  Group = -> [Part__Feature308,Part__Feature309]
  Origin = -> Origin080
FEATURE [App::Part] CONN_TH_3P_P9_50_HB9500_9_5_3P001  label="CONN-TH_3P-P9.50_HB9500-9.5-3P001"
  Group = -> [COMPOUND003]
  Origin = -> Origin081
FEATURE [App::Part] pRkl_AC_IN  label="pRkl-AC_IN"
  Group = -> [CONN_TH_3P_P9_50_HB9500_9_5_3P001]
  Origin = -> Origin082
  Placement = pos=(14.732,81.2802,1.60005) rot=(0,0,-1;1.5708rad)
FEATURE [Part::Feature] Part__Feature310  label="SOLID006"
  shape: bbox 3.302 x 1.732 x 1.732 mm, 256 faces (baked)
FEATURE [App::Part] SOD_80_L3_5_W1_5_RD  label="SOD-80_L3.5-W1.5-RD"
  Group = -> [Part__Feature310]
  Origin = -> Origin083
FEATURE [App::Part] pRkl_D1  label="pRkl-D1"
  Group = -> [SOD_80_L3_5_W1_5_RD]
  Origin = -> Origin084
  Placement = pos=(71.6281,39.2431,1.60005) rot=(0,0,1;1.5708rad)
FEATURE [Part::Feature] Part__Feature311  label="COMPOUND027"
  shape: bbox 14.8 x 9.5 x 5.11 mm, 23 faces (baked)
FEATURE [Part::Feature] Part__Feature312  label="COMPOUND028"
  shape: bbox 21.4 x 15.16 x 14 mm, 101 faces (baked)
FEATURE [Part::Feature] Part__Feature313  label="COMPOUND029"
  shape: bbox 0.8 x 4.8 x 4 mm, 12 faces (baked)
FEATURE [Part::Feature] Part__Feature314  label="COMPOUND030"
  shape: bbox 0.8 x 4.8 x 4 mm, 12 faces (baked)
FEATURE [Part::Feature] Part__Feature315  label="COMPOUND031"
  shape: bbox 0.8 x 4.8 x 4 mm, 12 faces (baked)
FEATURE [Part::Feature] Part__Feature316  label="COMPOUND032"
  shape: bbox 0.3222 x 0.001 x 0.6124 mm, 8 faces (baked)
FEATURE [Part::Feature] Part__Feature317  label="COMPOUND033"
  shape: bbox 0.4596 x 0.001 x 0.6317 mm, 16 faces (baked)
FEATURE [Part::Feature] Part__Feature318  label="COMPOUND034"
  shape: bbox 0.3286 x 0.001 x 0.6124 mm, 14 faces (baked)
FEATURE [Part::Feature] Part__Feature319  label="COMPOUND035"
  shape: bbox 0.4996 x 0.001 x 0.612 mm, 16 faces (baked)
FEATURE [Part::Feature] Part__Feature320  label="COMPOUND036"
  shape: bbox 0.549 x 0.001 x 0.6124 mm, 16 faces (baked)
FEATURE [Part::Feature] Part__Feature321  label="COMPOUND037"
  shape: bbox 0.3286 x 0.001 x 0.6124 mm, 14 faces (baked)
FEATURE [Part::Feature] Part__Feature322  label="COMPOUND038"
  shape: bbox 0.3524 x 0.001 x 0.4565 mm, 24 faces (baked)
FEATURE [Part::Feature] Part__Feature323  label="COMPOUND039"
  shape: bbox 0.2952 x 0.001 x 0.4564 mm, 23 faces (baked)
FEATURE [Part::Feature] Part__Feature324  label="COMPOUND040"
  shape: bbox 0.4183 x 0.001 x 0.6419 mm, 17 faces (baked)
FEATURE [Part::Feature] Part__Feature325  label="COMPOUND041"
  shape: bbox 0.3286 x 0.001 x 0.6124 mm, 14 faces (baked)
FEATURE [Part::Feature] Part__Feature326  label="COMPOUND042"
  shape: bbox 0.4996 x 0.001 x 0.612 mm, 16 faces (baked)
FEATURE [Part::Feature] Part__Feature327  label="COMPOUND043"
  shape: bbox 0.549 x 0.001 x 0.6124 mm, 16 faces (baked)
FEATURE [Part::Feature] Part__Feature328  label="COMPOUND044"
  shape: bbox 2.768 x 0.001 x 2.029 mm, 37 faces (baked)
FEATURE [App::Part] COMPOUND004  label="COMPOUND045"
  Group = -> [Part__Feature311,Part__Feature312,Part__Feature313,Part__Feature314,Part__Feature315,Part__Feature316,Part__Feature317,Part__Feature318,Part__Feature319,Part__Feature320,Part__Feature321,Part__Feature322,Part__Feature323,Part__Feature324,Part__Feature325,Part__Feature326,Part__Feature327,Part__Feature328]
  Origin = -> Origin085
FEATURE [App::Part] SW_TH_SS11_BBIWQ_R30_R  label="SW-TH_SS11-BBIWQ-R30-R"
  Group = -> [COMPOUND004]
  Origin = -> Origin086
FEATURE [App::Part] pRkl_SW2  label="pRkl-SW2"
  Group = -> [SW_TH_SS11_BBIWQ_R30_R]
  Origin = -> Origin087
  Placement = pos=(17.145,33.5281,1.60005) rot=(0,0,-1;1.5708rad)
FEATURE [Part::Feature] Part__Feature329  label="COMPOUND046"
  shape: bbox 0.9 x 1.4 x 0.1 mm, 6 faces (baked)
FEATURE [Part::Feature] Part__Feature330  label="COMPOUND047"
  shape: bbox 0.9 x 1.4 x 0.1 mm, 6 faces (baked)
FEATURE [Part::Feature] Part__Feature331  label="COMPOUND048"
  shape: bbox 3.9 x 2.9 x 1.85 mm, 250 faces (baked)
FEATURE [Part::Feature] Part__Feature332  label="COMPOUND049"
  shape: bbox 0.06445 x 0.1225 x 0.001 mm, 8 faces (baked)
FEATURE [Part::Feature] Part__Feature333  label="COMPOUND050"
  shape: bbox 0.09192 x 0.1263 x 0.001 mm, 16 faces (baked)
FEATURE [Part::Feature] Part__Feature334  label="COMPOUND051"
  shape: bbox 0.06573 x 0.1225 x 0.001 mm, 14 faces (baked)
FEATURE [Part::Feature] Part__Feature335  label="COMPOUND052"
  shape: bbox 0.09992 x 0.1224 x 0.001 mm, 16 faces (baked)
FEATURE [Part::Feature] Part__Feature336  label="COMPOUND053"
  shape: bbox 0.1098 x 0.1225 x 0.001 mm, 16 faces (baked)
FEATURE [Part::Feature] Part__Feature337  label="COMPOUND054"
  shape: bbox 0.06573 x 0.1225 x 0.001 mm, 14 faces (baked)
FEATURE [Part::Feature] Part__Feature338  label="COMPOUND055"
  shape: bbox 0.07047 x 0.09129 x 0.001 mm, 24 faces (baked)
FEATURE [Part::Feature] Part__Feature339  label="COMPOUND056"
  shape: bbox 0.05905 x 0.09127 x 0.001 mm, 23 faces (baked)
FEATURE [Part::Feature] Part__Feature340  label="COMPOUND057"
  shape: bbox 0.08366 x 0.1284 x 0.001 mm, 17 faces (baked)
FEATURE [Part::Feature] Part__Feature341  label="COMPOUND058"
  shape: bbox 0.06573 x 0.1225 x 0.001 mm, 14 faces (baked)
FEATURE [Part::Feature] Part__Feature342  label="COMPOUND059"
  shape: bbox 0.09992 x 0.1224 x 0.001 mm, 16 faces (baked)
FEATURE [Part::Feature] Part__Feature343  label="COMPOUND060"
  shape: bbox 0.1098 x 0.1225 x 0.001 mm, 16 faces (baked)
FEATURE [Part::Feature] Part__Feature344  label="COMPOUND061"
  shape: bbox 0.5536 x 0.4058 x 0.001 mm, 37 faces (baked)
FEATURE [App::Part] COMPOUND005  label="COMPOUND062"
  Group = -> [Part__Feature329,Part__Feature330,Part__Feature331,Part__Feature332,Part__Feature333,Part__Feature334,Part__Feature335,Part__Feature336,Part__Feature337,Part__Feature338,Part__Feature339,Part__Feature340,Part__Feature341,Part__Feature342,Part__Feature343,Part__Feature344]
  Origin = -> Origin088
FEATURE [App::Part] SW_SMD_L3_9_W3_0_P4_45  label="SW-SMD_L3.9-W3.0-P4.45"
  Group = -> [COMPOUND005]
  Origin = -> Origin089
FEATURE [App::Part] pRkl_BOOT  label="pRkl-BOOT"
  Group = -> [SW_SMD_L3_9_W3_0_P4_45]
  Origin = -> Origin090
  Placement = pos=(57.2771,31.8771,1.60005) rot=(0,0,1;0rad)
FEATURE [Part::Feature] Part__Feature345  label="COMPOUND063"
  shape: bbox 2.5 x 1.25 x 0.95 mm, 123 faces (baked)
FEATURE [Part::Feature] Part__Feature346  label="COMPOUND064"
  shape: bbox 0.03003 x 0.00596 x 0.05682 mm, 8 faces (baked)
FEATURE [Part::Feature] Part__Feature347  label="COMPOUND065"
  shape: bbox 0.04264 x 0.006127 x 0.05873 mm, 16 faces (baked)
FEATURE [Part::Feature] Part__Feature348  label="COMPOUND066"
  shape: bbox 0.03063 x 0.00596 x 0.05682 mm, 14 faces (baked)
FEATURE [Part::Feature] Part__Feature349  label="COMPOUND067"
  shape: bbox 0.04636 x 0.00596 x 0.05682 mm, 16 faces (baked)
FEATURE [Part::Feature] Part__Feature350  label="COMPOUND068"
  shape: bbox 0.05124 x 0.00596 x 0.05682 mm, 16 faces (baked)
FEATURE [Part::Feature] Part__Feature351  label="COMPOUND069"
  shape: bbox 0.03063 x 0.00596 x 0.05682 mm, 14 faces (baked)
FEATURE [Part::Feature] Part__Feature352  label="COMPOUND070"
  shape: bbox 0.03268 x 0.004706 x 0.04249 mm, 24 faces (baked)
FEATURE [Part::Feature] Part__Feature353  label="COMPOUND071"
  shape: bbox 0.02747 x 0.004706 x 0.04249 mm, 23 faces (baked)
FEATURE [Part::Feature] Part__Feature354  label="COMPOUND072"
  shape: bbox 0.03904 x 0.006211 x 0.05969 mm, 17 faces (baked)
FEATURE [Part::Feature] Part__Feature355  label="COMPOUND073"
  shape: bbox 0.03063 x 0.00596 x 0.05682 mm, 14 faces (baked)
FEATURE [Part::Feature] Part__Feature356  label="COMPOUND074"
  shape: bbox 0.04636 x 0.00596 x 0.05682 mm, 16 faces (baked)
FEATURE [Part::Feature] Part__Feature357  label="COMPOUND075"
  shape: bbox 0.05124 x 0.00596 x 0.05682 mm, 16 faces (baked)
FEATURE [Part::Feature] Part__Feature358  label="COMPOUND076"
  shape: bbox 0.2583 x 0.01751 x 0.1888 mm, 37 faces (baked)
FEATURE [App::Part] COMPOUND006  label="COMPOUND077"
  Group = -> [Part__Feature345,Part__Feature346,Part__Feature347,Part__Feature348,Part__Feature349,Part__Feature350,Part__Feature351,Part__Feature352,Part__Feature353,Part__Feature354,Part__Feature355,Part__Feature356,Part__Feature357,Part__Feature358]
  Origin = -> Origin091
FEATURE [App::Part] SOD_323_L1_7_W1_3_LS2_5_RD  label="SOD-323_L1.7-W1.3-LS2.5-RD"
  Group = -> [COMPOUND006]
  Origin = -> Origin092
FEATURE [App::Part] pRkl_D2  label="pRkl-D2"
  Group = -> [SOD_323_L1_7_W1_3_LS2_5_RD]
  Origin = -> Origin093
  Placement = pos=(54.9911,26.2891,1.60005) rot=(0,0,1;0rad)
FEATURE [Part::Feature] Part__Feature359  label="SOLID007"
  shape: bbox 2.082 x 1.041 x 1.041 mm, 357 faces (baked)
FEATURE [App::Part] C0603
  Group = -> [Part__Feature359]
  Origin = -> Origin094
FEATURE [App::Part] pRkl_C6  label="pRkl-C6"
  Group = -> [C0603]
  Origin = -> Origin095
  Placement = pos=(80.8992,23.495,1.60005) rot=(0,0,1;0rad)
FEATURE [Part::Feature] Part__Feature360  label="COMPOUND078"
  shape: bbox 2.9 x 2.9 x 1.1 mm, 161 faces (baked)
FEATURE [Part::Feature] Part__Feature361  label="COMPOUND079"
  shape: bbox 0.06101 x 0.03218 x 0.001 mm, 8 faces (baked)
FEATURE [Part::Feature] Part__Feature362  label="COMPOUND080"
  shape: bbox 0.06307 x 0.04568 x 0.001 mm, 16 faces (baked)
FEATURE [Part::Feature] Part__Feature363  label="COMPOUND081"
  shape: bbox 0.06101 x 0.03281 x 0.001 mm, 14 faces (baked)
FEATURE [Part::Feature] Part__Feature364  label="COMPOUND082"
  shape: bbox 0.06101 x 0.04967 x 0.001 mm, 16 faces (baked)
FEATURE [Part::Feature] Part__Feature365  label="COMPOUND083"
  shape: bbox 0.06101 x 0.0549 x 0.001 mm, 16 faces (baked)
FEATURE [Part::Feature] Part__Feature366  label="COMPOUND084"
  shape: bbox 0.06101 x 0.03281 x 0.001 mm, 14 faces (baked)
FEATURE [Part::Feature] Part__Feature367  label="COMPOUND085"
  shape: bbox 0.0456 x 0.03501 x 0.001 mm, 24 faces (baked)
FEATURE [Part::Feature] Part__Feature368  label="COMPOUND086"
  shape: bbox 0.0456 x 0.02943 x 0.001 mm, 23 faces (baked)
FEATURE [Part::Feature] Part__Feature369  label="COMPOUND087"
  shape: bbox 0.0641 x 0.04183 x 0.001 mm, 17 faces (baked)
FEATURE [Part::Feature] Part__Feature370  label="COMPOUND088"
  shape: bbox 0.06101 x 0.03281 x 0.001 mm, 14 faces (baked)
FEATURE [Part::Feature] Part__Feature371  label="COMPOUND089"
  shape: bbox 0.06101 x 0.04967 x 0.001 mm, 16 faces (baked)
FEATURE [Part::Feature] Part__Feature372  label="COMPOUND090"
  shape: bbox 0.06101 x 0.0549 x 0.001 mm, 16 faces (baked)
FEATURE [Part::Feature] Part__Feature373  label="COMPOUND091"
  shape: bbox 0.203 x 0.2768 x 0.001 mm, 37 faces (baked)
FEATURE [App::Part] COMPOUND007  label="COMPOUND092"
  Group = -> [Part__Feature360,Part__Feature361,Part__Feature362,Part__Feature363,Part__Feature364,Part__Feature365,Part__Feature366,Part__Feature367,Part__Feature368,Part__Feature369,Part__Feature370,Part__Feature371,Part__Feature372,Part__Feature373]
  Origin = -> Origin096
FEATURE [App::Part] SOT_23_5_L2_9_W1_6_P0_95_LS2_8_BR  label="SOT-23-5_L2.9-W1.6-P0.95-LS2.8-BR"
  Group = -> [COMPOUND007]
  Origin = -> Origin097
FEATURE [App::Part] pRkl_U1  label="pRkl-U1"
  Group = -> [SOT_23_5_L2_9_W1_6_P0_95_LS2_8_BR]
  Origin = -> Origin098
  Placement = pos=(60.1981,23.622,1.60005) rot=(0,0,1;0rad)
FEATURE [Part::Feature] Part__Feature374  label="SOLID008"
  shape: bbox 10.57 x 2.5 x 11.7 mm, 358 faces (baked)
FEATURE [App::Part] HDR_TH_4P_P2_54_V_F  label="HDR-TH_4P-P2.54-V-F"
  Group = -> [Part__Feature374]
  Origin = -> Origin099
FEATURE [App::Part] pRkl_SCREEN  label="pRkl-SCREEN"
  Group = -> [HDR_TH_4P_P2_54_V_F]
  Origin = -> Origin100
  Placement = pos=(48.2601,22.225,1.60005) rot=(0,0,1;3.14159rad)
FEATURE [Part::Feature] Part__Feature375  label="COMPOUND093"
  shape: bbox 1.2 x 0.8001 x 0.4007 mm, 18 faces (baked)
FEATURE [Part::Feature] Part__Feature376  label="COMPOUND094"
  shape: bbox 0.46 x 0.8 x 0.22 mm, 26 faces (baked)
FEATURE [Part::Feature] Part__Feature377  label="COMPOUND095"
  shape: bbox 0.31 x 0.8 x 0.22 mm, 18 faces (baked)
FEATURE [Part::Feature] Part__Feature378  label="COMPOUND096"
  shape: bbox 1.6 x 0.81 x 0.5 mm, 294 faces (baked)
FEATURE [App::Part] COMPOUND008  label="COMPOUND097"
  Group = -> [Part__Feature375,Part__Feature376,Part__Feature377,Part__Feature378]
  Origin = -> Origin101
FEATURE [App::Part] LED0603_RD_RED  label="LED0603-RD_RED"
  Group = -> [COMPOUND008]
  Origin = -> Origin102
FEATURE [App::Part] pRkl_PWR  label="pRkl-PWR"
  Group = -> [LED0603_RD_RED]
  Origin = -> Origin103
  Placement = pos=(86.6142,37.0841,1.60005) rot=(0,0,1;0rad)
FEATURE [Part::Feature] Part__Feature379  label="COMPOUND098"
  shape: bbox 8.94 x 7.33 x 4.16 mm, 174 faces (baked)
FEATURE [Part::Feature] Part__Feature380  label="COMPOUND099"
  shape: bbox 8.94 x 6.75 x 3.61 mm, 133 faces (baked)
FEATURE [Part::Feature] Part__Feature381  label="COMPOUND100"
  shape: bbox 0.1073 x 0.2034 x 0.001 mm, 8 faces (baked)
FEATURE [Part::Feature] Part__Feature382  label="COMPOUND101"
  shape: bbox 0.1523 x 0.2102 x 0.001 mm, 16 faces (baked)
FEATURE [Part::Feature] Part__Feature383  label="COMPOUND102"
  shape: bbox 0.1094 x 0.2034 x 0.001 mm, 14 faces (baked)
FEATURE [Part::Feature] Part__Feature384  label="COMPOUND103"
  shape: bbox 0.1656 x 0.2034 x 0.001 mm, 16 faces (baked)
FEATURE [Part::Feature] Part__Feature385  label="COMPOUND104"
  shape: bbox 0.183 x 0.2034 x 0.001 mm, 16 faces (baked)
FEATURE [Part::Feature] Part__Feature386  label="COMPOUND105"
  shape: bbox 0.1094 x 0.2034 x 0.001 mm, 14 faces (baked)
FEATURE [Part::Feature] Part__Feature387  label="COMPOUND106"
  shape: bbox 0.1167 x 0.152 x 0.001 mm, 24 faces (baked)
FEATURE [Part::Feature] Part__Feature388  label="COMPOUND107"
  shape: bbox 0.0981 x 0.152 x 0.001 mm, 23 faces (baked)
FEATURE [Part::Feature] Part__Feature389  label="COMPOUND108"
  shape: bbox 0.1394 x 0.2137 x 0.001 mm, 17 faces (baked)
FEATURE [Part::Feature] Part__Feature390  label="COMPOUND109"
  shape: bbox 0.1094 x 0.2034 x 0.001 mm, 14 faces (baked)
FEATURE [Part::Feature] Part__Feature391  label="COMPOUND110"
  shape: bbox 0.1656 x 0.2034 x 0.001 mm, 16 faces (baked)
FEATURE [Part::Feature] Part__Feature392  label="COMPOUND111"
  shape: bbox 0.183 x 0.2034 x 0.001 mm, 16 faces (baked)
FEATURE [Part::Feature] Part__Feature393  label="COMPOUND112"
  shape: bbox 0.9225 x 0.6767 x 0.001 mm, 37 faces (baked)
FEATURE [App::Part] COMPOUND009  label="COMPOUND113"
  Group = -> [Part__Feature379,Part__Feature380,Part__Feature381,Part__Feature382,Part__Feature383,Part__Feature384,Part__Feature385,Part__Feature386,Part__Feature387,Part__Feature388,Part__Feature389,Part__Feature390,Part__Feature391,Part__Feature392,Part__Feature393]
  Origin = -> Origin104
FEATURE [App::Part] USB_C_SMD_TYPE_C_6PIN_2MD_073  label="USB-C-SMD_TYPE-C-6PIN-2MD-073"
  Group = -> [COMPOUND009]
  Origin = -> Origin105
FEATURE [App::Part] pRkl_USB2  label="pRkl-USB2"
  Group = -> [USB_C_SMD_TYPE_C_6PIN_2MD_073]
  Origin = -> Origin106
  Placement = pos=(70.8661,23.241,1.60005) rot=(0,0,1;0rad)
FEATURE [Part::Feature] Part__Feature394  label="COMPOUND114"
  shape: bbox 13.2 x 12.5 x 2.42 mm, 413 faces (baked)
FEATURE [Part::Feature] Part__Feature395  label="COMPOUND115"
  shape: bbox 0.1502 x 0.2847 x 0.001 mm, 8 faces (baked)
FEATURE [Part::Feature] Part__Feature396  label="COMPOUND116"
  shape: bbox 0.2132 x 0.2943 x 0.001 mm, 16 faces (baked)
FEATURE [Part::Feature] Part__Feature397  label="COMPOUND117"
  shape: bbox 0.1531 x 0.2847 x 0.001 mm, 14 faces (baked)
FEATURE [Part::Feature] Part__Feature398  label="COMPOUND118"
  shape: bbox 0.2318 x 0.2847 x 0.001 mm, 16 faces (baked)
FEATURE [Part::Feature] Part__Feature399  label="COMPOUND119"
  shape: bbox 0.2562 x 0.2847 x 0.001 mm, 16 faces (baked)
FEATURE [Part::Feature] Part__Feature400  label="COMPOUND120"
  shape: bbox 0.1531 x 0.2847 x 0.001 mm, 14 faces (baked)
FEATURE [Part::Feature] Part__Feature401  label="COMPOUND121"
  shape: bbox 0.1634 x 0.2128 x 0.001 mm, 24 faces (baked)
FEATURE [Part::Feature] Part__Feature402  label="COMPOUND122"
  shape: bbox 0.1373 x 0.2128 x 0.001 mm, 23 faces (baked)
FEATURE [Part::Feature] Part__Feature403  label="COMPOUND123"
  shape: bbox 0.1952 x 0.2991 x 0.001 mm, 17 faces (baked)
FEATURE [Part::Feature] Part__Feature404  label="COMPOUND124"
  shape: bbox 0.1531 x 0.2847 x 0.001 mm, 14 faces (baked)
FEATURE [Part::Feature] Part__Feature405  label="COMPOUND125"
  shape: bbox 0.2318 x 0.2847 x 0.001 mm, 16 faces (baked)
FEATURE [Part::Feature] Part__Feature406  label="COMPOUND126"
  shape: bbox 0.2562 x 0.2847 x 0.001 mm, 16 faces (baked)
FEATURE [Part::Feature] Part__Feature407  label="COMPOUND127"
  shape: bbox 1.292 x 0.9474 x 0.001 mm, 37 faces (baked)
FEATURE [App::Part] COMPOUND010  label="COMPOUND128"
  Group = -> [Part__Feature394,Part__Feature395,Part__Feature396,Part__Feature397,Part__Feature398,Part__Feature399,Part__Feature400,Part__Feature401,Part__Feature402,Part__Feature403,Part__Feature404,Part__Feature405,Part__Feature406,Part__Feature407]
  Origin = -> Origin107
FEATURE [App::Part] WIFIM_SMD_ESP32_C3_MINI_MINI_1U  label="WIFIM-SMD_ESP32-C3-MINI-MINI-1U"
  Group = -> [COMPOUND010]
  Origin = -> Origin108
FEATURE [App::Part] pRkl_U3  label="pRkl-U3"
  Group = -> [WIFIM_SMD_ESP32_C3_MINI_MINI_1U]
  Origin = -> Origin109
  Placement = pos=(52.7051,42.1641,1.60005) rot=(0,0,1;0rad)
FEATURE [Part::Feature] Part__Feature408  label="L0603"
  shape: bbox 0.762 x 0.762 x 0.762 mm, 6 faces (baked)
FEATURE [App::Part] pRkl_L1  label="pRkl-L1"
  Group = -> [Part__Feature408]
  Origin = -> Origin110
  Placement = pos=(68.7071,29.8451,1.60005) rot=(0,0,-1;1.5708rad)
FEATURE [Part::Feature] Part__Feature409  label="L0604"
  shape: bbox 0.762 x 0.762 x 0.762 mm, 6 faces (baked)
FEATURE [App::Part] pRkl_L2  label="pRkl-L2"
  Group = -> [Part__Feature409]
  Origin = -> Origin111
  Placement = pos=(70.7391,29.5911,1.60005) rot=(0,0,-1;1.5708rad)
FEATURE [Part::Feature] Part__Feature410  label="SOLID009"
  shape: bbox 29.25 x 5.953 x 9.727 mm, 258 faces (baked)
FEATURE [App::Part] FUSE_TH_BD5_5_L21_0_P28_00_D1_00  label="FUSE-TH_BD5.5-L21.0-P28.00-D1.00"
  Group = -> [Part__Feature410]
  Origin = -> Origin112
FEATURE [App::Part] pRkl_FUSE  label="pRkl-FUSE"
  Group = -> [FUSE_TH_BD5_5_L21_0_P28_00_D1_00]
  Origin = -> Origin113
  Placement = pos=(30.9881,61.9761,1.60005) rot=(0,0,-1;1.5708rad)
FEATURE [Part::Feature] Part__Feature411  label="SOLID010"
  shape: bbox 19.2 x 15.81 x 18.85 mm, 333 faces (baked)
FEATURE [App::Part] RELAY_TH_SRD_XXVDC_XL_C  label="RELAY-TH_SRD-XXVDC-XL-C"
  Group = -> [Part__Feature411]
  Origin = -> Origin114
FEATURE [App::Part] pRkl_K1  label="pRkl-K1"
  Group = -> [RELAY_TH_SRD_XXVDC_XL_C]
  Origin = -> Origin115
  Placement = pos=(67.5641,68.3261,1.60005) rot=(0,0,1;0rad)
FEATURE [Part::Feature] Part__Feature412  label="COMPOUND129"
  shape: bbox 1.2 x 0.8 x 0.33 mm, 18 faces (baked)
FEATURE [Part::Feature] Part__Feature413  label="COMPOUND130"
  shape: bbox 0.31 x 0.8 x 0.28 mm, 14 faces (baked)
FEATURE [Part::Feature] Part__Feature414  label="COMPOUND131"
  shape: bbox 0.51 x 0.8 x 0.28 mm, 20 faces (baked)
FEATURE [Part::Feature] Part__Feature415  label="COMPOUND132"
  shape: bbox 1.6 x 0.81 x 0.36 mm, 294 faces (baked)
FEATURE [App::Part] COMPOUND011  label="COMPOUND133"
  Group = -> [Part__Feature412,Part__Feature413,Part__Feature414,Part__Feature415]
  Origin = -> Origin116
FEATURE [App::Part] LED0603_RD_GREEN  label="LED0603-RD_GREEN"
  Group = -> [COMPOUND011]
  Origin = -> Origin117
FEATURE [App::Part] pRkl_SW  label="pRkl-SW"
  Group = -> [LED0603_RD_GREEN]
  Origin = -> Origin118
  Placement = pos=(86.6142,44.4501,1.60005) rot=(0,0,1;0rad)
FEATURE [App::Part] PCBModel
  Group = -> [TopSilk,BottomSilk,Part__Feature274,pRkl_C1,pRkl_C3,pRkl_C5,pRkl_Q1,pRkl_R10,pRkl_R11,pRkl_R2,pRkl_R3,pRkl_AC_DC_CONV,pRkl_R8,pRkl_R9,pRkl_BTN,pRkl_C4,pRkl_C2,pRkl_AC_OUT,pRkl_AC_IN,pRkl_D1,pRkl_SW2,pRkl_BOOT,pRkl_D2,pRkl_C6,pRkl_U1,pRkl_SCREEN,pRkl_PWR,pRkl_USB2,pRkl_U3,pRkl_L1,pRkl_L2,pRkl_FUSE,pRkl_K1,pRkl_SW]
  Origin = -> Origin119
  Placement = pos=(0,0,-40.5) rot=(0,0,1;0rad)
FEATURE [PartDesign::Pocket] Pocket031
  BaseFeature = -> Pad061
  Direction = (1,0,4e-16)
  Length = 4
  Length2 = 5
  Profile = -> Pad061 [Face65,Face62]
  Refine = true
  Type = 0
FEATURE [Sketcher::SketchObject] Sketch045
  ExternalGeometry = -> [Pocket031]
  FullyConstrained = true
  MapMode = 5
  Placement = pos=(0,0,0) rot=(1,0,0;3.14159rad)
  Support = -> [Pocket031]
  sketch-geometry (8):
    g0: LineSegment StartX=39.5 StartY=-65.35 StartZ=0 EndX=62.3 EndY=-65.35 EndZ=0
    g1: LineSegment StartX=62.3 StartY=-65.35 StartZ=0 EndX=62.3 EndY=-78.15 EndZ=0
    g2: LineSegment StartX=62.3 StartY=-78.15 StartZ=0 EndX=39.5 EndY=-78.15 EndZ=0
    g3: LineSegment StartX=39.5 StartY=-78.15 StartZ=0 EndX=39.5 EndY=-65.35 EndZ=0
    g4: LineSegment StartX=38.5 StartY=-64.35 StartZ=0 EndX=63.3 EndY=-64.35 EndZ=0
    g5: LineSegment StartX=63.3 StartY=-64.35 StartZ=0 EndX=63.3 EndY=-79.15 EndZ=0
    g6: LineSegment StartX=63.3 StartY=-79.15 StartZ=0 EndX=38.5 EndY=-79.15 EndZ=0
    g7: LineSegment StartX=38.5 StartY=-79.15 StartZ=0 EndX=38.5 EndY=-64.35 EndZ=0
  constraints (22):
    c: Coincident(g0,g1)
    c: Coincident(g1,g2)
    c: Coincident(g2,g3)
    c: Coincident(g3,g0)
    c: Horizontal(g0)
    c: Horizontal(g2)
    c: Vertical(g1)
    c: Vertical(g3)
    c: Coincident(g0,g-4)
    c: Coincident(g1,g-6)
    c: Coincident(g4,g5)
    c: Coincident(g5,g6)
    c: Coincident(g6,g7)
    c: Coincident(g7,g4)
    c: Horizontal(g4)
    c: Horizontal(g6)
    c: Vertical(g5)
    c: Vertical(g7)
    c: DistanceX(g0,g4) = 1
    c: DistanceX(g6,g2) = 1
    c: DistanceY(g0,g4) = 1
    c: DistanceY(g5,g1) = 1
FEATURE [PartDesign::Pad] Pad062
  BaseFeature = -> Pocket031
  Direction = (0,0,-1)
  Length = 1
  Length2 = 10
  Profile = -> Sketch045
  ReferenceAxis = -> Sketch045 [N_Axis]
  Refine = true
  Type = 0
FEATURE [PartDesign::Pocket] Pocket032
  BaseFeature = -> Pad060
  Direction = (0,0,-1)
  Length = 12
  Length2 = 5
  Profile = -> Pad060 [Face330]
  Refine = true
  Type = 0
FEATURE [PartDesign::Body] Body  label="Base"
  Group = -> [Sketch,Pad,Sketch001,Pad001,Sketch002,Pad002,Sketch003,Pad003,Pad004,Pad005,Pad006,Sketch004,Pad007,Sketch005,Pad008,Sketch006,Pad009,Sketch007,Pocket,Pad010,Pad011,Pad012,Pad013,Sketch022,Pocket007,Sketch024,Pocket009,Pad034,Sketch032,Pad039,Sketch033,Pad040,Sketch034,Pocket016,Fillet,Sketch035,Pad041,Sketch036,Pocket017,Fillet001,ShapeString,Pad042,ShapeString001,Pad043,Pad059,Pocket029,Pad060,+1 more]
  Origin = -> Origin049
  Placement = pos=(0,0,-50.89) rot=(0,0,1;0rad)
  Tip = -> Pocket032
FEATURE [PartDesign::Pad] Pad063
  BaseFeature = -> Pad062
  Direction = (0,0,-1)
  Length = 11.8
  Length2 = 10
  Profile = -> Pad062 [Face37]
  Refine = true
  Type = 0
FEATURE [PartDesign::Pad] Pad064
  BaseFeature = -> Pad063
  Direction = (0,-1,0)
  Length = 1
  Length2 = 10
  Profile = -> Pad063 [Face80]
  Refine = true
  Type = 0
FEATURE [Sketcher::SketchObject] Sketch046
  ExternalGeometry = -> [Pad064]
  FullyConstrained = true
  MapMode = 5
  Placement = pos=(93.9,9e-16,-5.6e-15) rot=(0.57735,0.57735,0.57735;2.0944rad)
  Support = -> [Pad064]
  sketch-geometry (1):
    g0: Circle CenterX=24.13 CenterY=-34.99 CenterZ=0 NormalX=0 NormalY=0 NormalZ=1 AngleXU=0 Radius=2.2
  constraints (3):
    c: Diameter(g0) = 4.4
    c: DistanceY(g-3,g0) = 5.61
    c: DistanceX(g0,g-3) = 5.97
FEATURE [PartDesign::Pocket] Pocket033
  BaseFeature = -> Pad064
  Direction = (-1,0,0)
  Length = 5
  Length2 = 5
  Profile = -> Sketch046
  ReferenceAxis = -> Sketch046 [N_Axis]
  Refine = true
  Type = 0
FEATURE [PartDesign::Pad] Pad065
  BaseFeature = -> Pocket033
  Direction = (0,0,1)
  Length = 1.7
  Length2 = 10
  Profile = -> Pocket033 [Face1089,Face1090,Face1091,Face1092,Face1093,Face1094,Face1095,Face1096,Face1105,Face1106,Face1107,Face1108,Face1110,Face1111,Face1109,Face1104,Face1103,Face1102,Face1099,Face1101,Face1100,Face1097,Face1098,Face1088,Face1087,Face1086,Face1085]
  Refine = true
  Type = 0
FEATURE [PartDesign::Pocket] Pocket034
  BaseFeature = -> Pad065
  Direction = (0,0,1)
  Length = 1
  Length2 = 5
  Profile = -> Pad065 [Face1129]
  Refine = true
  Type = 0
FEATURE [PartDesign::Pocket] Pocket035
  BaseFeature = -> Pocket034
  Direction = (0,0,1)
  Length = 1
  Length2 = 5
  Profile = -> Pocket034 [Face1110]
  Refine = true
  Type = 0
FEATURE [Sketcher::SketchObject] Sketch047
  ExternalGeometry = -> [Pocket035]
  FullyConstrained = true
  MapMode = 5
  Placement = pos=(0,0,-3) rot=(1,0,0;3.14159rad)
  Support = -> [Pocket035]
  sketch-geometry (4):
    g0: LineSegment StartX=35 StartY=-55.85 StartZ=0 EndX=66.8 EndY=-55.85 EndZ=0
    g1: LineSegment StartX=66.8 StartY=-55.85 StartZ=0 EndX=66.8 EndY=-84.65 EndZ=0
    g2: LineSegment StartX=66.8 StartY=-84.65 StartZ=0 EndX=35 EndY=-84.65 EndZ=0
    g3: LineSegment StartX=35 StartY=-84.65 StartZ=0 EndX=35 EndY=-55.85 EndZ=0
  constraints (12):
    c: Coincident(g0,g1)
    c: Coincident(g1,g2)
    c: Coincident(g2,g3)
    c: Coincident(g3,g0)
    c: Horizontal(g0)
    c: Horizontal(g2)
    c: Vertical(g1)
    c: Vertical(g3)
    c: PointOnObject(g0,g-4)
    c: PointOnObject(g1,g-5)
    c: PointOnObject(g-6,g0)
    c: PointOnObject(g-3,g2)
FEATURE [PartDesign::Pocket] Pocket036
  BaseFeature = -> Pocket035
  Direction = (0,0,1)
  Length = 2.99
  Length2 = 5
  Profile = -> Sketch047
  ReferenceAxis = -> Sketch047 [N_Axis]
  Refine = true
  Type = 0
FEATURE [Part::Part2DObjectPython] ShapeString012  # Draft 2D object (typed FeaturePython)
  FontFile = <userpath>/Documents/FreeCad/Fonts/Stencil_tenada/Tenada.ttf
  MakeFace = true
  Placement = pos=(9.94,53.93,2) rot=(0,0,1;0rad)
  Size = 2.7
  String = Smart Water Pump
  Tracking = 0
FEATURE [Part::Part2DObjectPython] ShapeString013  # Draft 2D object (typed FeaturePython)
  FontFile = <userpath>/Documents/FreeCad/Fonts/Stencil_tenada/Tenada.ttf
  MakeFace = true
  Placement = pos=(32,42.9,2) rot=(0,0,1;0rad)
  Size = 2.5
  String = Controller S1
  Tracking = 0
FEATURE [Sketcher::SketchObject] Sketch049
  FullyConstrained = true
  MapMode = 5
  Support = -> [XY_Plane120]
  sketch-geometry (10):
    g0: LineSegment StartX=21 StartY=100.55 StartZ=0 EndX=21 EndY=64.55 EndZ=0
    g1: LineSegment StartX=21 StartY=64.55 StartZ=0 EndX=4.2 EndY=64.55 EndZ=0
    g2: LineSegment StartX=93.5 StartY=15.2 StartZ=0 EndX=93.5 EndY=65.2 EndZ=0
    g3: LineSegment StartX=93.5 StartY=65.2 StartZ=0 EndX=80.9 EndY=65.2 EndZ=0
    g4: LineSegment StartX=80.9 StartY=65.2 StartZ=0 EndX=80.9 EndY=100.55 EndZ=0
    g5: LineSegment StartX=80.9 StartY=100.55 StartZ=0 EndX=21 EndY=100.55 EndZ=0
    g6: LineSegment StartX=93.5 StartY=15.2 StartZ=0 EndX=30 EndY=15.2 EndZ=0
    g7: LineSegment StartX=30 StartY=15.2 StartZ=0 EndX=30 EndY=49.55 EndZ=0
    g8: LineSegment StartX=30 StartY=49.55 StartZ=0 EndX=4.2 EndY=49.55 EndZ=0
    g9: LineSegment StartX=4.2 StartY=49.55 StartZ=0 EndX=4.2 EndY=64.55 EndZ=0
  constraints (30):
    c: Vertical(g0)
    c: Coincident(g0,g1)
    c: Horizontal(g1)
    c: Vertical(g2)
    c: Coincident(g2,g3)
    c: Coincident(g3,g4)
    c: Vertical(g4)
    c: Coincident(g4,g5)
    c: Coincident(g5,g0)
    c: Horizontal(g5)
    c: Horizontal(g3)
    c: Coincident(g2,g6)
    c: Horizontal(g6)
    c: Coincident(g6,g7)
    c: Vertical(g7)
    c: Coincident(g7,g8)
    c: Horizontal(g8)
    c: Coincident(g8,g9)
    c: Coincident(g9,g1)
    c: Vertical(g9)
    c: DistanceY(g-1,g6) = 15.2
    c: DistanceX(g-1,g6) = 30
    c: DistanceX(g8,g7) = 25.8
    c: DistanceX(g6,g6) = 63.5
    c: DistanceY(g2,g2) = 50
    c: DistanceY(g7,g7) = 34.35
    c: DistanceY(g9,g9) = 15
    c: DistanceY(g0,g0) = 36
    c: DistanceX(g5,g5) = 59.9
    c: DistanceX(g3,g3) = 12.6
FEATURE [PartDesign::Pad] Pad066
  Direction = (0,0,1)
  Length = 2
  Length2 = 10
  Profile = -> Sketch049
  ReferenceAxis = -> Sketch049 [N_Axis]
  Refine = true
  Type = 0
FEATURE [Sketcher::SketchObject] Sketch050
  FullyConstrained = false
  MapMode = 5
  Support = -> [XY_Plane121]
  sketch-geometry (4):
    g0: LineSegment StartX=4.34912 StartY=50.7797 StartZ=0 EndX=32.5138 EndY=50.7797 EndZ=0
    g1: LineSegment StartX=32.5138 StartY=50.7797 StartZ=0 EndX=32.5138 EndY=14.7356 EndZ=0
    g2: LineSegment StartX=32.5138 StartY=14.7356 StartZ=0 EndX=4.34912 EndY=14.7356 EndZ=0
    g3: LineSegment StartX=4.34912 StartY=14.7356 StartZ=0 EndX=4.34912 EndY=50.7797 EndZ=0
  constraints (8):
    c: Coincident(g0,g1)
    c: Coincident(g1,g2)
    c: Coincident(g2,g3)
    c: Coincident(g3,g0)
    c: Horizontal(g0)
    c: Horizontal(g2)
    c: Vertical(g1)
    c: Vertical(g3)
FEATURE [PartDesign::Pad] Pad067
  Direction = (0,0,1)
  Length = 2
  Length2 = 10
  Profile = -> Sketch050
  ReferenceAxis = -> Sketch050 [N_Axis]
  Refine = true
  Type = 0
FEATURE [Sketcher::SketchObject] Sketch051
  ExternalGeometry = -> [Pad067]
  FullyConstrained = true
  MapMode = 5
  Placement = pos=(0,0,0) rot=(1,0,0;3.14159rad)
  Support = -> [Pad067]
  sketch-geometry (6):
    g0: LineSegment StartX=4.34912 StartY=-50.7797 StartZ=0 EndX=4.34912 EndY=-14.7356 EndZ=0
    g1: LineSegment StartX=4.34912 StartY=-14.7356 StartZ=0 EndX=32.5138 EndY=-14.7356 EndZ=0
    g2: LineSegment StartX=32.5138 StartY=-14.7356 StartZ=0 EndX=32.5138 EndY=-16.2356 EndZ=0
    g3: LineSegment StartX=32.5138 StartY=-16.2356 StartZ=0 EndX=5.84912 EndY=-16.2356 EndZ=0
    g4: LineSegment StartX=5.84912 StartY=-16.2356 StartZ=0 EndX=5.84912 EndY=-50.7797 EndZ=0
    g5: LineSegment StartX=5.84912 StartY=-50.7797 StartZ=0 EndX=4.34912 EndY=-50.7797 EndZ=0
  constraints (15):
    c: Coincident(g-3,g0)
    c: Coincident(g0,g-4)
    c: Coincident(g0,g1)
    c: Coincident(g1,g-4)
    c: Coincident(g1,g2)
    c: Vertical(g2)
    c: Coincident(g2,g3)
    c: Horizontal(g3)
    c: Coincident(g3,g4)
    c: Vertical(g4)
    c: Coincident(g4,g5)
    c: Coincident(g5,g0)
    c: DistanceY(g2,g1) = 1.5
    c: DistanceX(g0,g4) = 1.5
    c: PointOnObject(g4,g-5)
FEATURE [PartDesign::Pad] Pad068
  BaseFeature = -> Pad067
  Direction = (0,0,-1)
  Length = 22
  Length2 = 10
  Profile = -> Sketch051
  ReferenceAxis = -> Sketch051 [N_Axis]
  Refine = true
  Type = 0
FEATURE [Sketcher::SketchObject] Sketch052
  ExternalGeometry = -> [Pad068]
  FullyConstrained = true
  MapMode = 5
  Placement = pos=(0,0,2) rot=(0,0,1;0rad)
  Support = -> [Pad068]
  sketch-geometry (4):
    g0: LineSegment StartX=9.59912 StartY=43.7856 StartZ=0 EndX=25.0991 EndY=43.7856 EndZ=0
    g1: LineSegment StartX=25.0991 StartY=43.7856 StartZ=0 EndX=25.0991 EndY=22.4856 EndZ=0
    g2: LineSegment StartX=25.0991 StartY=22.4856 StartZ=0 EndX=9.59912 EndY=22.4856 EndZ=0
    g3: LineSegment StartX=9.59912 StartY=22.4856 StartZ=0 EndX=9.59912 EndY=43.7856 EndZ=0
  constraints (12):
    c: Coincident(g0,g1)
    c: Coincident(g1,g2)
    c: Coincident(g2,g3)
    c: Coincident(g3,g0)
    c: Horizontal(g0)
    c: Horizontal(g2)
    c: Vertical(g1)
    c: Vertical(g3)
    c: DistanceX(g0,g0) = 15.5
    c: DistanceY(g1,g0) = 21.3
    c: DistanceY(g-4,g2) = 7.75
    c: DistanceX(g-4,g2) = 5.25
FEATURE [PartDesign::Pocket] Pocket038
  BaseFeature = -> Pad068
  Direction = (0,0,-1)
  Length = 5
  Length2 = 5
  Profile = -> Sketch052
  ReferenceAxis = -> Sketch052 [N_Axis]
  Refine = true
  Type = 0
FEATURE [PartDesign::Pad] Pad072
  BaseFeature = -> Pocket038
  Direction = (0,-1,0)
  Length = 0.5
  Length2 = 10
  Profile = -> Pocket038 [Face5]
  Refine = true
  Type = 0
FEATURE [PartDesign::Pad] Pad073
  BaseFeature = -> Pad072
  Direction = (-1,0,0)
  Length = 0.5
  Length2 = 10
  Profile = -> Pad072 [Face11]
  Refine = true
  Type = 0
FEATURE [PartDesign::Pocket] Pocket053
  BaseFeature = -> Pad073
  Direction = (0,-1,-1e-16)
  Length = 1
  Length2 = 5
  Profile = -> Pad073 [Face9]
  Refine = true
  Type = 0
FEATURE [PartDesign::Pocket] Pocket054
  BaseFeature = -> Pocket053
  Direction = (-1,0,0)
  Length = 1
  Length2 = 5
  Profile = -> Pocket053 [Face1]
  Refine = true
  Type = 0
FEATURE [PartDesign::Fillet] Fillet005
  Base = -> Pocket054 [Edge27,Edge22,Edge25,Edge23]
  BaseFeature = -> Pocket054
  Radius = 1
  Refine = true
  SupportTransform = false
  UseAllEdges = false
FEATURE [PartDesign::Pad] Pad091
  BaseFeature = -> Fillet005
  Direction = (0,0,1)
  Length = 2
  Length2 = 10
  Profile = -> Fillet005 [Face14]
  Refine = true
  Type = 0
FEATURE [PartDesign::Pocket] Pocket055
  BaseFeature = -> Pad091
  Direction = (0,0,1)
  Length = 2
  Length2 = 5
  Profile = -> Pad091 [Face1]
  Refine = true
  Type = 0
FEATURE [PartDesign::Body] Body004  label="LidBoton001"
  Group = -> [Sketch050,Pad067,Sketch051,Pad068,Sketch052,Pocket038,Pad072,Pad073,Pocket053,Pocket054,Fillet005,Pad091,Pocket055]
  Origin = -> Origin121
  Placement = pos=(-0.2,0.465,-28.99) rot=(0,0,1;0rad)
  Tip = -> Pocket055
FEATURE [Sketcher::SketchObject] Sketch053
  ExternalGeometry = -> [Pad066]
  FullyConstrained = true
  MapMode = 5
  Placement = pos=(0,0,0) rot=(1,0,0;3.14159rad)
  Support = -> [Pad066]
  sketch-geometry (8):
    g0: LineSegment StartX=30 StartY=-15.2 StartZ=0 EndX=93.5 EndY=-15.2 EndZ=0
    g1: LineSegment StartX=93.5 StartY=-15.2 StartZ=0 EndX=93.5 EndY=-16.7 EndZ=0
    g2: LineSegment StartX=93.5 StartY=-16.7 StartZ=0 EndX=30 EndY=-16.7 EndZ=0
    g3: LineSegment StartX=30 StartY=-16.7 StartZ=0 EndX=30 EndY=-15.2 EndZ=0
    g4: LineSegment StartX=21 StartY=-100.55 StartZ=0 EndX=80.9 EndY=-100.55 EndZ=0
    g5: LineSegment StartX=80.9 StartY=-100.55 StartZ=0 EndX=80.9 EndY=-99.35 EndZ=0
    g6: LineSegment StartX=80.9 StartY=-99.35 StartZ=0 EndX=21 EndY=-99.35 EndZ=0
    g7: LineSegment StartX=21 StartY=-99.35 StartZ=0 EndX=21 EndY=-100.55 EndZ=0
  constraints (22):
    c: Coincident(g0,g1)
    c: Coincident(g1,g2)
    c: Coincident(g2,g3)
    c: Coincident(g3,g0)
    c: Horizontal(g0)
    c: Horizontal(g2)
    c: Vertical(g1)
    c: Vertical(g3)
    c: Coincident(g0,g-4)
    c: PointOnObject(g1,g-5)
    c: DistanceY(g1,g1) = 1.5
    c: Coincident(g4,g5)
    c: Coincident(g5,g6)
    c: Coincident(g6,g7)
    c: Coincident(g7,g4)
    c: Horizontal(g4)
    c: Horizontal(g6)
    c: Vertical(g5)
    c: Vertical(g7)
    c: Coincident(g4,g-10)
    c: DistanceY(g5,g5) = 1.2
    c: PointOnObject(g5,g-11)
FEATURE [PartDesign::Pad] Pad069
  BaseFeature = -> Pad066
  Direction = (0,0,-1)
  Length = 51
  Length2 = 10
  Profile = -> Sketch053
  ReferenceAxis = -> Sketch053 [N_Axis]
  Refine = true
  Type = 0
FEATURE [PartDesign::Pad] Pad070
  BaseFeature = -> Pad069
  Direction = (0,1,0)
  Length = 0.6
  Length2 = 10
  Profile = -> Pad069 [Face16]
  Refine = true
  Type = 0
FEATURE [PartDesign::Pad] Pad071
  BaseFeature = -> Pad070
  Direction = (0,-1,0)
  Length = 0.5
  Length2 = 10
  Profile = -> Pad070 [Face4]
  Refine = true
  Type = 0
FEATURE [Sketcher::SketchObject] Sketch054
  ExternalGeometry = -> [Pad071]
  FullyConstrained = true
  MapMode = 5
  Placement = pos=(0,0,0) rot=(1,0,0;3.14159rad)
  Support = -> [Pad071]
  sketch-geometry (6):
    g0: LineSegment StartX=30 StartY=-16.7 StartZ=0 EndX=32 EndY=-16.7 EndZ=0
    g1: LineSegment StartX=32 StartY=-16.7 StartZ=0 EndX=32 EndY=-51.55 EndZ=0
    g2: LineSegment StartX=32 StartY=-51.55 StartZ=0 EndX=4.2 EndY=-51.55 EndZ=0
    g3: LineSegment StartX=4.2 StartY=-51.55 StartZ=0 EndX=4.2 EndY=-49.55 EndZ=0
    g4: LineSegment StartX=4.2 StartY=-49.55 StartZ=0 EndX=30 EndY=-49.55 EndZ=0
    g5: LineSegment StartX=30 StartY=-49.55 StartZ=0 EndX=30 EndY=-16.7 EndZ=0
  constraints (15):
    c: Coincident(g-4,g0)
    c: PointOnObject(g0,g-4)
    c: Coincident(g0,g1)
    c: Vertical(g1)
    c: Coincident(g1,g2)
    c: Horizontal(g2)
    c: Coincident(g2,g3)
    c: Coincident(g3,g-5)
    c: Coincident(g3,g4)
    c: Coincident(g4,g-5)
    c: Coincident(g4,g5)
    c: Coincident(g5,g0)
    c: Vertical(g3)
    c: DistanceY(g3,g3) = 2
    c: DistanceX(g0,g0) = 2
FEATURE [PartDesign::Pad] Pad074
  BaseFeature = -> Pad071
  Direction = (0,0,-1)
  Length = 29
  Length2 = 10
  Profile = -> Sketch054
  ReferenceAxis = -> Sketch054 [N_Axis]
  Refine = true
  Type = 0
FEATURE [Sketcher::SketchObject] Sketch055
  ExternalGeometry = -> [Pad074]
  FullyConstrained = true
  MapMode = 5
  Placement = pos=(0,0,0) rot=(1,0,0;3.14159rad)
  Support = -> [Pad074]
  sketch-geometry (4):
    g0: LineSegment StartX=4.2 StartY=-64.55 StartZ=0 EndX=6.2 EndY=-64.55 EndZ=0
    g1: LineSegment StartX=6.2 StartY=-64.55 StartZ=0 EndX=6.2 EndY=-51.55 EndZ=0
    g2: LineSegment StartX=6.2 StartY=-51.55 StartZ=0 EndX=4.2 EndY=-51.55 EndZ=0
    g3: LineSegment StartX=4.2 StartY=-51.55 StartZ=0 EndX=4.2 EndY=-64.55 EndZ=0
  constraints (11):
    c: Coincident(g0,g1)
    c: Coincident(g1,g2)
    c: Coincident(g2,g3)
    c: Coincident(g3,g0)
    c: Horizontal(g0)
    c: Horizontal(g2)
    c: Vertical(g1)
    c: Vertical(g3)
    c: Coincident(g0,g-4)
    c: PointOnObject(g1,g-5)
    c: DistanceX(g2,g2) = 2
FEATURE [PartDesign::Pad] Pad075
  BaseFeature = -> Pad074
  Direction = (0,0,-1)
  Length = 51
  Length2 = 10
  Profile = -> Sketch055
  ReferenceAxis = -> Sketch055 [N_Axis]
  Refine = true
  Type = 0
FEATURE [PartDesign::Pocket] Pocket039
  BaseFeature = -> Pad075
  Direction = (0,-1,0)
  Length = 1.5
  Length2 = 5
  Profile = -> Pad075 [Face21]
  Refine = true
  Type = 0
FEATURE [PartDesign::Pad] Pad076
  BaseFeature = -> Pocket039
  Direction = (-1,0,0)
  Length = 0.55
  Length2 = 10
  Profile = -> Pocket039 [Face18]
  Refine = true
  Type = 0
FEATURE [PartDesign::Pad] Pad077
  BaseFeature = -> Pad076
  Direction = (0,-1,0)
  Length = 1
  Length2 = 10
  Profile = -> Pad076 [Face19]
  Refine = true
  Type = 0
FEATURE [Sketcher::SketchObject] Sketch056
  ExternalGeometry = -> [Pad077]
  FullyConstrained = true
  MapMode = 5
  Placement = pos=(0,0,0) rot=(1,0,0;3.14159rad)
  Support = -> [Pad077]
  sketch-geometry (6):
    g0: LineSegment StartX=6.2 StartY=-63.05 StartZ=0 EndX=21 EndY=-63.05 EndZ=0
    g1: LineSegment StartX=21 StartY=-63.05 StartZ=0 EndX=21 EndY=-99.35 EndZ=0
    g2: LineSegment StartX=21 StartY=-99.35 StartZ=0 EndX=23 EndY=-99.35 EndZ=0
    g3: LineSegment StartX=23 StartY=-99.35 StartZ=0 EndX=23 EndY=-61.05 EndZ=0
    g4: LineSegment StartX=23 StartY=-61.05 StartZ=0 EndX=6.2 EndY=-61.05 EndZ=0
    g5: LineSegment StartX=6.2 StartY=-61.05 StartZ=0 EndX=6.2 EndY=-63.05 EndZ=0
  constraints (15):
    c: Coincident(g-4,g0)
    c: Coincident(g0,g-4)
    c: Coincident(g0,g1)
    c: Coincident(g1,g-3)
    c: Coincident(g1,g2)
    c: Horizontal(g2)
    c: Coincident(g2,g3)
    c: Vertical(g3)
    c: Coincident(g3,g4)
    c: Horizontal(g4)
    c: Coincident(g4,g5)
    c: Coincident(g5,g0)
    c: Vertical(g5)
    c: DistanceX(g2,g2) = 2
    c: DistanceY(g5,g5) = 2
FEATURE [PartDesign::Pad] Pad078
  BaseFeature = -> Pad077
  Direction = (0,0,-1)
  Length = 38.6
  Length2 = 10
  Profile = -> Sketch056
  ReferenceAxis = -> Sketch056 [N_Axis]
  Refine = true
  Type = 0
FEATURE [Sketcher::SketchObject] Sketch057
  ExternalGeometry = -> [Pad078]
  FullyConstrained = true
  MapMode = 5
  Placement = pos=(0,0,0) rot=(1,0,0;3.14159rad)
  Support = -> [Pad078]
  sketch-geometry (4):
    g0: LineSegment StartX=93.5 StartY=-65.2 StartZ=0 EndX=91.5 EndY=-65.2 EndZ=0
    g1: LineSegment StartX=91.5 StartY=-65.2 StartZ=0 EndX=91.5 EndY=-16.7 EndZ=0
    g2: LineSegment StartX=91.5 StartY=-16.7 StartZ=0 EndX=93.5 EndY=-16.7 EndZ=0
    g3: LineSegment StartX=93.5 StartY=-16.7 StartZ=0 EndX=93.5 EndY=-65.2 EndZ=0
  constraints (11):
    c: Coincident(g0,g1)
    c: Coincident(g1,g2)
    c: Coincident(g2,g3)
    c: Coincident(g3,g0)
    c: Horizontal(g0)
    c: Horizontal(g2)
    c: Vertical(g1)
    c: Vertical(g3)
    c: Coincident(g0,g-5)
    c: PointOnObject(g1,g-4)
    c: DistanceX(g0,g0) = 2
FEATURE [PartDesign::Pad] Pad079
  BaseFeature = -> Pad078
  Direction = (0,0,-1)
  Length = 28.7
  Length2 = 10
  Profile = -> Sketch057
  ReferenceAxis = -> Sketch057 [N_Axis]
  Refine = true
  Type = 0
FEATURE [Sketcher::SketchObject] Sketch058
  ExternalGeometry = -> [Pad079]
  FullyConstrained = true
  MapMode = 5
  Placement = pos=(0,0,-28.7) rot=(1,0,0;3.14159rad)
  Support = -> [Pad079]
  sketch-geometry (4):
    g0: LineSegment StartX=91.5 StartY=-65.2 StartZ=0 EndX=93.5 EndY=-65.2 EndZ=0
    g1: LineSegment StartX=93.5 StartY=-65.2 StartZ=0 EndX=93.5 EndY=-30.4 EndZ=0
    g2: LineSegment StartX=93.5 StartY=-30.4 StartZ=0 EndX=91.5 EndY=-30.4 EndZ=0
    g3: LineSegment StartX=91.5 StartY=-30.4 StartZ=0 EndX=91.5 EndY=-65.2 EndZ=0
  constraints (11):
    c: Coincident(g0,g1)
    c: Coincident(g1,g2)
    c: Coincident(g2,g3)
    c: Coincident(g3,g0)
    c: Horizontal(g0)
    c: Horizontal(g2)
    c: Vertical(g1)
    c: Vertical(g3)
    c: Coincident(g0,g-5)
    c: PointOnObject(g1,g-3)
    c: DistanceY(g1,g1) = 34.8
FEATURE [PartDesign::Pad] Pad080
  BaseFeature = -> Pad079
  Direction = (0,0,-1)
  Length = 22.4
  Length2 = 10
  Profile = -> Sketch058
  ReferenceAxis = -> Sketch058 [N_Axis]
  Refine = true
  Type = 0
FEATURE [PartDesign::Pocket] Pocket040
  BaseFeature = -> Pad080
  Direction = (0,-1,0)
  Length = 1.9
  Length2 = 5
  Profile = -> Pad080 [Face27]
  Refine = true
  Type = 0
FEATURE [Sketcher::SketchObject] Sketch059
  ExternalGeometry = -> [Pocket040]
  FullyConstrained = true
  MapMode = 5
  Placement = pos=(0,0,0) rot=(1,0,0;3.14159rad)
  Support = -> [Pocket040]
  sketch-geometry (4):
    g0: LineSegment StartX=80.9 StartY=-63.3 StartZ=0 EndX=78.9 EndY=-63.3 EndZ=0
    g1: LineSegment StartX=78.9 StartY=-63.3 StartZ=0 EndX=78.9 EndY=-99.35 EndZ=0
    g2: LineSegment StartX=78.9 StartY=-99.35 StartZ=0 EndX=80.9 EndY=-99.35 EndZ=0
    g3: LineSegment StartX=80.9 StartY=-99.35 StartZ=0 EndX=80.9 EndY=-63.3 EndZ=0
  constraints (11):
    c: Coincident(g0,g1)
    c: Coincident(g1,g2)
    c: Coincident(g2,g3)
    c: Coincident(g3,g0)
    c: Horizontal(g0)
    c: Horizontal(g2)
    c: Vertical(g1)
    c: Vertical(g3)
    c: Coincident(g0,g-3)
    c: PointOnObject(g1,g-4)
    c: DistanceX(g0,g0) = 2
FEATURE [PartDesign::Pad] Pad081
  BaseFeature = -> Pocket040
  Direction = (0,0,-1)
  Length = 38.6
  Length2 = 10
  Profile = -> Sketch059
  ReferenceAxis = -> Sketch059 [N_Axis]
  Refine = true
  Type = 0
FEATURE [Sketcher::SketchObject] Sketch060
  ExternalGeometry = -> [Pad081]
  FullyConstrained = true
  MapMode = 5
  Placement = pos=(0,63.3,0) rot=(0,0.707107,0.707107;3.14159rad)
  Support = -> [Pad081]
  sketch-geometry (4):
    g0: LineSegment StartX=-93.5 StartY=2 StartZ=0 EndX=-91.5 EndY=2 EndZ=0
    g1: LineSegment StartX=-91.5 StartY=2 StartZ=0 EndX=-91.5 EndY=-38 EndZ=0
    g2: LineSegment StartX=-91.5 StartY=-38 StartZ=0 EndX=-93.5 EndY=-38 EndZ=0
    g3: LineSegment StartX=-93.5 StartY=-38 StartZ=0 EndX=-93.5 EndY=2 EndZ=0
  constraints (11):
    c: Coincident(g0,g1)
    c: Coincident(g1,g2)
    c: Coincident(g2,g3)
    c: Coincident(g3,g0)
    c: Horizontal(g0)
    c: Horizontal(g2)
    c: Vertical(g1)
    c: Vertical(g3)
    c: Coincident(g0,g-4)
    c: PointOnObject(g1,g-6)
    c: DistanceY(g3,g3) = 40
FEATURE [PartDesign::Pad] Pad082
  BaseFeature = -> Pad081
  Direction = (0,1,-2e-16)
  Length = 2.8
  Length2 = 10
  Profile = -> Sketch060
  ReferenceAxis = -> Sketch060 [N_Axis]
  Refine = true
  Type = 0
FEATURE [Sketcher::SketchObject] Sketch061
  ExternalGeometry = -> [Pad082]
  FullyConstrained = true
  MapMode = 5
  Placement = pos=(91.5,0,0) rot=(0.57735,-0.57735,-0.57735;2.0944rad)
  Support = -> [Pad082]
  sketch-geometry (4):
    g0: LineSegment StartX=-66.1 StartY=-38 StartZ=0 EndX=-64.6 EndY=-38 EndZ=0
    g1: LineSegment StartX=-64.6 StartY=-38 StartZ=0 EndX=-64.6 EndY=2 EndZ=0
    g2: LineSegment StartX=-64.6 StartY=2 StartZ=0 EndX=-66.1 EndY=2 EndZ=0
    g3: LineSegment StartX=-66.1 StartY=2 StartZ=0 EndX=-66.1 EndY=-38 EndZ=0
  constraints (11):
    c: Coincident(g0,g1)
    c: Coincident(g1,g2)
    c: Coincident(g2,g3)
    c: Coincident(g3,g0)
    c: Horizontal(g0)
    c: Horizontal(g2)
    c: Vertical(g1)
    c: Vertical(g3)
    c: Coincident(g0,g-5)
    c: PointOnObject(g1,g-4)
    c: DistanceX(g2,g2) = 1.5
FEATURE [PartDesign::Pad] Pad083
  BaseFeature = -> Pad082
  Direction = (-1,0,0)
  Length = 11
  Length2 = 10
  Profile = -> Sketch061
  ReferenceAxis = -> Sketch061 [N_Axis]
  Refine = true
  Type = 0
FEATURE [PartDesign::Pad] Pad084
  BaseFeature = -> Pad083
  Direction = (0,1,0)
  Length = 2
  Length2 = 10
  Profile = -> Pad083 [Face11]
  Refine = true
  Type = 0
FEATURE [PartDesign::Pocket] Pocket041
  BaseFeature = -> Pad084
  Direction = (-1,0,0)
  Length = 0.6
  Length2 = 5
  Profile = -> Pad084 [Face4]
  Refine = true
  Type = 0
FEATURE [PartDesign::Pocket] Pocket042
  BaseFeature = -> Pocket041
  Direction = (1,0,0)
  Length = 0.4
  Length2 = 5
  Profile = -> Pocket041 [Face10]
  Refine = true
  Type = 0
FEATURE [PartDesign::Pad] Pad085
  BaseFeature = -> Pocket042
  Direction = (1,0,-1e-16)
  Length = 0.4
  Length2 = 10
  Profile = -> Pocket042 [Face21]
  Refine = true
  Type = 0
FEATURE [Sketcher::SketchObject] Sketch062
  ExternalGeometry = -> [Pad085]
  FullyConstrained = true
  MapMode = 5
  Placement = pos=(93.9,1.9e-15,-1.13e-14) rot=(0.57735,0.57735,0.57735;2.0944rad)
  Support = -> [Pad085]
  sketch-geometry (1):
    g0: Circle CenterX=52.6 CenterY=-47.4 CenterZ=0 NormalX=0 NormalY=0 NormalZ=1 AngleXU=0 Radius=1.5
  constraints (3):
    c: Diameter(g0) = 3
    c: DistanceY(g-4,g0) = 3.7
    c: DistanceX(g0,g-4) = 10.7
FEATURE [PartDesign::Pocket] Pocket043
  BaseFeature = -> Pad085
  Direction = (-1,1e-16,1e-16)
  Length = 5
  Length2 = 5
  Profile = -> Sketch062
  ReferenceAxis = -> Sketch062 [N_Axis]
  Refine = true
  Type = 0
FEATURE [Sketcher::SketchObject] Sketch063
  ExternalGeometry = -> [Pocket043]
  FullyConstrained = true
  MapMode = 5
  Placement = pos=(3.65,0,0) rot=(0.57735,-0.57735,-0.57735;2.0944rad)
  Support = -> [Pocket043]
  sketch-geometry (1):
    g0: Circle CenterX=-57.43 CenterY=-47.38 CenterZ=0 NormalX=0 NormalY=0 NormalZ=1 AngleXU=0 Radius=1.5
  constraints (3):
    c: Diameter(g0) = 3
    c: DistanceY(g-3,g0) = 3.62
    c: DistanceX(g-3,g0) = 5.62
FEATURE [PartDesign::Pocket] Pocket044
  BaseFeature = -> Pocket043
  Direction = (1,0,0)
  Length = 5
  Length2 = 5
  Profile = -> Sketch063
  ReferenceAxis = -> Sketch063 [N_Axis]
  Refine = true
  Type = 0
FEATURE [PartDesign::Pocket] Pocket045
  BaseFeature = -> Pocket044
  Direction = (1,0,0)
  Length = 0.5
  Length2 = 5
  Profile = -> Pocket044 [Face19]
  Refine = true
  Type = 0
FEATURE [PartDesign::Pocket] Pocket046
  BaseFeature = -> Pocket045
  Direction = (0,1,0)
  Length = 1.2
  Length2 = 5
  Profile = -> Pocket045 [Face1]
  Refine = true
  Type = 0
FEATURE [Sketcher::SketchObject] Sketch064
  ExternalGeometry = -> [Pocket046]
  FullyConstrained = true
  MapMode = 5
  Placement = pos=(0,1e-16,2) rot=(0,0,1;0rad)
  Support = -> [Pocket046]
  sketch-geometry (2):
    g0: Circle CenterX=85.55 CenterY=36.6 CenterZ=0 NormalX=0 NormalY=0 NormalZ=1 AngleXU=0 Radius=2.5
    g1: Circle CenterX=85.55 CenterY=44 CenterZ=0 NormalX=0 NormalY=0 NormalZ=1 AngleXU=0 Radius=2.5
  constraints (6):
    c: Diameter(g1) = 5
    c: Diameter(g0) = 5
    c: DistanceY(g0,g1) = 7.4
    c: DistanceY(g-4,g0) = 21.9
    c: DistanceX(g0,g-4) = 8.35
    c: DistanceX(g1,g0) = 0
FEATURE [PartDesign::Pocket] Pocket047
  BaseFeature = -> Pocket046
  Direction = (0,0,-1)
  Length = 5
  Length2 = 5
  Profile = -> Sketch064
  ReferenceAxis = -> Sketch064 [N_Axis]
  Refine = true
  Type = 0
FEATURE [Sketcher::SketchObject] Sketch065
  ExternalGeometry = -> [Pocket047]
  FullyConstrained = true
  MapMode = 5
  Placement = pos=(0,0,0) rot=(1,0,0;3.14159rad)
  Support = -> [Pocket047]
  sketch-geometry (4):
    g0: Circle CenterX=85.55 CenterY=-36.6 CenterZ=0 NormalX=0 NormalY=0 NormalZ=1 AngleXU=0 Radius=2.5
    g1: Circle CenterX=85.55 CenterY=-44 CenterZ=0 NormalX=0 NormalY=0 NormalZ=1 AngleXU=0 Radius=2.5
    g2: Circle CenterX=85.55 CenterY=-36.6 CenterZ=0 NormalX=0 NormalY=0 NormalZ=1 AngleXU=0 Radius=4
    g3: Circle CenterX=85.55 CenterY=-44 CenterZ=0 NormalX=0 NormalY=0 NormalZ=1 AngleXU=0 Radius=4
  constraints (8):
    c: Coincident(g0,g-3)
    c: Coincident(g1,g-4)
    c: Diameter(g0) = 5
    c: Diameter(g1) = 5
    c: Coincident(g2,g0)
    c: Coincident(g3,g1)
    c: Diameter(g2) = 8
    c: Diameter(g3) = 8
FEATURE [PartDesign::Pad] Pad086
  BaseFeature = -> Pocket047
  Direction = (0,0,-1)
  Length = 38
  Length2 = 10
  Profile = -> Sketch065
  ReferenceAxis = -> Sketch065 [N_Axis]
  Refine = true
  Type = 0
FEATURE [Sketcher::SketchObject] Sketch066
  ExternalGeometry = -> [Pad086]
  FullyConstrained = true
  MapMode = 5
  Placement = pos=(91.9,0,0) rot=(0.57735,-0.57735,-0.57735;2.0944rad)
  Support = -> [Pad086]
  sketch-geometry (4):
    g0: LineSegment StartX=-62.1 StartY=-11.8 StartZ=0 EndX=-53.3 EndY=-11.8 EndZ=0
    g1: LineSegment StartX=-53.3 StartY=-11.8 StartZ=0 EndX=-53.3 EndY=-3 EndZ=0
    g2: LineSegment StartX=-53.3 StartY=-3 StartZ=0 EndX=-62.1 EndY=-3 EndZ=0
    g3: LineSegment StartX=-62.1 StartY=-3 StartZ=0 EndX=-62.1 EndY=-11.8 EndZ=0
  constraints (12):
    c: Coincident(g0,g1)
    c: Coincident(g1,g2)
    c: Coincident(g2,g3)
    c: Coincident(g3,g0)
    c: Horizontal(g0)
    c: Horizontal(g2)
    c: Vertical(g1)
    c: Vertical(g3)
    c: DistanceY(g3,g3) = 8.8
    c: DistanceX(g2,g2) = 8.8
    c: DistanceY(g1,g-4) = 5
    c: DistanceX(g-4,g2) = 4
FEATURE [PartDesign::Pocket] Pocket048
  BaseFeature = -> Pad086
  Direction = (1,0,0)
  Length = 1
  Length2 = 5
  Profile = -> Sketch066
  ReferenceAxis = -> Sketch066 [N_Axis]
  Refine = true
  Type = 0
FEATURE [Sketcher::SketchObject] Sketch067
  ExternalGeometry = -> [Pocket048]
  FullyConstrained = true
  MapMode = 5
  Placement = pos=(92.9,0,0) rot=(0.57735,-0.57735,-0.57735;2.0944rad)
  Support = -> [Pocket048]
  sketch-geometry (1):
    g0: Circle CenterX=-57.7 CenterY=-7.4 CenterZ=0 NormalX=0 NormalY=0 NormalZ=1 AngleXU=0 Radius=3.5
  constraints (5):
    c: Diameter(g0) = 7
    c: DistanceX(g0,g-5) = 4.4
    c: DistanceX(g-4,g0) = 4.4
    c: DistanceY(g0,g-5) = 4.4
    c: DistanceY(g-5,g0) = 4.4
FEATURE [PartDesign::Pocket] Pocket049
  BaseFeature = -> Pocket048
  Direction = (1,0,0)
  Length = 5
  Length2 = 5
  Profile = -> Sketch067
  ReferenceAxis = -> Sketch067 [N_Axis]
  Refine = true
  Type = 0
FEATURE [Sketcher::SketchObject] Sketch068
  ExternalGeometry = -> [Pocket049]
  FullyConstrained = true
  MapMode = 5
  Placement = pos=(91.9,0,0) rot=(0.57735,-0.57735,-0.57735;2.0944rad)
  Support = -> [Pocket049]
  sketch-geometry (8):
    g0: LineSegment StartX=-64.6 StartY=-16 StartZ=0 EndX=-50.6 EndY=-16 EndZ=0
    g1: LineSegment StartX=-50.6 StartY=-16 StartZ=0 EndX=-50.6 EndY=0 EndZ=0
    g2: LineSegment StartX=-50.6 StartY=0 StartZ=0 EndX=-64.6 EndY=0 EndZ=0
    g3: LineSegment StartX=-64.6 StartY=0 StartZ=0 EndX=-64.6 EndY=-16 EndZ=0
    g4: LineSegment StartX=-62.1 StartY=-11.8 StartZ=0 EndX=-53.3 EndY=-11.8 EndZ=0
    g5: LineSegment StartX=-53.3 StartY=-11.8 StartZ=0 EndX=-53.3 EndY=-3 EndZ=0
    g6: LineSegment StartX=-53.3 StartY=-3 StartZ=0 EndX=-62.1 EndY=-3 EndZ=0
    g7: LineSegment StartX=-62.1 StartY=-3 StartZ=0 EndX=-62.1 EndY=-11.8 EndZ=0
  constraints (21):
    c: Coincident(g0,g1)
    c: Coincident(g1,g2)
    c: Coincident(g2,g3)
    c: Coincident(g3,g0)
    c: Horizontal(g0)
    c: Horizontal(g2)
    c: Vertical(g1)
    c: Vertical(g3)
    c: Coincident(g2,g-4)
    c: DistanceX(g2,g2) = 14
    c: DistanceY(g1,g1) = 16
    c: Coincident(g4,g5)
    c: Coincident(g5,g6)
    c: Coincident(g6,g7)
    c: Coincident(g7,g4)
    c: Horizontal(g4)
    c: Horizontal(g6)
    c: Vertical(g5)
    c: Vertical(g7)
    c: Coincident(g4,g-8)
    c: Coincident(g5,g-7)
FEATURE [PartDesign::Pad] Pad087
  BaseFeature = -> Pocket049
  Direction = (-1,0,0)
  Length = 2
  Length2 = 10
  Profile = -> Sketch068
  ReferenceAxis = -> Sketch068 [N_Axis]
  Refine = true
  Type = 0
FEATURE [PartDesign::Pad] Pad088
  BaseFeature = -> Pad087
  Direction = (-1,0,0)
  Length = 1
  Length2 = 10
  Profile = -> Pad087 [Face48]
  Refine = true
  Type = 0
FEATURE [Sketcher::SketchObject] Sketch069
  ExternalGeometry = -> [Pad088]
  FullyConstrained = true
  MapMode = 5
  Placement = pos=(0,1e-16,2) rot=(0,0,1;0rad)
  Support = -> [Pad088]
  sketch-geometry (4):
    g0: LineSegment StartX=39.5 StartY=78.15 StartZ=0 EndX=62.3 EndY=78.15 EndZ=0
    g1: LineSegment StartX=62.3 StartY=78.15 StartZ=0 EndX=62.3 EndY=65.35 EndZ=0
    g2: LineSegment StartX=62.3 StartY=65.35 StartZ=0 EndX=39.5 EndY=65.35 EndZ=0
    g3: LineSegment StartX=39.5 StartY=65.35 StartZ=0 EndX=39.5 EndY=78.15 EndZ=0
  constraints (12):
    c: Coincident(g0,g1)
    c: Coincident(g1,g2)
    c: Coincident(g2,g3)
    c: Coincident(g3,g0)
    c: Horizontal(g0)
    c: Horizontal(g2)
    c: Vertical(g1)
    c: Vertical(g3)
    c: DistanceX(g0,g0) = 22.8
    c: DistanceY(g1,g1) = 12.8
    c: DistanceY(g0,g-3) = 23
    c: DistanceX(g-4,g0) = 18.5
FEATURE [PartDesign::Pocket] Pocket050
  BaseFeature = -> Pad088
  Direction = (0,0,-1)
  Length = 5
  Length2 = 5
  Profile = -> Sketch069
  ReferenceAxis = -> Sketch069 [N_Axis]
  Refine = true
  Type = 0
FEATURE [Sketcher::SketchObject] Sketch070
  ExternalGeometry = -> [Pocket050]
  FullyConstrained = true
  MapMode = 5
  Placement = pos=(0,0,0) rot=(1,0,0;3.14159rad)
  Support = -> [Pocket050]
  sketch-geometry (8):
    g0: LineSegment StartX=37 StartY=-55.85 StartZ=0 EndX=64.8 EndY=-55.85 EndZ=0
    g1: LineSegment StartX=64.8 StartY=-55.85 StartZ=0 EndX=64.8 EndY=-84.65 EndZ=0
    g2: LineSegment StartX=64.8 StartY=-84.65 StartZ=0 EndX=37 EndY=-84.65 EndZ=0
    g3: LineSegment StartX=37 StartY=-84.65 StartZ=0 EndX=37 EndY=-55.85 EndZ=0
    g4: LineSegment StartX=35 StartY=-53.85 StartZ=0 EndX=66.8 EndY=-53.85 EndZ=0
    g5: LineSegment StartX=66.8 StartY=-53.85 StartZ=0 EndX=66.8 EndY=-86.65 EndZ=0
    g6: LineSegment StartX=66.8 StartY=-86.65 StartZ=0 EndX=35 EndY=-86.65 EndZ=0
    g7: LineSegment StartX=35 StartY=-86.65 StartZ=0 EndX=35 EndY=-53.85 EndZ=0
  constraints (24):
    c: Coincident(g0,g1)
    c: Coincident(g1,g2)
    c: Coincident(g2,g3)
    c: Coincident(g3,g0)
    c: Horizontal(g0)
    c: Horizontal(g2)
    c: Vertical(g1)
    c: Vertical(g3)
    c: Coincident(g4,g5)
    c: Coincident(g5,g6)
    c: Coincident(g6,g7)
    c: Coincident(g7,g4)
    c: Horizontal(g4)
    c: Horizontal(g6)
    c: Vertical(g5)
    c: Vertical(g7)
    c: DistanceY(g2,g-3) = 6.5
    c: DistanceY(g-4,g0) = 9.5
    c: DistanceY(g6,g2) = 2
    c: DistanceY(g0,g4) = 2
    c: DistanceX(g-3,g1) = 2.5
    c: DistanceX(g2,g-3) = 2.5
    c: DistanceX(g1,g5) = 2
    c: DistanceX(g4,g0) = 2
FEATURE [PartDesign::Pad] Pad089
  BaseFeature = -> Pocket050
  Direction = (0,0,-1)
  Length = 3
  Length2 = 10
  Profile = -> Sketch070
  ReferenceAxis = -> Sketch070 [N_Axis]
  Refine = true
  Type = 0
FEATURE [Part::Part2DObjectPython] ShapeString008  # Draft 2D object (typed FeaturePython)
  AttachmentOffset = pos=(22,53,0) rot=(0,0,1;0rad)
  FontFile = <userpath>/Documents/FreeCad/Fonts/Stencil_tenada/Tenada.ttf
  MakeFace = true
  MapMode = 5
  Placement = pos=(22,14.7,53) rot=(1,0,0;1.5708rad)
  Size = 2.5
  String = WiFi Smart Pump
  Support = -> [Pad089]
  Tracking = 0
FEATURE [PartDesign::Pocket] Pocket051
  BaseFeature = -> Pad089
  Direction = (0,1,-2e-16)
  Length = 0.7
  Length2 = 5
  Profile = -> ShapeString008
  ReferenceAxis = -> ShapeString008 [N_Axis]
  Refine = true
  Type = 0
FEATURE [Part::Part2DObjectPython] ShapeString009  # Draft 2D object (typed FeaturePython)
  AttachmentOffset = pos=(33,43,0) rot=(0,0,1;0rad)
  FontFile = <userpath>/Documents/FreeCad/Fonts/Stencil_tenada/Tenada.ttf
  MakeFace = true
  MapMode = 5
  Placement = pos=(33,14.7,43) rot=(1,0,0;1.5708rad)
  Size = 2.4
  String = Controller S1
  Support = -> [Pocket051]
  Tracking = 0
FEATURE [PartDesign::Pocket] Pocket052
  BaseFeature = -> Pocket051
  Direction = (0,1,-2e-16)
  Length = 0.7
  Length2 = 5
  Profile = -> ShapeString009
  ReferenceAxis = -> ShapeString009 [N_Axis]
  Refine = true
  Type = 0
FEATURE [PartDesign::Pad] Pad090
  BaseFeature = -> Pocket052
  Direction = (0,-1,0)
  Length = 1
  Length2 = 10
  Profile = -> Pocket052 [Face29]
  Refine = true
  Type = 0
FEATURE [Sketcher::SketchObject] Sketch071
  ExternalGeometry = -> [Pad090]
  FullyConstrained = false
  MapMode = 5
  Placement = pos=(0,1e-16,2) rot=(0,0,1;0rad)
  Support = -> [Pad090]
  sketch-geometry (4):
    g0: LineSegment StartX=93.9 StartY=48.3611 StartZ=0 EndX=81.2 EndY=48.3611 EndZ=0
    g1: LineSegment StartX=81.2 StartY=48.3611 StartZ=0 EndX=81.2 EndY=32.3611 EndZ=0
    g2: LineSegment StartX=81.2 StartY=32.3611 StartZ=0 EndX=93.9 EndY=32.3611 EndZ=0
    g3: LineSegment StartX=93.9 StartY=32.3611 StartZ=0 EndX=93.9 EndY=48.3611 EndZ=0
  constraints (11):
    c: Coincident(g0,g1)
    c: Coincident(g1,g2)
    c: Coincident(g2,g3)
    c: Coincident(g3,g0)
    c: Horizontal(g0)
    c: Horizontal(g2)
    c: Vertical(g1)
    c: Vertical(g3)
    c: PointOnObject(g0,g-3)
    c: DistanceY(g1,g1) = 16
    c: DistanceX(g0,g0) = 12.7
FEATURE [PartDesign::Pocket] Pocket056
  BaseFeature = -> Pad090
  Direction = (0,0,-1)
  Length = 122
  Length2 = 5
  Profile = -> Sketch071
  ReferenceAxis = -> Sketch071 [N_Axis]
  Refine = true
  Type = 0
FEATURE [PartDesign::Pocket] Pocket057
  BaseFeature = -> Pocket056
  Direction = (0,0,1)
  Length = 1
  Length2 = 5
  Profile = -> Pocket056 [Face46]
  Refine = true
  Type = 0
FEATURE [PartDesign::Pocket] Pocket058
  BaseFeature = -> Pocket057
  Direction = (0,0,-1)
  Length = 1
  Length2 = 5
  Profile = -> Pocket057 [Face45]
  Refine = true
  Type = 0
FEATURE [PartDesign::Pad] Pad092
  BaseFeature = -> Pocket058
  Direction = (1,0,0)
  Length = 2
  Length2 = 10
  Profile = -> Pocket058 [Face13]
  Refine = true
  Type = 0
FEATURE [PartDesign::Pad] Pad093
  BaseFeature = -> Pad092
  Direction = (0,-1,0)
  Length = 2.5
  Length2 = 10
  Profile = -> Pad092 [Face1]
  Refine = true
  Type = 0
FEATURE [PartDesign::Pad] Pad094
  BaseFeature = -> Pad093
  Direction = (0,1,0)
  Length = 3.5
  Length2 = 10
  Profile = -> Pad093 [Face19]
  Refine = true
  Type = 0
FEATURE [Sketcher::SketchObject] Sketch072
  ExternalGeometry = -> [Pad094]
  FullyConstrained = true
  MapMode = 5
  Placement = pos=(0,0,0) rot=(1,0,0;3.14159rad)
  Support = -> [Pad094]
  sketch-geometry (4):
    g0: LineSegment StartX=83.2 StartY=-33.8611 StartZ=0 EndX=81.7 EndY=-33.8611 EndZ=0
    g1: LineSegment StartX=81.7 StartY=-33.8611 StartZ=0 EndX=81.7 EndY=-47.8611 EndZ=0
    g2: LineSegment StartX=81.7 StartY=-47.8611 StartZ=0 EndX=83.2 EndY=-47.8611 EndZ=0
    g3: LineSegment StartX=83.2 StartY=-47.8611 StartZ=0 EndX=83.2 EndY=-33.8611 EndZ=0
  constraints (12):
    c: Coincident(g0,g1)
    c: Coincident(g1,g2)
    c: Coincident(g2,g3)
    c: Coincident(g3,g0)
    c: Horizontal(g0)
    c: Horizontal(g2)
    c: Vertical(g1)
    c: Vertical(g3)
    c: PointOnObject(g0,g-3)
    c: DistanceY(g-3,g0) = 2
    c: DistanceY(g2,g-3) = 2
    c: DistanceX(g0,g0) = 1.5
FEATURE [PartDesign::Pad] Pad095
  BaseFeature = -> Pad094
  Direction = (0,0,-1)
  Length = 38.4
  Length2 = 10
  Profile = -> Sketch072
  ReferenceAxis = -> Sketch072 [N_Axis]
  Refine = true
  Type = 0
FEATURE [Sketcher::SketchObject] Sketch073
  ExternalGeometry = -> [Pad095]
  FullyConstrained = true
  MapMode = 5
  Placement = pos=(83.2,0,3.24e-14) rot=(0.57735,0.57735,0.57735;2.0944rad)
  Support = -> [Pad095]
  sketch-geometry (8):
    g0: LineSegment StartX=47.8611 StartY=-3.55e-14 StartZ=0 EndX=45.8611 EndY=-3.55e-14 EndZ=0
    g1: LineSegment StartX=45.8611 StartY=-3.55e-14 StartZ=0 EndX=45.8611 EndY=-38.4 EndZ=0
    g2: LineSegment StartX=45.8611 StartY=-38.4 StartZ=0 EndX=47.8611 EndY=-38.4 EndZ=0
    g3: LineSegment StartX=47.8611 StartY=-38.4 StartZ=0 EndX=47.8611 EndY=-3.55e-14 EndZ=0
    g4: LineSegment StartX=33.8611 StartY=0 StartZ=0 EndX=35.8611 EndY=0 EndZ=0
    g5: LineSegment StartX=35.8611 StartY=0 StartZ=0 EndX=35.8611 EndY=-38.4 EndZ=0
    g6: LineSegment StartX=35.8611 StartY=-38.4 StartZ=0 EndX=33.8611 EndY=-38.4 EndZ=0
    g7: LineSegment StartX=33.8611 StartY=-38.4 StartZ=0 EndX=33.8611 EndY=0 EndZ=0
  constraints (23):
    c: Coincident(g0,g1)
    c: Coincident(g1,g2)
    c: Coincident(g2,g3)
    c: Coincident(g3,g0)
    c: Horizontal(g0)
    c: Horizontal(g2)
    c: Vertical(g1)
    c: Vertical(g3)
    c: Coincident(g0,g-4)
    c: PointOnObject(g1,g-5)
    c: DistanceX(g2,g2) = 2
    c: Coincident(g4,g5)
    c: Coincident(g5,g6)
    c: Coincident(g6,g7)
    c: Coincident(g7,g4)
    c: Horizontal(g4)
    c: Horizontal(g6)
    c: Vertical(g5)
    c: Vertical(g7)
    c: PointOnObject(g4,g-3)
    c: DistanceX(g4,g4) = 2
    c: PointOnObject(g5,g-5)
    c: PointOnObject(g4,g-1)
FEATURE [PartDesign::Pad] Pad096
  BaseFeature = -> Pad095
  Direction = (1,0,4e-16)
  Length = 9
  Length2 = 10
  Profile = -> Sketch073
  ReferenceAxis = -> Sketch073 [N_Axis]
  Refine = true
  Type = 0
FEATURE [Sketcher::SketchObject] Sketch074
  ExternalGeometry = -> [Pad096]
  FullyConstrained = true
  MapMode = 5
  Placement = pos=(83.2,0,3.24e-14) rot=(0.57735,0.57735,0.57735;2.0944rad)
  Support = -> [Pad096]
  sketch-geometry (4):
    g0: LineSegment StartX=35.8611 StartY=-33.4 StartZ=0 EndX=45.8611 EndY=-33.4 EndZ=0
    g1: LineSegment StartX=45.8611 StartY=-33.4 StartZ=0 EndX=45.8611 EndY=-36.4 EndZ=0
    g2: LineSegment StartX=45.8611 StartY=-36.4 StartZ=0 EndX=35.8611 EndY=-36.4 EndZ=0
    g3: LineSegment StartX=35.8611 StartY=-36.4 StartZ=0 EndX=35.8611 EndY=-33.4 EndZ=0
  constraints (12):
    c: Coincident(g0,g1)
    c: Coincident(g1,g2)
    c: Coincident(g2,g3)
    c: Coincident(g3,g0)
    c: Horizontal(g0)
    c: Horizontal(g2)
    c: Vertical(g1)
    c: Vertical(g3)
    c: DistanceY(g-3,g2) = 2
    c: DistanceY(g3,g3) = 3
    c: PointOnObject(g0,g-5)
    c: PointOnObject(g0,g-4)
FEATURE [PartDesign::Pad] Pad097
  BaseFeature = -> Pad096
  Direction = (1,0,4e-16)
  Length = 10.7
  Length2 = 10
  Profile = -> Sketch074
  ReferenceAxis = -> Sketch074 [N_Axis]
  Refine = true
  Type = 0
FEATURE [Sketcher::SketchObject] Sketch075
  ExternalGeometry = -> [Pad097]
  FullyConstrained = true
  MapMode = 5
  Placement = pos=(0,45.8611,0) rot=(1,0,0;1.5708rad)
  Support = -> [Pad097]
  sketch-geometry (4):
    g0: LineSegment StartX=91.9 StartY=-51.1 StartZ=0 EndX=93.9 EndY=-51.1 EndZ=0
    g1: LineSegment StartX=93.9 StartY=-51.1 StartZ=0 EndX=93.9 EndY=-36.4 EndZ=0
    g2: LineSegment StartX=93.9 StartY=-36.4 StartZ=0 EndX=91.9 EndY=-36.4 EndZ=0
    g3: LineSegment StartX=91.9 StartY=-36.4 StartZ=0 EndX=91.9 EndY=-51.1 EndZ=0
  constraints (11):
    c: Coincident(g0,g1)
    c: Coincident(g1,g2)
    c: Coincident(g2,g3)
    c: Coincident(g3,g0)
    c: Horizontal(g0)
    c: Horizontal(g2)
    c: Vertical(g1)
    c: Vertical(g3)
    c: Coincident(g0,g-3)
    c: PointOnObject(g0,g-5)
    c: PointOnObject(g1,g-4)
FEATURE [PartDesign::Pad] Pad098
  BaseFeature = -> Pad097
  Direction = (0,-1,2e-16)
  Length = 10
  Length2 = 10
  Profile = -> Sketch075
  ReferenceAxis = -> Sketch075 [N_Axis]
  Refine = true
  Type = 0
FEATURE [PartDesign::Fillet] Fillet006
  Base = -> Pad098 [Edge32,Edge28]
  BaseFeature = -> Pad098
  Radius = 2
  Refine = true
  SupportTransform = false
  UseAllEdges = false
FEATURE [PartDesign::Fillet] Fillet007
  Base = -> Fillet006 [Edge166,Edge164]
  BaseFeature = -> Fillet006
  Radius = 3
  Refine = true
  SupportTransform = false
  UseAllEdges = false
FEATURE [Sketcher::SketchObject] Sketch076
  ExternalGeometry = -> [Fillet007]
  FullyConstrained = true
  MapMode = 5
  Placement = pos=(1.6e-14,0,-36.4) rot=(1,0,0;3.14159rad)
  Support = -> [Fillet007]
  sketch-geometry (8):
    g0: LineSegment StartX=83.51 StartY=-36.0511 StartZ=0 EndX=86.81 EndY=-36.0511 EndZ=0
    g1: LineSegment StartX=86.81 StartY=-36.0511 StartZ=0 EndX=86.81 EndY=-38.0511 EndZ=0
    g2: LineSegment StartX=86.81 StartY=-38.0511 StartZ=0 EndX=83.51 EndY=-38.0511 EndZ=0
    g3: LineSegment StartX=83.51 StartY=-38.0511 StartZ=0 EndX=83.51 EndY=-36.0511 EndZ=0
    g4: LineSegment StartX=83.51 StartY=-45.4811 StartZ=0 EndX=86.81 EndY=-45.4811 EndZ=0
    g5: LineSegment StartX=86.81 StartY=-45.4811 StartZ=0 EndX=86.81 EndY=-43.4811 EndZ=0
    g6: LineSegment StartX=86.81 StartY=-43.4811 StartZ=0 EndX=83.51 EndY=-43.4811 EndZ=0
    g7: LineSegment StartX=83.51 StartY=-43.4811 StartZ=0 EndX=83.51 EndY=-45.4811 EndZ=0
  constraints (24):
    c: Coincident(g0,g1)
    c: Coincident(g1,g2)
    c: Coincident(g2,g3)
    c: Coincident(g3,g0)
    c: Horizontal(g0)
    c: Horizontal(g2)
    c: Vertical(g1)
    c: Vertical(g3)
    c: Coincident(g4,g5)
    c: Coincident(g5,g6)
    c: Coincident(g6,g7)
    c: Coincident(g7,g4)
    c: Horizontal(g4)
    c: Horizontal(g6)
    c: Vertical(g5)
    c: Vertical(g7)
    c: DistanceX(g0,g0) = 3.3
    c: DistanceY(g1,g1) = 2
    c: DistanceY(g5,g5) = 2
    c: DistanceX(g6,g6) = 3.3
    c: DistanceX(g-3,g2) = 0.31
    c: DistanceX(g-3,g4) = 0.31
    c: DistanceY(g2,g-3) = 2.19
    c: DistanceY(g-3,g6) = 2.38
FEATURE [PartDesign::Pocket] Pocket059
  BaseFeature = -> Fillet007
  Direction = (-4e-16,0,1)
  Length = 2.4
  Length2 = 5
  Profile = -> Sketch076
  ReferenceAxis = -> Sketch076 [N_Axis]
  Refine = true
  Type = 0
FEATURE [Sketcher::SketchObject] Sketch077
  ExternalGeometry = -> [Pocket059]
  FullyConstrained = true
  MapMode = 5
  Placement = pos=(1.6e-14,0,-36.4) rot=(1,0,0;3.14159rad)
  Support = -> [Pocket059]
  sketch-geometry (4):
    g0: LineSegment StartX=83.2 StartY=-39.8611 StartZ=0 EndX=91.9 EndY=-39.8611 EndZ=0
    g1: LineSegment StartX=91.9 StartY=-39.8611 StartZ=0 EndX=91.9 EndY=-41.8611 EndZ=0
    g2: LineSegment StartX=91.9 StartY=-41.8611 StartZ=0 EndX=83.2 EndY=-41.8611 EndZ=0
    g3: LineSegment StartX=83.2 StartY=-41.8611 StartZ=0 EndX=83.2 EndY=-39.8611 EndZ=0
  constraints (13):
    c: Coincident(g0,g1)
    c: Coincident(g1,g2)
    c: Coincident(g2,g3)
    c: Coincident(g3,g0)
    c: Horizontal(g0)
    c: Horizontal(g2)
    c: Vertical(g1)
    c: Vertical(g3)
    c: PointOnObject(g0,g-3)
    c: PointOnObject(g1,g-4)
    c: DistanceY(g3,g3) = 2
    c: DistanceY(g0,g-3) = 4
    c: DistanceY(g-3,g2) = 4
FEATURE [PartDesign::Pad] Pad099
  BaseFeature = -> Pocket059
  Direction = (4e-16,0,-1)
  Length = 2
  Length2 = 10
  Profile = -> Sketch077
  ReferenceAxis = -> Sketch077 [N_Axis]
  Refine = true
  Type = 0
FEATURE [PartDesign::Pad] Pad100
  BaseFeature = -> Pad099
  Direction = (0,-1,0)
  Length = 0.3
  Length2 = 10
  Profile = -> Pad099 [Face26]
  Refine = true
  Type = 0
FEATURE [PartDesign::Pad] Pad101
  BaseFeature = -> Pad100
  Direction = (0,0,-1)
  Length = 0.1
  Length2 = 10
  Profile = -> Pad100 [Face25]
  Refine = true
  Type = 0
FEATURE [Sketcher::SketchObject] Sketch078
  ExternalGeometry = -> [Pad101]
  FullyConstrained = true
  MapMode = 5
  Placement = pos=(-2e-16,16.7,-1e-15) rot=(0,0.707107,0.707107;3.14159rad)
  Support = -> [Pad101]
  sketch-geometry (4):
    g0: LineSegment StartX=-93.9 StartY=-28.8 StartZ=0 EndX=-92.2 EndY=-28.8 EndZ=0
    g1: LineSegment StartX=-92.2 StartY=-28.8 StartZ=0 EndX=-92.2 EndY=-39.8 EndZ=0
    g2: LineSegment StartX=-92.2 StartY=-39.8 StartZ=0 EndX=-93.9 EndY=-39.8 EndZ=0
    g3: LineSegment StartX=-93.9 StartY=-39.8 StartZ=0 EndX=-93.9 EndY=-28.8 EndZ=0
  constraints (11):
    c: Coincident(g0,g1)
    c: Coincident(g1,g2)
    c: Coincident(g2,g3)
    c: Coincident(g3,g0)
    c: Horizontal(g0)
    c: Horizontal(g2)
    c: Vertical(g1)
    c: Vertical(g3)
    c: Coincident(g0,g-3)
    c: DistanceY(g3,g3) = 11
    c: DistanceX(g0,g0) = 1.7
FEATURE [PartDesign::Pad] Pad102
  BaseFeature = -> Pad101
  Direction = (0,1,-2e-16)
  Length = 2
  Length2 = 10
  Profile = -> Sketch078
  ReferenceAxis = -> Sketch078 [N_Axis]
  Refine = true
  Type = 0
FEATURE [Part::Part2DObjectPython] ShapeString010  # Draft 2D object (typed FeaturePython)
  AttachmentOffset = pos=(-25,-17,0) rot=(0,0,1;3.14159rad)
  FontFile = <userpath>/Documents/FreeCad/Fonts/Stencil_tenada/Tenada.ttf
  MakeFace = true
  MapMode = 5
  Placement = pos=(25,101.15,-17) rot=(1,0,0;4.71239rad)
  Size = 3
  String = WaterLevel
  Support = -> [Pad102]
  Tracking = 0
FEATURE [PartDesign::Pad] Pad103
  BaseFeature = -> Pad102
  Direction = (0,1,-2e-16)
  Length = 1
  Length2 = 10
  Profile = -> ShapeString010
  ReferenceAxis = -> ShapeString010 [N_Axis]
  Refine = true
  Type = 0
FEATURE [Part::Part2DObjectPython] ShapeString011  # Draft 2D object (typed FeaturePython)
  AttachmentOffset = pos=(-43,-7,0) rot=(0,0,1;3.14159rad)
  FontFile = <userpath>/Documents/FreeCad/Fonts/Stencil_tenada/Tenada.ttf
  MakeFace = true
  MapMode = 5
  Placement = pos=(43,101.15,-7) rot=(1,0,0;4.71239rad)
  Size = 3
  String = .Pro
  Support = -> [Pad103]
  Tracking = 0
FEATURE [PartDesign::Pad] Pad104
  BaseFeature = -> Pad103
  Direction = (0,1,-2e-16)
  Length = 1
  Length2 = 10
  Profile = -> ShapeString011
  ReferenceAxis = -> ShapeString011 [N_Axis]
  Refine = true
  Type = 0
FEATURE [PartDesign::Pocket] Pocket060
  BaseFeature = -> Pad104
  Direction = (0,0,-1)
  Length = 0.7
  Length2 = 5
  Profile = -> ShapeString012
  ReferenceAxis = -> ShapeString012 [N_Axis]
  Refine = true
  Type = 0
FEATURE [PartDesign::Pocket] Pocket061
  BaseFeature = -> Pocket060
  Direction = (0,0,-1)
  Length = 0.7
  Length2 = 5
  Profile = -> ShapeString013
  ReferenceAxis = -> ShapeString013 [N_Axis]
  Refine = true
  Type = 0
FEATURE [PartDesign::Boolean] Boolean001
  BaseFeature = -> Pocket061
  Group = -> [Body004]
  Refine = true
  Type = 0
FEATURE [PartDesign::Pocket] Pocket062
  BaseFeature = -> Boolean001
  Direction = (0,-1,0)
  Length = 1.85
  Length2 = 5
  Profile = -> Boolean001 [Face74]
  Refine = true
  Type = 0
FEATURE [PartDesign::Pad] Pad105
  BaseFeature = -> Pocket062
  Direction = (0,0,-1)
  Length = 0.01
  Length2 = 10
  Profile = -> Pocket062 [Face40]
  Refine = true
  Type = 0
FEATURE [PartDesign::Pocket] Pocket063
  BaseFeature = -> Pad105
  Direction = (1,0,4e-16)
  Length = 4
  Length2 = 5
  Profile = -> Pad105 [Face65,Face62]
  Refine = true
  Type = 0
FEATURE [Sketcher::SketchObject] Sketch079
  ExternalGeometry = -> [Pocket063]
  FullyConstrained = true
  MapMode = 5
  Placement = pos=(0,0,0) rot=(1,0,0;3.14159rad)
  Support = -> [Pocket063]
  sketch-geometry (8):
    g0: LineSegment StartX=39.5 StartY=-65.35 StartZ=0 EndX=62.3 EndY=-65.35 EndZ=0
    g1: LineSegment StartX=62.3 StartY=-65.35 StartZ=0 EndX=62.3 EndY=-78.15 EndZ=0
    g2: LineSegment StartX=62.3 StartY=-78.15 StartZ=0 EndX=39.5 EndY=-78.15 EndZ=0
    g3: LineSegment StartX=39.5 StartY=-78.15 StartZ=0 EndX=39.5 EndY=-65.35 EndZ=0
    g4: LineSegment StartX=38.5 StartY=-64.35 StartZ=0 EndX=63.3 EndY=-64.35 EndZ=0
    g5: LineSegment StartX=63.3 StartY=-64.35 StartZ=0 EndX=63.3 EndY=-79.15 EndZ=0
    g6: LineSegment StartX=63.3 StartY=-79.15 StartZ=0 EndX=38.5 EndY=-79.15 EndZ=0
    g7: LineSegment StartX=38.5 StartY=-79.15 StartZ=0 EndX=38.5 EndY=-64.35 EndZ=0
  constraints (22):
    c: Coincident(g0,g1)
    c: Coincident(g1,g2)
    c: Coincident(g2,g3)
    c: Coincident(g3,g0)
    c: Horizontal(g0)
    c: Horizontal(g2)
    c: Vertical(g1)
    c: Vertical(g3)
    c: Coincident(g0,g-4)
    c: Coincident(g1,g-6)
    c: Coincident(g4,g5)
    c: Coincident(g5,g6)
    c: Coincident(g6,g7)
    c: Coincident(g7,g4)
    c: Horizontal(g4)
    c: Horizontal(g6)
    c: Vertical(g5)
    c: Vertical(g7)
    c: DistanceX(g0,g4) = 1
    c: DistanceX(g6,g2) = 1
    c: DistanceY(g0,g4) = 1
    c: DistanceY(g5,g1) = 1
FEATURE [PartDesign::Pad] Pad106
  BaseFeature = -> Pocket063
  Direction = (0,0,-1)
  Length = 1
  Length2 = 10
  Profile = -> Sketch079
  ReferenceAxis = -> Sketch079 [N_Axis]
  Refine = true
  Type = 0
FEATURE [PartDesign::Pad] Pad107
  BaseFeature = -> Pad106
  Direction = (0,0,-1)
  Length = 11.8
  Length2 = 10
  Profile = -> Pad106 [Face37]
  Refine = true
  Type = 0
FEATURE [PartDesign::Pad] Pad108
  BaseFeature = -> Pad107
  Direction = (0,-1,0)
  Length = 1
  Length2 = 10
  Profile = -> Pad107 [Face80]
  Refine = true
  Type = 0
FEATURE [Sketcher::SketchObject] Sketch080
  ExternalGeometry = -> [Pad108]
  FullyConstrained = true
  MapMode = 5
  Placement = pos=(93.9,9e-16,-5.6e-15) rot=(0.57735,0.57735,0.57735;2.0944rad)
  Support = -> [Pad108]
  sketch-geometry (1):
    g0: Circle CenterX=24.13 CenterY=-34.99 CenterZ=0 NormalX=0 NormalY=0 NormalZ=1 AngleXU=0 Radius=2.2
  constraints (3):
    c: Diameter(g0) = 4.4
    c: DistanceY(g-3,g0) = 5.61
    c: DistanceX(g0,g-3) = 5.97
FEATURE [PartDesign::Pocket] Pocket064
  BaseFeature = -> Pad108
  Direction = (-1,0,0)
  Length = 5
  Length2 = 5
  Profile = -> Sketch080
  ReferenceAxis = -> Sketch080 [N_Axis]
  Refine = true
  Type = 0
FEATURE [PartDesign::Pad] Pad109
  BaseFeature = -> Pocket064
  Direction = (0,0,1)
  Length = 1.7
  Length2 = 10
  Profile = -> Pocket064 [Face1089,Face1090,Face1091,Face1092,Face1093,Face1094,Face1095,Face1096,Face1105,Face1106,Face1107,Face1108,Face1110,Face1111,Face1109,Face1104,Face1103,Face1102,Face1099,Face1101,Face1100,Face1097,Face1098,Face1088,Face1087,Face1086,Face1085]
  Refine = true
  Type = 0
FEATURE [PartDesign::Pocket] Pocket065
  BaseFeature = -> Pad109
  Direction = (0,0,1)
  Length = 1
  Length2 = 5
  Profile = -> Pad109 [Face1129]
  Refine = true
  Type = 0
FEATURE [PartDesign::Pocket] Pocket066
  BaseFeature = -> Pocket065
  Direction = (0,0,1)
  Length = 1
  Length2 = 5
  Profile = -> Pocket065 [Face1110]
  Refine = true
  Type = 0
FEATURE [Sketcher::SketchObject] Sketch081
  ExternalGeometry = -> [Pocket066]
  FullyConstrained = true
  MapMode = 5
  Placement = pos=(0,0,-3) rot=(1,0,0;3.14159rad)
  Support = -> [Pocket066]
  sketch-geometry (4):
    g0: LineSegment StartX=35 StartY=-55.85 StartZ=0 EndX=66.8 EndY=-55.85 EndZ=0
    g1: LineSegment StartX=66.8 StartY=-55.85 StartZ=0 EndX=66.8 EndY=-84.65 EndZ=0
    g2: LineSegment StartX=66.8 StartY=-84.65 StartZ=0 EndX=35 EndY=-84.65 EndZ=0
    g3: LineSegment StartX=35 StartY=-84.65 StartZ=0 EndX=35 EndY=-55.85 EndZ=0
  constraints (12):
    c: Coincident(g0,g1)
    c: Coincident(g1,g2)
    c: Coincident(g2,g3)
    c: Coincident(g3,g0)
    c: Horizontal(g0)
    c: Horizontal(g2)
    c: Vertical(g1)
    c: Vertical(g3)
    c: PointOnObject(g0,g-4)
    c: PointOnObject(g1,g-5)
    c: PointOnObject(g-6,g0)
    c: PointOnObject(g-3,g2)
FEATURE [PartDesign::Pocket] Pocket067
  BaseFeature = -> Pocket066
  Direction = (0,0,1)
  Length = 2.99
  Length2 = 5
  Profile = -> Sketch081
  ReferenceAxis = -> Sketch081 [N_Axis]
  Refine = true
  Type = 0
FEATURE [Sketcher::SketchObject] Sketch082
  FullyConstrained = false
  MapMode = 5
  Placement = pos=(0,0,0) rot=(1,0,0;3.14159rad)
  Support = -> [Pocket067]
  sketch-geometry (4):
    g0: LineSegment StartX=-3.9777 StartY=-9.53597 StartZ=0 EndX=100.941 EndY=-9.53597 EndZ=0
    g1: LineSegment StartX=100.941 StartY=-9.53597 StartZ=0 EndX=100.941 EndY=-106.791 EndZ=0
    g2: LineSegment StartX=100.941 StartY=-106.791 StartZ=0 EndX=-3.9777 EndY=-106.791 EndZ=0
    g3: LineSegment StartX=-3.9777 StartY=-106.791 StartZ=0 EndX=-3.9777 EndY=-9.53597 EndZ=0
  constraints (8):
    c: Coincident(g0,g1)
    c: Coincident(g1,g2)
    c: Coincident(g2,g3)
    c: Coincident(g3,g0)
    c: Horizontal(g0)
    c: Horizontal(g2)
    c: Vertical(g1)
    c: Vertical(g3)
FEATURE [PartDesign::Pocket] Pocket068
  BaseFeature = -> Pocket067
  Direction = (0,0,1)
  Length = 500
  Length2 = 5
  Profile = -> Sketch082
  ReferenceAxis = -> Sketch082 [N_Axis]
  Refine = true
  Reversed = true
  Type = 0
FEATURE [PartDesign::Draft] Draft001
  Angle = 45
  Base = -> Pocket068 [Face13,Face19,Face11,Face16]
  BaseFeature = -> Pocket068
  NeutralPlane = -> Pocket068 [Face27]
  PullDirection = -> Pocket068 [Edge40]
  Refine = true
  Reversed = true
  SupportTransform = false
FEATURE [PartDesign::Draft] Draft
  Angle = 45
  Base = -> Draft001 [Face26,Face24,Face12,Face18]
  BaseFeature = -> Draft001
  NeutralPlane = -> Draft001 [Face27]
  Refine = true
  Reversed = true
  SupportTransform = false
FEATURE [PartDesign::Draft] Draft002
  Angle = 45
  Base = -> Draft [Face20,Face22,Face14]
  BaseFeature = -> Draft
  NeutralPlane = -> Draft [Face27]
  Refine = true
  Reversed = true
  SupportTransform = false
FEATURE [PartDesign::Draft] Draft003
  Angle = 45
  Base = -> Draft002 [Face25,Face23,Face21]
  BaseFeature = -> Draft002
  NeutralPlane = -> Draft002 [Face27]
  Refine = true
  Reversed = true
  SupportTransform = false
FEATURE [PartDesign::Body] Body003  label="LidA"
  Group = -> [Sketch049,Pad066,Sketch053,Pad069,Pad070,Pad071,Sketch054,Pad074,Sketch055,Pad075,Pocket039,Pad076,Pad077,Sketch056,Pad078,Sketch057,Pad079,Sketch058,Pad080,Pocket040,Sketch059,Pad081,Sketch060,Pad082,Sketch061,Pad083,Pad084,Pocket041,Pocket042,Pad085,Sketch062,Pocket043,Sketch063,Pocket044,Pocket045,Pocket046,Sketch064,Pocket047,Sketch065,Pad086,Sketch066,Pocket048,Sketch067,Pocket049,Sketch068,+65 more]
  Origin = -> Origin120
  Placement = pos=(0,0,0.06) rot=(0,0,1;0rad)
  Tip = -> Draft003
FEATURE [Sketcher::SketchObject] Sketch083
  FullyConstrained = false
  MapMode = 5
  Placement = pos=(0,0,-3) rot=(1,0,0;3.14159rad)
  Support = -> [Pocket036]
  sketch-geometry (4):
    g0: LineSegment StartX=33.6898 StartY=-52.6757 StartZ=0 EndX=68.5368 EndY=-52.6757 EndZ=0
    g1: LineSegment StartX=68.5368 StartY=-52.6757 StartZ=0 EndX=68.5368 EndY=-87.7673 EndZ=0
    g2: LineSegment StartX=68.5368 StartY=-87.7673 StartZ=0 EndX=33.6898 EndY=-87.7673 EndZ=0
    g3: LineSegment StartX=33.6898 StartY=-87.7673 StartZ=0 EndX=33.6898 EndY=-52.6757 EndZ=0
  constraints (8):
    c: Coincident(g0,g1)
    c: Coincident(g1,g2)
    c: Coincident(g2,g3)
    c: Coincident(g3,g0)
    c: Horizontal(g0)
    c: Horizontal(g2)
    c: Vertical(g1)
    c: Vertical(g3)
FEATURE [PartDesign::Pocket] Pocket069
  BaseFeature = -> Pocket036
  Direction = (0,0,1)
  Length = 55
  Length2 = 5
  Profile = -> Sketch083
  ReferenceAxis = -> Sketch083 [N_Axis]
  Refine = true
  Type = 0
FEATURE [PartDesign::Pocket] Pocket070
  BaseFeature = -> Pocket069
  Direction = (0,0,1)
  Length = 5
  Length2 = 5
  Profile = -> Pocket069 [Face1]
  Refine = true
  Type = 0
FEATURE [PartDesign::Chamfer] Chamfer
  Angle = 45
  Base = -> Pocket070 [Edge133]
  BaseFeature = -> Pocket070
  ChamferType = 0
  FlipDirection = false
  Refine = true
  Size = 1.44
  Size2 = 1
  SupportTransform = false
  UseAllEdges = false
FEATURE [PartDesign::Chamfer] Chamfer001
  Angle = 45
  Base = -> Chamfer [Edge6]
  BaseFeature = -> Chamfer
  ChamferType = 0
  FlipDirection = false
  Refine = true
  Size = 1.7
  Size2 = 1
  SupportTransform = false
  UseAllEdges = false
FEATURE [PartDesign::Chamfer] Chamfer002
  Angle = 45
  Base = -> Chamfer001 [Edge6,Edge8,Edge12,Edge10,Edge14,Edge16,Edge18]
  BaseFeature = -> Chamfer001
  ChamferType = 0
  FlipDirection = false
  Refine = true
  Size = 1.93
  Size2 = 1
  SupportTransform = false
  UseAllEdges = false
FEATURE [PartDesign::Pocket] Pocket071
  BaseFeature = -> Chamfer002
  Direction = (0,0,-1)
  Length = 1
  Length2 = 5
  Profile = -> Chamfer002 [Face67]
  Refine = true
  Type = 0
FEATURE [PartDesign::Chamfer] Chamfer003
  Angle = 45
  Base = -> Pocket071 [Edge144]
  BaseFeature = -> Pocket071
  ChamferType = 0
  FlipDirection = false
  Refine = true
  Size = 1.4
  Size2 = 1
  SupportTransform = false
  UseAllEdges = false
FEATURE [PartDesign::Pocket] Pocket072
  BaseFeature = -> Chamfer003
  Direction = (0,1,0)
  Length = 0.1
  Length2 = 5
  Profile = -> Chamfer003 [Face34]
  Refine = true
  Type = 0
FEATURE [PartDesign::Chamfer] Chamfer004
  Angle = 45
  Base = -> Pocket072 [Edge53,Edge489]
  BaseFeature = -> Pocket072
  ChamferType = 0
  FlipDirection = false
  Refine = true
  Size = 1.44
  Size2 = 1
  SupportTransform = false
  UseAllEdges = false
FEATURE [Sketcher::SketchObject] Sketch084
  ExternalGeometry = -> [Chamfer004]
  FullyConstrained = true
  MapMode = 5
  Placement = pos=(0,0,2) rot=(0,0,1;0rad)
  Support = -> [Chamfer004]
  sketch-geometry (4):
    g0: LineSegment StartX=91.9 StartY=50.6 StartZ=0 EndX=89.9 EndY=50.6 EndZ=0
    g1: LineSegment StartX=89.9 StartY=50.6 StartZ=0 EndX=89.9 EndY=64.6 EndZ=0
    g2: LineSegment StartX=89.9 StartY=64.6 StartZ=0 EndX=91.9 EndY=64.6 EndZ=0
    g3: LineSegment StartX=91.9 StartY=64.6 StartZ=0 EndX=91.9 EndY=50.6 EndZ=0
  constraints (10):
    c: Coincident(g0,g1)
    c: Coincident(g1,g2)
    c: Coincident(g2,g3)
    c: Coincident(g3,g0)
    c: Horizontal(g0)
    c: Horizontal(g2)
    c: Vertical(g1)
    c: Vertical(g3)
    c: Coincident(g0,g-3)
    c: Coincident(g1,g-4)
FEATURE [PartDesign::Pocket] Pocket073
  BaseFeature = -> Chamfer004
  Direction = (0,0,-1)
  Length = 2
  Length2 = 5
  Profile = -> Sketch084
  ReferenceAxis = -> Sketch084 [N_Axis]
  Refine = true
  Type = 0
FEATURE [PartDesign::Chamfer] Chamfer005
  Angle = 45
  Base = -> Pocket073 [Edge32]
  BaseFeature = -> Pocket073
  ChamferType = 0
  FlipDirection = false
  Refine = true
  Size = 1.94
  Size2 = 1
  SupportTransform = false
  UseAllEdges = false
FEATURE [PartDesign::Chamfer] Chamfer006
  Angle = 45
  Base = -> Chamfer005 [Edge6]
  BaseFeature = -> Chamfer005
  ChamferType = 0
  FlipDirection = false
  Refine = true
  Size = 1.43
  Size2 = 1
  SupportTransform = false
  UseAllEdges = false
FEATURE [Sketcher::SketchObject] Sketch088
  FullyConstrained = false
  MapMode = 5
  Support = -> [XY_Plane050]
  sketch-geometry (12):
    g0: LineSegment StartX=85.2 StartY=45.8611 StartZ=0 EndX=93.9 EndY=45.8611 EndZ=0
    g1: LineSegment StartX=93.9 StartY=35.8611 StartZ=0 EndX=85.2 EndY=35.8611 EndZ=0
    g2: LineSegment StartX=83.2 StartY=37.8611 StartZ=0 EndX=83.2 EndY=43.8611 EndZ=0
    g3: ArcOfCircle CenterX=85.2 CenterY=43.8611 CenterZ=0 NormalX=0 NormalY=0 NormalZ=1 AngleXU=0 Radius=2 StartAngle=1.5708 EndAngle=3.14159
    g4: ArcOfCircle CenterX=85.2 CenterY=37.8611 CenterZ=0 NormalX=0 NormalY=0 NormalZ=1 AngleXU=0 Radius=2 StartAngle=3.14159 EndAngle=4.71239
    g5: LineSegment StartX=93.9 StartY=47.8611 StartZ=0 EndX=84.7 EndY=47.8611 EndZ=0
    g6: LineSegment StartX=84.7 StartY=33.8611 StartZ=0 EndX=93.9 EndY=33.8611 EndZ=0
    g7: LineSegment StartX=81.2 StartY=44.754 StartZ=0 EndX=81.2 EndY=37.3867 EndZ=0
    g8: ArcOfCircle CenterX=84.6779 CenterY=44.3611 CenterZ=0 NormalX=0 NormalY=0 NormalZ=1 AngleXU=0 Radius=3.5 StartAngle=1.56447 EndAngle=3.02909
    g9: ArcOfCircle CenterX=84.6999 CenterY=37.3611 CenterZ=0 NormalX=0 NormalY=0 NormalZ=1 AngleXU=0 Radius=3.5 StartAngle=3.13426 EndAngle=4.71242
    g10: LineSegment StartX=93.9 StartY=47.8611 StartZ=0 EndX=93.9 EndY=45.8611 EndZ=0
    g11: LineSegment StartX=93.9 StartY=33.8611 StartZ=0 EndX=93.9 EndY=35.8611 EndZ=0
  constraints (22):
    c: Horizontal(g0)
    c: Horizontal(g1)
    c: Coincident(g3,g2)
    c: Coincident(g3,g0)
    c: Coincident(g4,g2)
    c: Coincident(g4,g1)
    c: Radius(g4) = 2
    c: Radius(g3) = 2
    c: Horizontal(g5)
    c: Horizontal(g6)
    c: Vertical(g7)
    c: DistanceX(g7,g2) = 2
    c: Coincident(g8,g7)
    c: Coincident(g8,g5)
    c: Coincident(g9,g7)
    c: Coincident(g9,g6)
    c: Radius(g9) = 3.5
    c: Radius(g8) = 3.5
    c: Coincident(g10,g5)
    c: Coincident(g10,g0)
    c: Coincident(g11,g6)
    c: Coincident(g11,g1)
FEATURE [PartDesign::Pad] Pad113
  BaseFeature = -> Chamfer006
  Direction = (0,0,1)
  Length = 2
  Length2 = 10
  Profile = -> Sketch088
  ReferenceAxis = -> Sketch088 [N_Axis]
  Refine = true
  Type = 0
FEATURE [Part::Part2DObjectPython] ShapeString018  # Draft 2D object (typed FeaturePython)
  FontFile = <userpath>/Documents/FreeCad/Fonts/Stencil_tenada/Tenada.ttf
  MakeFace = true
  Placement = pos=(9.94,53.93,2) rot=(0,0,1;0rad)
  Size = 2.7
  String = Smart Water Pump
  Tracking = 0
FEATURE [Part::Part2DObjectPython] ShapeString019  # Draft 2D object (typed FeaturePython)
  FontFile = <userpath>/Documents/FreeCad/Fonts/Stencil_tenada/Tenada.ttf
  MakeFace = true
  Placement = pos=(32,42.9,2) rot=(0,0,1;0rad)
  Size = 2.5
  String = Controller S1
  Tracking = 0
FEATURE [Sketcher::SketchObject] Sketch089
  FullyConstrained = true
  MapMode = 5
  Support = -> [XY_Plane122]
  sketch-geometry (10):
    g0: LineSegment StartX=21 StartY=100.55 StartZ=0 EndX=21 EndY=64.55 EndZ=0
    g1: LineSegment StartX=21 StartY=64.55 StartZ=0 EndX=4.2 EndY=64.55 EndZ=0
    g2: LineSegment StartX=93.5 StartY=15.2 StartZ=0 EndX=93.5 EndY=65.2 EndZ=0
    g3: LineSegment StartX=93.5 StartY=65.2 StartZ=0 EndX=80.9 EndY=65.2 EndZ=0
    g4: LineSegment StartX=80.9 StartY=65.2 StartZ=0 EndX=80.9 EndY=100.55 EndZ=0
    g5: LineSegment StartX=80.9 StartY=100.55 StartZ=0 EndX=21 EndY=100.55 EndZ=0
    g6: LineSegment StartX=93.5 StartY=15.2 StartZ=0 EndX=30 EndY=15.2 EndZ=0
    g7: LineSegment StartX=30 StartY=15.2 StartZ=0 EndX=30 EndY=49.55 EndZ=0
    g8: LineSegment StartX=30 StartY=49.55 StartZ=0 EndX=4.2 EndY=49.55 EndZ=0
    g9: LineSegment StartX=4.2 StartY=49.55 StartZ=0 EndX=4.2 EndY=64.55 EndZ=0
  constraints (30):
    c: Vertical(g0)
    c: Coincident(g0,g1)
    c: Horizontal(g1)
    c: Vertical(g2)
    c: Coincident(g2,g3)
    c: Coincident(g3,g4)
    c: Vertical(g4)
    c: Coincident(g4,g5)
    c: Coincident(g5,g0)
    c: Horizontal(g5)
    c: Horizontal(g3)
    c: Coincident(g2,g6)
    c: Horizontal(g6)
    c: Coincident(g6,g7)
    c: Vertical(g7)
    c: Coincident(g7,g8)
    c: Horizontal(g8)
    c: Coincident(g8,g9)
    c: Coincident(g9,g1)
    c: Vertical(g9)
    c: DistanceY(g-1,g6) = 15.2
    c: DistanceX(g-1,g6) = 30
    c: DistanceX(g8,g7) = 25.8
    c: DistanceX(g6,g6) = 63.5
    c: DistanceY(g2,g2) = 50
    c: DistanceY(g7,g7) = 34.35
    c: DistanceY(g9,g9) = 15
    c: DistanceY(g0,g0) = 36
    c: DistanceX(g5,g5) = 59.9
    c: DistanceX(g3,g3) = 12.6
FEATURE [PartDesign::Pad] Pad114
  Direction = (0,0,1)
  Length = 2
  Length2 = 10
  Profile = -> Sketch089
  ReferenceAxis = -> Sketch089 [N_Axis]
  Refine = true
  Type = 0
FEATURE [Sketcher::SketchObject] Sketch090
  FullyConstrained = false
  MapMode = 5
  Support = -> [XY_Plane123]
  sketch-geometry (4):
    g0: LineSegment StartX=4.34912 StartY=50.7797 StartZ=0 EndX=32.5138 EndY=50.7797 EndZ=0
    g1: LineSegment StartX=32.5138 StartY=50.7797 StartZ=0 EndX=32.5138 EndY=14.7356 EndZ=0
    g2: LineSegment StartX=32.5138 StartY=14.7356 StartZ=0 EndX=4.34912 EndY=14.7356 EndZ=0
    g3: LineSegment StartX=4.34912 StartY=14.7356 StartZ=0 EndX=4.34912 EndY=50.7797 EndZ=0
  constraints (8):
    c: Coincident(g0,g1)
    c: Coincident(g1,g2)
    c: Coincident(g2,g3)
    c: Coincident(g3,g0)
    c: Horizontal(g0)
    c: Horizontal(g2)
    c: Vertical(g1)
    c: Vertical(g3)
FEATURE [PartDesign::Pad] Pad115
  Direction = (0,0,1)
  Length = 2
  Length2 = 10
  Profile = -> Sketch090
  ReferenceAxis = -> Sketch090 [N_Axis]
  Refine = true
  Type = 0
FEATURE [Sketcher::SketchObject] Sketch091
  ExternalGeometry = -> [Pad115]
  FullyConstrained = true
  MapMode = 5
  Placement = pos=(0,0,0) rot=(1,0,0;3.14159rad)
  Support = -> [Pad115]
  sketch-geometry (6):
    g0: LineSegment StartX=4.34912 StartY=-50.7797 StartZ=0 EndX=4.34912 EndY=-14.7356 EndZ=0
    g1: LineSegment StartX=4.34912 StartY=-14.7356 StartZ=0 EndX=32.5138 EndY=-14.7356 EndZ=0
    g2: LineSegment StartX=32.5138 StartY=-14.7356 StartZ=0 EndX=32.5138 EndY=-16.2356 EndZ=0
    g3: LineSegment StartX=32.5138 StartY=-16.2356 StartZ=0 EndX=5.84912 EndY=-16.2356 EndZ=0
    g4: LineSegment StartX=5.84912 StartY=-16.2356 StartZ=0 EndX=5.84912 EndY=-50.7797 EndZ=0
    g5: LineSegment StartX=5.84912 StartY=-50.7797 StartZ=0 EndX=4.34912 EndY=-50.7797 EndZ=0
  constraints (15):
    c: Coincident(g-3,g0)
    c: Coincident(g0,g-4)
    c: Coincident(g0,g1)
    c: Coincident(g1,g-4)
    c: Coincident(g1,g2)
    c: Vertical(g2)
    c: Coincident(g2,g3)
    c: Horizontal(g3)
    c: Coincident(g3,g4)
    c: Vertical(g4)
    c: Coincident(g4,g5)
    c: Coincident(g5,g0)
    c: DistanceY(g2,g1) = 1.5
    c: DistanceX(g0,g4) = 1.5
    c: PointOnObject(g4,g-5)
FEATURE [PartDesign::Pad] Pad116
  BaseFeature = -> Pad115
  Direction = (0,0,-1)
  Length = 22
  Length2 = 10
  Profile = -> Sketch091
  ReferenceAxis = -> Sketch091 [N_Axis]
  Refine = true
  Type = 0
FEATURE [Sketcher::SketchObject] Sketch092
  ExternalGeometry = -> [Pad116]
  FullyConstrained = true
  MapMode = 5
  Placement = pos=(0,0,2) rot=(0,0,1;0rad)
  Support = -> [Pad116]
  sketch-geometry (4):
    g0: LineSegment StartX=9.59912 StartY=43.7856 StartZ=0 EndX=25.0991 EndY=43.7856 EndZ=0
    g1: LineSegment StartX=25.0991 StartY=43.7856 StartZ=0 EndX=25.0991 EndY=22.4856 EndZ=0
    g2: LineSegment StartX=25.0991 StartY=22.4856 StartZ=0 EndX=9.59912 EndY=22.4856 EndZ=0
    g3: LineSegment StartX=9.59912 StartY=22.4856 StartZ=0 EndX=9.59912 EndY=43.7856 EndZ=0
  constraints (12):
    c: Coincident(g0,g1)
    c: Coincident(g1,g2)
    c: Coincident(g2,g3)
    c: Coincident(g3,g0)
    c: Horizontal(g0)
    c: Horizontal(g2)
    c: Vertical(g1)
    c: Vertical(g3)
    c: DistanceX(g0,g0) = 15.5
    c: DistanceY(g1,g0) = 21.3
    c: DistanceY(g-4,g2) = 7.75
    c: DistanceX(g-4,g2) = 5.25
FEATURE [PartDesign::Pocket] Pocket074
  BaseFeature = -> Pad116
  Direction = (0,0,-1)
  Length = 5
  Length2 = 5
  Profile = -> Sketch092
  ReferenceAxis = -> Sketch092 [N_Axis]
  Refine = true
  Type = 0
FEATURE [PartDesign::Pad] Pad120
  BaseFeature = -> Pocket074
  Direction = (0,-1,0)
  Length = 0.5
  Length2 = 10
  Profile = -> Pocket074 [Face5]
  Refine = true
  Type = 0
FEATURE [PartDesign::Pad] Pad121
  BaseFeature = -> Pad120
  Direction = (-1,0,0)
  Length = 0.5
  Length2 = 10
  Profile = -> Pad120 [Face11]
  Refine = true
  Type = 0
FEATURE [PartDesign::Pocket] Pocket089
  BaseFeature = -> Pad121
  Direction = (0,-1,-1e-16)
  Length = 1
  Length2 = 5
  Profile = -> Pad121 [Face9]
  Refine = true
  Type = 0
FEATURE [PartDesign::Pocket] Pocket090
  BaseFeature = -> Pocket089
  Direction = (-1,0,0)
  Length = 1
  Length2 = 5
  Profile = -> Pocket089 [Face1]
  Refine = true
  Type = 0
FEATURE [PartDesign::Fillet] Fillet008
  Base = -> Pocket090 [Edge27,Edge22,Edge25,Edge23]
  BaseFeature = -> Pocket090
  Radius = 1
  Refine = true
  SupportTransform = false
  UseAllEdges = false
FEATURE [PartDesign::Pad] Pad139
  BaseFeature = -> Fillet008
  Direction = (0,0,1)
  Length = 2
  Length2 = 10
  Profile = -> Fillet008 [Face14]
  Refine = true
  Type = 0
FEATURE [PartDesign::Pocket] Pocket091
  BaseFeature = -> Pad139
  Direction = (0,0,1)
  Length = 2
  Length2 = 5
  Profile = -> Pad139 [Face1]
  Refine = true
  Type = 0
FEATURE [PartDesign::Body] Body006  label="LidBoton002"
  Group = -> [Sketch090,Pad115,Sketch091,Pad116,Sketch092,Pocket074,Pad120,Pad121,Pocket089,Pocket090,Fillet008,Pad139,Pocket091]
  Origin = -> Origin123
  Placement = pos=(-0.2,0.465,-28.99) rot=(0,0,1;0rad)
  Tip = -> Pocket091
FEATURE [Sketcher::SketchObject] Sketch093
  ExternalGeometry = -> [Pad114]
  FullyConstrained = true
  MapMode = 5
  Placement = pos=(0,0,0) rot=(1,0,0;3.14159rad)
  Support = -> [Pad114]
  sketch-geometry (8):
    g0: LineSegment StartX=30 StartY=-15.2 StartZ=0 EndX=93.5 EndY=-15.2 EndZ=0
    g1: LineSegment StartX=93.5 StartY=-15.2 StartZ=0 EndX=93.5 EndY=-16.7 EndZ=0
    g2: LineSegment StartX=93.5 StartY=-16.7 StartZ=0 EndX=30 EndY=-16.7 EndZ=0
    g3: LineSegment StartX=30 StartY=-16.7 StartZ=0 EndX=30 EndY=-15.2 EndZ=0
    g4: LineSegment StartX=21 StartY=-100.55 StartZ=0 EndX=80.9 EndY=-100.55 EndZ=0
    g5: LineSegment StartX=80.9 StartY=-100.55 StartZ=0 EndX=80.9 EndY=-99.35 EndZ=0
    g6: LineSegment StartX=80.9 StartY=-99.35 StartZ=0 EndX=21 EndY=-99.35 EndZ=0
    g7: LineSegment StartX=21 StartY=-99.35 StartZ=0 EndX=21 EndY=-100.55 EndZ=0
  constraints (22):
    c: Coincident(g0,g1)
    c: Coincident(g1,g2)
    c: Coincident(g2,g3)
    c: Coincident(g3,g0)
    c: Horizontal(g0)
    c: Horizontal(g2)
    c: Vertical(g1)
    c: Vertical(g3)
    c: Coincident(g0,g-4)
    c: PointOnObject(g1,g-5)
    c: DistanceY(g1,g1) = 1.5
    c: Coincident(g4,g5)
    c: Coincident(g5,g6)
    c: Coincident(g6,g7)
    c: Coincident(g7,g4)
    c: Horizontal(g4)
    c: Horizontal(g6)
    c: Vertical(g5)
    c: Vertical(g7)
    c: Coincident(g4,g-10)
    c: DistanceY(g5,g5) = 1.2
    c: PointOnObject(g5,g-11)
FEATURE [PartDesign::Pad] Pad117
  BaseFeature = -> Pad114
  Direction = (0,0,-1)
  Length = 51
  Length2 = 10
  Profile = -> Sketch093
  ReferenceAxis = -> Sketch093 [N_Axis]
  Refine = true
  Type = 0
FEATURE [PartDesign::Pad] Pad118
  BaseFeature = -> Pad117
  Direction = (0,1,0)
  Length = 0.6
  Length2 = 10
  Profile = -> Pad117 [Face16]
  Refine = true
  Type = 0
FEATURE [PartDesign::Pad] Pad119
  BaseFeature = -> Pad118
  Direction = (0,-1,0)
  Length = 0.5
  Length2 = 10
  Profile = -> Pad118 [Face4]
  Refine = true
  Type = 0
FEATURE [Sketcher::SketchObject] Sketch094
  ExternalGeometry = -> [Pad119]
  FullyConstrained = true
  MapMode = 5
  Placement = pos=(0,0,0) rot=(1,0,0;3.14159rad)
  Support = -> [Pad119]
  sketch-geometry (6):
    g0: LineSegment StartX=30 StartY=-16.7 StartZ=0 EndX=32 EndY=-16.7 EndZ=0
    g1: LineSegment StartX=32 StartY=-16.7 StartZ=0 EndX=32 EndY=-51.55 EndZ=0
    g2: LineSegment StartX=32 StartY=-51.55 StartZ=0 EndX=4.2 EndY=-51.55 EndZ=0
    g3: LineSegment StartX=4.2 StartY=-51.55 StartZ=0 EndX=4.2 EndY=-49.55 EndZ=0
    g4: LineSegment StartX=4.2 StartY=-49.55 StartZ=0 EndX=30 EndY=-49.55 EndZ=0
    g5: LineSegment StartX=30 StartY=-49.55 StartZ=0 EndX=30 EndY=-16.7 EndZ=0
  constraints (15):
    c: Coincident(g-4,g0)
    c: PointOnObject(g0,g-4)
    c: Coincident(g0,g1)
    c: Vertical(g1)
    c: Coincident(g1,g2)
    c: Horizontal(g2)
    c: Coincident(g2,g3)
    c: Coincident(g3,g-5)
    c: Coincident(g3,g4)
    c: Coincident(g4,g-5)
    c: Coincident(g4,g5)
    c: Coincident(g5,g0)
    c: Vertical(g3)
    c: DistanceY(g3,g3) = 2
    c: DistanceX(g0,g0) = 2
FEATURE [PartDesign::Pad] Pad122
  BaseFeature = -> Pad119
  Direction = (0,0,-1)
  Length = 29
  Length2 = 10
  Profile = -> Sketch094
  ReferenceAxis = -> Sketch094 [N_Axis]
  Refine = true
  Type = 0
FEATURE [Sketcher::SketchObject] Sketch095
  ExternalGeometry = -> [Pad122]
  FullyConstrained = true
  MapMode = 5
  Placement = pos=(0,0,0) rot=(1,0,0;3.14159rad)
  Support = -> [Pad122]
  sketch-geometry (4):
    g0: LineSegment StartX=4.2 StartY=-64.55 StartZ=0 EndX=6.2 EndY=-64.55 EndZ=0
    g1: LineSegment StartX=6.2 StartY=-64.55 StartZ=0 EndX=6.2 EndY=-51.55 EndZ=0
    g2: LineSegment StartX=6.2 StartY=-51.55 StartZ=0 EndX=4.2 EndY=-51.55 EndZ=0
    g3: LineSegment StartX=4.2 StartY=-51.55 StartZ=0 EndX=4.2 EndY=-64.55 EndZ=0
  constraints (11):
    c: Coincident(g0,g1)
    c: Coincident(g1,g2)
    c: Coincident(g2,g3)
    c: Coincident(g3,g0)
    c: Horizontal(g0)
    c: Horizontal(g2)
    c: Vertical(g1)
    c: Vertical(g3)
    c: Coincident(g0,g-4)
    c: PointOnObject(g1,g-5)
    c: DistanceX(g2,g2) = 2
FEATURE [PartDesign::Pad] Pad123
  BaseFeature = -> Pad122
  Direction = (0,0,-1)
  Length = 51
  Length2 = 10
  Profile = -> Sketch095
  ReferenceAxis = -> Sketch095 [N_Axis]
  Refine = true
  Type = 0
FEATURE [PartDesign::Pocket] Pocket075
  BaseFeature = -> Pad123
  Direction = (0,-1,0)
  Length = 1.5
  Length2 = 5
  Profile = -> Pad123 [Face21]
  Refine = true
  Type = 0
FEATURE [PartDesign::Pad] Pad124
  BaseFeature = -> Pocket075
  Direction = (-1,0,0)
  Length = 0.55
  Length2 = 10
  Profile = -> Pocket075 [Face18]
  Refine = true
  Type = 0
FEATURE [PartDesign::Pad] Pad125
  BaseFeature = -> Pad124
  Direction = (0,-1,0)
  Length = 1
  Length2 = 10
  Profile = -> Pad124 [Face19]
  Refine = true
  Type = 0
FEATURE [Sketcher::SketchObject] Sketch096
  ExternalGeometry = -> [Pad125]
  FullyConstrained = true
  MapMode = 5
  Placement = pos=(0,0,0) rot=(1,0,0;3.14159rad)
  Support = -> [Pad125]
  sketch-geometry (6):
    g0: LineSegment StartX=6.2 StartY=-63.05 StartZ=0 EndX=21 EndY=-63.05 EndZ=0
    g1: LineSegment StartX=21 StartY=-63.05 StartZ=0 EndX=21 EndY=-99.35 EndZ=0
    g2: LineSegment StartX=21 StartY=-99.35 StartZ=0 EndX=23 EndY=-99.35 EndZ=0
    g3: LineSegment StartX=23 StartY=-99.35 StartZ=0 EndX=23 EndY=-61.05 EndZ=0
    g4: LineSegment StartX=23 StartY=-61.05 StartZ=0 EndX=6.2 EndY=-61.05 EndZ=0
    g5: LineSegment StartX=6.2 StartY=-61.05 StartZ=0 EndX=6.2 EndY=-63.05 EndZ=0
  constraints (15):
    c: Coincident(g-4,g0)
    c: Coincident(g0,g-4)
    c: Coincident(g0,g1)
    c: Coincident(g1,g-3)
    c: Coincident(g1,g2)
    c: Horizontal(g2)
    c: Coincident(g2,g3)
    c: Vertical(g3)
    c: Coincident(g3,g4)
    c: Horizontal(g4)
    c: Coincident(g4,g5)
    c: Coincident(g5,g0)
    c: Vertical(g5)
    c: DistanceX(g2,g2) = 2
    c: DistanceY(g5,g5) = 2
FEATURE [PartDesign::Pad] Pad126
  BaseFeature = -> Pad125
  Direction = (0,0,-1)
  Length = 38.6
  Length2 = 10
  Profile = -> Sketch096
  ReferenceAxis = -> Sketch096 [N_Axis]
  Refine = true
  Type = 0
FEATURE [Sketcher::SketchObject] Sketch097
  ExternalGeometry = -> [Pad126]
  FullyConstrained = true
  MapMode = 5
  Placement = pos=(0,0,0) rot=(1,0,0;3.14159rad)
  Support = -> [Pad126]
  sketch-geometry (4):
    g0: LineSegment StartX=93.5 StartY=-65.2 StartZ=0 EndX=91.5 EndY=-65.2 EndZ=0
    g1: LineSegment StartX=91.5 StartY=-65.2 StartZ=0 EndX=91.5 EndY=-16.7 EndZ=0
    g2: LineSegment StartX=91.5 StartY=-16.7 StartZ=0 EndX=93.5 EndY=-16.7 EndZ=0
    g3: LineSegment StartX=93.5 StartY=-16.7 StartZ=0 EndX=93.5 EndY=-65.2 EndZ=0
  constraints (11):
    c: Coincident(g0,g1)
    c: Coincident(g1,g2)
    c: Coincident(g2,g3)
    c: Coincident(g3,g0)
    c: Horizontal(g0)
    c: Horizontal(g2)
    c: Vertical(g1)
    c: Vertical(g3)
    c: Coincident(g0,g-5)
    c: PointOnObject(g1,g-4)
    c: DistanceX(g0,g0) = 2
FEATURE [PartDesign::Pad] Pad127
  BaseFeature = -> Pad126
  Direction = (0,0,-1)
  Length = 28.7
  Length2 = 10
  Profile = -> Sketch097
  ReferenceAxis = -> Sketch097 [N_Axis]
  Refine = true
  Type = 0
FEATURE [Sketcher::SketchObject] Sketch098
  ExternalGeometry = -> [Pad127]
  FullyConstrained = true
  MapMode = 5
  Placement = pos=(0,0,-28.7) rot=(1,0,0;3.14159rad)
  Support = -> [Pad127]
  sketch-geometry (4):
    g0: LineSegment StartX=91.5 StartY=-65.2 StartZ=0 EndX=93.5 EndY=-65.2 EndZ=0
    g1: LineSegment StartX=93.5 StartY=-65.2 StartZ=0 EndX=93.5 EndY=-30.4 EndZ=0
    g2: LineSegment StartX=93.5 StartY=-30.4 StartZ=0 EndX=91.5 EndY=-30.4 EndZ=0
    g3: LineSegment StartX=91.5 StartY=-30.4 StartZ=0 EndX=91.5 EndY=-65.2 EndZ=0
  constraints (11):
    c: Coincident(g0,g1)
    c: Coincident(g1,g2)
    c: Coincident(g2,g3)
    c: Coincident(g3,g0)
    c: Horizontal(g0)
    c: Horizontal(g2)
    c: Vertical(g1)
    c: Vertical(g3)
    c: Coincident(g0,g-5)
    c: PointOnObject(g1,g-3)
    c: DistanceY(g1,g1) = 34.8
FEATURE [PartDesign::Pad] Pad128
  BaseFeature = -> Pad127
  Direction = (0,0,-1)
  Length = 22.4
  Length2 = 10
  Profile = -> Sketch098
  ReferenceAxis = -> Sketch098 [N_Axis]
  Refine = true
  Type = 0
FEATURE [PartDesign::Pocket] Pocket076
  BaseFeature = -> Pad128
  Direction = (0,-1,0)
  Length = 1.9
  Length2 = 5
  Profile = -> Pad128 [Face27]
  Refine = true
  Type = 0
FEATURE [Sketcher::SketchObject] Sketch099
  ExternalGeometry = -> [Pocket076]
  FullyConstrained = true
  MapMode = 5
  Placement = pos=(0,0,0) rot=(1,0,0;3.14159rad)
  Support = -> [Pocket076]
  sketch-geometry (4):
    g0: LineSegment StartX=80.9 StartY=-63.3 StartZ=0 EndX=78.9 EndY=-63.3 EndZ=0
    g1: LineSegment StartX=78.9 StartY=-63.3 StartZ=0 EndX=78.9 EndY=-99.35 EndZ=0
    g2: LineSegment StartX=78.9 StartY=-99.35 StartZ=0 EndX=80.9 EndY=-99.35 EndZ=0
    g3: LineSegment StartX=80.9 StartY=-99.35 StartZ=0 EndX=80.9 EndY=-63.3 EndZ=0
  constraints (11):
    c: Coincident(g0,g1)
    c: Coincident(g1,g2)
    c: Coincident(g2,g3)
    c: Coincident(g3,g0)
    c: Horizontal(g0)
    c: Horizontal(g2)
    c: Vertical(g1)
    c: Vertical(g3)
    c: Coincident(g0,g-3)
    c: PointOnObject(g1,g-4)
    c: DistanceX(g0,g0) = 2
FEATURE [PartDesign::Pad] Pad129
  BaseFeature = -> Pocket076
  Direction = (0,0,-1)
  Length = 38.6
  Length2 = 10
  Profile = -> Sketch099
  ReferenceAxis = -> Sketch099 [N_Axis]
  Refine = true
  Type = 0
FEATURE [Sketcher::SketchObject] Sketch100
  ExternalGeometry = -> [Pad129]
  FullyConstrained = true
  MapMode = 5
  Placement = pos=(0,63.3,0) rot=(0,0.707107,0.707107;3.14159rad)
  Support = -> [Pad129]
  sketch-geometry (4):
    g0: LineSegment StartX=-93.5 StartY=2 StartZ=0 EndX=-91.5 EndY=2 EndZ=0
    g1: LineSegment StartX=-91.5 StartY=2 StartZ=0 EndX=-91.5 EndY=-38 EndZ=0
    g2: LineSegment StartX=-91.5 StartY=-38 StartZ=0 EndX=-93.5 EndY=-38 EndZ=0
    g3: LineSegment StartX=-93.5 StartY=-38 StartZ=0 EndX=-93.5 EndY=2 EndZ=0
  constraints (11):
    c: Coincident(g0,g1)
    c: Coincident(g1,g2)
    c: Coincident(g2,g3)
    c: Coincident(g3,g0)
    c: Horizontal(g0)
    c: Horizontal(g2)
    c: Vertical(g1)
    c: Vertical(g3)
    c: Coincident(g0,g-4)
    c: PointOnObject(g1,g-6)
    c: DistanceY(g3,g3) = 40
FEATURE [PartDesign::Pad] Pad130
  BaseFeature = -> Pad129
  Direction = (0,1,-2e-16)
  Length = 2.8
  Length2 = 10
  Profile = -> Sketch100
  ReferenceAxis = -> Sketch100 [N_Axis]
  Refine = true
  Type = 0
FEATURE [Sketcher::SketchObject] Sketch101
  ExternalGeometry = -> [Pad130]
  FullyConstrained = true
  MapMode = 5
  Placement = pos=(91.5,0,0) rot=(0.57735,-0.57735,-0.57735;2.0944rad)
  Support = -> [Pad130]
  sketch-geometry (4):
    g0: LineSegment StartX=-66.1 StartY=-38 StartZ=0 EndX=-64.6 EndY=-38 EndZ=0
    g1: LineSegment StartX=-64.6 StartY=-38 StartZ=0 EndX=-64.6 EndY=2 EndZ=0
    g2: LineSegment StartX=-64.6 StartY=2 StartZ=0 EndX=-66.1 EndY=2 EndZ=0
    g3: LineSegment StartX=-66.1 StartY=2 StartZ=0 EndX=-66.1 EndY=-38 EndZ=0
  constraints (11):
    c: Coincident(g0,g1)
    c: Coincident(g1,g2)
    c: Coincident(g2,g3)
    c: Coincident(g3,g0)
    c: Horizontal(g0)
    c: Horizontal(g2)
    c: Vertical(g1)
    c: Vertical(g3)
    c: Coincident(g0,g-5)
    c: PointOnObject(g1,g-4)
    c: DistanceX(g2,g2) = 1.5
FEATURE [PartDesign::Pad] Pad131
  BaseFeature = -> Pad130
  Direction = (-1,0,0)
  Length = 11
  Length2 = 10
  Profile = -> Sketch101
  ReferenceAxis = -> Sketch101 [N_Axis]
  Refine = true
  Type = 0
FEATURE [PartDesign::Pad] Pad132
  BaseFeature = -> Pad131
  Direction = (0,1,0)
  Length = 2
  Length2 = 10
  Profile = -> Pad131 [Face11]
  Refine = true
  Type = 0
FEATURE [PartDesign::Pocket] Pocket077
  BaseFeature = -> Pad132
  Direction = (-1,0,0)
  Length = 0.6
  Length2 = 5
  Profile = -> Pad132 [Face4]
  Refine = true
  Type = 0
FEATURE [PartDesign::Pocket] Pocket078
  BaseFeature = -> Pocket077
  Direction = (1,0,0)
  Length = 0.4
  Length2 = 5
  Profile = -> Pocket077 [Face10]
  Refine = true
  Type = 0
FEATURE [PartDesign::Pad] Pad133
  BaseFeature = -> Pocket078
  Direction = (1,0,-1e-16)
  Length = 0.4
  Length2 = 10
  Profile = -> Pocket078 [Face21]
  Refine = true
  Type = 0
FEATURE [Sketcher::SketchObject] Sketch102
  ExternalGeometry = -> [Pad133]
  FullyConstrained = true
  MapMode = 5
  Placement = pos=(93.9,1.9e-15,-1.13e-14) rot=(0.57735,0.57735,0.57735;2.0944rad)
  Support = -> [Pad133]
  sketch-geometry (1):
    g0: Circle CenterX=52.6 CenterY=-47.4 CenterZ=0 NormalX=0 NormalY=0 NormalZ=1 AngleXU=0 Radius=1.5
  constraints (3):
    c: Diameter(g0) = 3
    c: DistanceY(g-4,g0) = 3.7
    c: DistanceX(g0,g-4) = 10.7
FEATURE [PartDesign::Pocket] Pocket079
  BaseFeature = -> Pad133
  Direction = (-1,1e-16,1e-16)
  Length = 5
  Length2 = 5
  Profile = -> Sketch102
  ReferenceAxis = -> Sketch102 [N_Axis]
  Refine = true
  Type = 0
FEATURE [Sketcher::SketchObject] Sketch103
  ExternalGeometry = -> [Pocket079]
  FullyConstrained = true
  MapMode = 5
  Placement = pos=(3.65,0,0) rot=(0.57735,-0.57735,-0.57735;2.0944rad)
  Support = -> [Pocket079]
  sketch-geometry (1):
    g0: Circle CenterX=-57.43 CenterY=-47.38 CenterZ=0 NormalX=0 NormalY=0 NormalZ=1 AngleXU=0 Radius=1.5
  constraints (3):
    c: Diameter(g0) = 3
    c: DistanceY(g-3,g0) = 3.62
    c: DistanceX(g-3,g0) = 5.62
FEATURE [PartDesign::Pocket] Pocket080
  BaseFeature = -> Pocket079
  Direction = (1,0,0)
  Length = 5
  Length2 = 5
  Profile = -> Sketch103
  ReferenceAxis = -> Sketch103 [N_Axis]
  Refine = true
  Type = 0
FEATURE [PartDesign::Pocket] Pocket081
  BaseFeature = -> Pocket080
  Direction = (1,0,0)
  Length = 0.5
  Length2 = 5
  Profile = -> Pocket080 [Face19]
  Refine = true
  Type = 0
FEATURE [PartDesign::Pocket] Pocket082
  BaseFeature = -> Pocket081
  Direction = (0,1,0)
  Length = 1.2
  Length2 = 5
  Profile = -> Pocket081 [Face1]
  Refine = true
  Type = 0
FEATURE [Sketcher::SketchObject] Sketch104
  ExternalGeometry = -> [Pocket082]
  FullyConstrained = true
  MapMode = 5
  Placement = pos=(0,1e-16,2) rot=(0,0,1;0rad)
  Support = -> [Pocket082]
  sketch-geometry (2):
    g0: Circle CenterX=85.55 CenterY=36.6 CenterZ=0 NormalX=0 NormalY=0 NormalZ=1 AngleXU=0 Radius=2.5
    g1: Circle CenterX=85.55 CenterY=44 CenterZ=0 NormalX=0 NormalY=0 NormalZ=1 AngleXU=0 Radius=2.5
  constraints (6):
    c: Diameter(g1) = 5
    c: Diameter(g0) = 5
    c: DistanceY(g0,g1) = 7.4
    c: DistanceY(g-4,g0) = 21.9
    c: DistanceX(g0,g-4) = 8.35
    c: DistanceX(g1,g0) = 0
FEATURE [PartDesign::Pocket] Pocket083
  BaseFeature = -> Pocket082
  Direction = (0,0,-1)
  Length = 5
  Length2 = 5
  Profile = -> Sketch104
  ReferenceAxis = -> Sketch104 [N_Axis]
  Refine = true
  Type = 0
FEATURE [Sketcher::SketchObject] Sketch105
  ExternalGeometry = -> [Pocket083]
  FullyConstrained = true
  MapMode = 5
  Placement = pos=(0,0,0) rot=(1,0,0;3.14159rad)
  Support = -> [Pocket083]
  sketch-geometry (4):
    g0: Circle CenterX=85.55 CenterY=-36.6 CenterZ=0 NormalX=0 NormalY=0 NormalZ=1 AngleXU=0 Radius=2.5
    g1: Circle CenterX=85.55 CenterY=-44 CenterZ=0 NormalX=0 NormalY=0 NormalZ=1 AngleXU=0 Radius=2.5
    g2: Circle CenterX=85.55 CenterY=-36.6 CenterZ=0 NormalX=0 NormalY=0 NormalZ=1 AngleXU=0 Radius=4
    g3: Circle CenterX=85.55 CenterY=-44 CenterZ=0 NormalX=0 NormalY=0 NormalZ=1 AngleXU=0 Radius=4
  constraints (8):
    c: Coincident(g0,g-3)
    c: Coincident(g1,g-4)
    c: Diameter(g0) = 5
    c: Diameter(g1) = 5
    c: Coincident(g2,g0)
    c: Coincident(g3,g1)
    c: Diameter(g2) = 8
    c: Diameter(g3) = 8
FEATURE [PartDesign::Pad] Pad134
  BaseFeature = -> Pocket083
  Direction = (0,0,-1)
  Length = 38
  Length2 = 10
  Profile = -> Sketch105
  ReferenceAxis = -> Sketch105 [N_Axis]
  Refine = true
  Type = 0
FEATURE [Sketcher::SketchObject] Sketch106
  ExternalGeometry = -> [Pad134]
  FullyConstrained = true
  MapMode = 5
  Placement = pos=(91.9,0,0) rot=(0.57735,-0.57735,-0.57735;2.0944rad)
  Support = -> [Pad134]
  sketch-geometry (4):
    g0: LineSegment StartX=-62.1 StartY=-11.8 StartZ=0 EndX=-53.3 EndY=-11.8 EndZ=0
    g1: LineSegment StartX=-53.3 StartY=-11.8 StartZ=0 EndX=-53.3 EndY=-3 EndZ=0
    g2: LineSegment StartX=-53.3 StartY=-3 StartZ=0 EndX=-62.1 EndY=-3 EndZ=0
    g3: LineSegment StartX=-62.1 StartY=-3 StartZ=0 EndX=-62.1 EndY=-11.8 EndZ=0
  constraints (12):
    c: Coincident(g0,g1)
    c: Coincident(g1,g2)
    c: Coincident(g2,g3)
    c: Coincident(g3,g0)
    c: Horizontal(g0)
    c: Horizontal(g2)
    c: Vertical(g1)
    c: Vertical(g3)
    c: DistanceY(g3,g3) = 8.8
    c: DistanceX(g2,g2) = 8.8
    c: DistanceY(g1,g-4) = 5
    c: DistanceX(g-4,g2) = 4
FEATURE [PartDesign::Pocket] Pocket084
  BaseFeature = -> Pad134
  Direction = (1,0,0)
  Length = 1
  Length2 = 5
  Profile = -> Sketch106
  ReferenceAxis = -> Sketch106 [N_Axis]
  Refine = true
  Type = 0
FEATURE [Sketcher::SketchObject] Sketch107
  ExternalGeometry = -> [Pocket084]
  FullyConstrained = true
  MapMode = 5
  Placement = pos=(92.9,0,0) rot=(0.57735,-0.57735,-0.57735;2.0944rad)
  Support = -> [Pocket084]
  sketch-geometry (1):
    g0: Circle CenterX=-57.7 CenterY=-7.4 CenterZ=0 NormalX=0 NormalY=0 NormalZ=1 AngleXU=0 Radius=3.5
  constraints (5):
    c: Diameter(g0) = 7
    c: DistanceX(g0,g-5) = 4.4
    c: DistanceX(g-4,g0) = 4.4
    c: DistanceY(g0,g-5) = 4.4
    c: DistanceY(g-5,g0) = 4.4
FEATURE [PartDesign::Pocket] Pocket085
  BaseFeature = -> Pocket084
  Direction = (1,0,0)
  Length = 5
  Length2 = 5
  Profile = -> Sketch107
  ReferenceAxis = -> Sketch107 [N_Axis]
  Refine = true
  Type = 0
FEATURE [Sketcher::SketchObject] Sketch108
  ExternalGeometry = -> [Pocket085]
  FullyConstrained = true
  MapMode = 5
  Placement = pos=(91.9,0,0) rot=(0.57735,-0.57735,-0.57735;2.0944rad)
  Support = -> [Pocket085]
  sketch-geometry (8):
    g0: LineSegment StartX=-64.6 StartY=-16 StartZ=0 EndX=-50.6 EndY=-16 EndZ=0
    g1: LineSegment StartX=-50.6 StartY=-16 StartZ=0 EndX=-50.6 EndY=0 EndZ=0
    g2: LineSegment StartX=-50.6 StartY=0 StartZ=0 EndX=-64.6 EndY=0 EndZ=0
    g3: LineSegment StartX=-64.6 StartY=0 StartZ=0 EndX=-64.6 EndY=-16 EndZ=0
    g4: LineSegment StartX=-62.1 StartY=-11.8 StartZ=0 EndX=-53.3 EndY=-11.8 EndZ=0
    g5: LineSegment StartX=-53.3 StartY=-11.8 StartZ=0 EndX=-53.3 EndY=-3 EndZ=0
    g6: LineSegment StartX=-53.3 StartY=-3 StartZ=0 EndX=-62.1 EndY=-3 EndZ=0
    g7: LineSegment StartX=-62.1 StartY=-3 StartZ=0 EndX=-62.1 EndY=-11.8 EndZ=0
  constraints (21):
    c: Coincident(g0,g1)
    c: Coincident(g1,g2)
    c: Coincident(g2,g3)
    c: Coincident(g3,g0)
    c: Horizontal(g0)
    c: Horizontal(g2)
    c: Vertical(g1)
    c: Vertical(g3)
    c: Coincident(g2,g-4)
    c: DistanceX(g2,g2) = 14
    c: DistanceY(g1,g1) = 16
    c: Coincident(g4,g5)
    c: Coincident(g5,g6)
    c: Coincident(g6,g7)
    c: Coincident(g7,g4)
    c: Horizontal(g4)
    c: Horizontal(g6)
    c: Vertical(g5)
    c: Vertical(g7)
    c: Coincident(g4,g-8)
    c: Coincident(g5,g-7)
FEATURE [PartDesign::Pad] Pad135
  BaseFeature = -> Pocket085
  Direction = (-1,0,0)
  Length = 2
  Length2 = 10
  Profile = -> Sketch108
  ReferenceAxis = -> Sketch108 [N_Axis]
  Refine = true
  Type = 0
FEATURE [PartDesign::Pad] Pad136
  BaseFeature = -> Pad135
  Direction = (-1,0,0)
  Length = 1
  Length2 = 10
  Profile = -> Pad135 [Face48]
  Refine = true
  Type = 0
FEATURE [Sketcher::SketchObject] Sketch109
  ExternalGeometry = -> [Pad136]
  FullyConstrained = true
  MapMode = 5
  Placement = pos=(0,1e-16,2) rot=(0,0,1;0rad)
  Support = -> [Pad136]
  sketch-geometry (4):
    g0: LineSegment StartX=39.5 StartY=78.15 StartZ=0 EndX=62.3 EndY=78.15 EndZ=0
    g1: LineSegment StartX=62.3 StartY=78.15 StartZ=0 EndX=62.3 EndY=65.35 EndZ=0
    g2: LineSegment StartX=62.3 StartY=65.35 StartZ=0 EndX=39.5 EndY=65.35 EndZ=0
    g3: LineSegment StartX=39.5 StartY=65.35 StartZ=0 EndX=39.5 EndY=78.15 EndZ=0
  constraints (12):
    c: Coincident(g0,g1)
    c: Coincident(g1,g2)
    c: Coincident(g2,g3)
    c: Coincident(g3,g0)
    c: Horizontal(g0)
    c: Horizontal(g2)
    c: Vertical(g1)
    c: Vertical(g3)
    c: DistanceX(g0,g0) = 22.8
    c: DistanceY(g1,g1) = 12.8
    c: DistanceY(g0,g-3) = 23
    c: DistanceX(g-4,g0) = 18.5
FEATURE [PartDesign::Pocket] Pocket086
  BaseFeature = -> Pad136
  Direction = (0,0,-1)
  Length = 5
  Length2 = 5
  Profile = -> Sketch109
  ReferenceAxis = -> Sketch109 [N_Axis]
  Refine = true
  Type = 0
FEATURE [Sketcher::SketchObject] Sketch110
  ExternalGeometry = -> [Pocket086]
  FullyConstrained = true
  MapMode = 5
  Placement = pos=(0,0,0) rot=(1,0,0;3.14159rad)
  Support = -> [Pocket086]
  sketch-geometry (8):
    g0: LineSegment StartX=37 StartY=-55.85 StartZ=0 EndX=64.8 EndY=-55.85 EndZ=0
    g1: LineSegment StartX=64.8 StartY=-55.85 StartZ=0 EndX=64.8 EndY=-84.65 EndZ=0
    g2: LineSegment StartX=64.8 StartY=-84.65 StartZ=0 EndX=37 EndY=-84.65 EndZ=0
    g3: LineSegment StartX=37 StartY=-84.65 StartZ=0 EndX=37 EndY=-55.85 EndZ=0
    g4: LineSegment StartX=35 StartY=-53.85 StartZ=0 EndX=66.8 EndY=-53.85 EndZ=0
    g5: LineSegment StartX=66.8 StartY=-53.85 StartZ=0 EndX=66.8 EndY=-86.65 EndZ=0
    g6: LineSegment StartX=66.8 StartY=-86.65 StartZ=0 EndX=35 EndY=-86.65 EndZ=0
    g7: LineSegment StartX=35 StartY=-86.65 StartZ=0 EndX=35 EndY=-53.85 EndZ=0
  constraints (24):
    c: Coincident(g0,g1)
    c: Coincident(g1,g2)
    c: Coincident(g2,g3)
    c: Coincident(g3,g0)
    c: Horizontal(g0)
    c: Horizontal(g2)
    c: Vertical(g1)
    c: Vertical(g3)
    c: Coincident(g4,g5)
    c: Coincident(g5,g6)
    c: Coincident(g6,g7)
    c: Coincident(g7,g4)
    c: Horizontal(g4)
    c: Horizontal(g6)
    c: Vertical(g5)
    c: Vertical(g7)
    c: DistanceY(g2,g-3) = 6.5
    c: DistanceY(g-4,g0) = 9.5
    c: DistanceY(g6,g2) = 2
    c: DistanceY(g0,g4) = 2
    c: DistanceX(g-3,g1) = 2.5
    c: DistanceX(g2,g-3) = 2.5
    c: DistanceX(g1,g5) = 2
    c: DistanceX(g4,g0) = 2
FEATURE [PartDesign::Pad] Pad137
  BaseFeature = -> Pocket086
  Direction = (0,0,-1)
  Length = 3
  Length2 = 10
  Profile = -> Sketch110
  ReferenceAxis = -> Sketch110 [N_Axis]
  Refine = true
  Type = 0
FEATURE [Part::Part2DObjectPython] ShapeString014  # Draft 2D object (typed FeaturePython)
  AttachmentOffset = pos=(22,53,0) rot=(0,0,1;0rad)
  FontFile = <userpath>/Documents/FreeCad/Fonts/Stencil_tenada/Tenada.ttf
  MakeFace = true
  MapMode = 5
  Placement = pos=(22,14.7,53) rot=(1,0,0;1.5708rad)
  Size = 2.5
  String = WiFi Smart Pump
  Support = -> [Pad137]
  Tracking = 0
FEATURE [PartDesign::Pocket] Pocket087
  BaseFeature = -> Pad137
  Direction = (0,1,-2e-16)
  Length = 0.7
  Length2 = 5
  Profile = -> ShapeString014
  ReferenceAxis = -> ShapeString014 [N_Axis]
  Refine = true
  Type = 0
FEATURE [Part::Part2DObjectPython] ShapeString015  # Draft 2D object (typed FeaturePython)
  AttachmentOffset = pos=(33,43,0) rot=(0,0,1;0rad)
  FontFile = <userpath>/Documents/FreeCad/Fonts/Stencil_tenada/Tenada.ttf
  MakeFace = true
  MapMode = 5
  Placement = pos=(33,14.7,43) rot=(1,0,0;1.5708rad)
  Size = 2.4
  String = Controller S1
  Support = -> [Pocket087]
  Tracking = 0
FEATURE [PartDesign::Pocket] Pocket088
  BaseFeature = -> Pocket087
  Direction = (0,1,-2e-16)
  Length = 0.7
  Length2 = 5
  Profile = -> ShapeString015
  ReferenceAxis = -> ShapeString015 [N_Axis]
  Refine = true
  Type = 0
FEATURE [PartDesign::Pad] Pad138
  BaseFeature = -> Pocket088
  Direction = (0,-1,0)
  Length = 1
  Length2 = 10
  Profile = -> Pocket088 [Face29]
  Refine = true
  Type = 0
FEATURE [Sketcher::SketchObject] Sketch111
  ExternalGeometry = -> [Pad138]
  FullyConstrained = false
  MapMode = 5
  Placement = pos=(0,1e-16,2) rot=(0,0,1;0rad)
  Support = -> [Pad138]
  sketch-geometry (4):
    g0: LineSegment StartX=93.9 StartY=48.3611 StartZ=0 EndX=81.2 EndY=48.3611 EndZ=0
    g1: LineSegment StartX=81.2 StartY=48.3611 StartZ=0 EndX=81.2 EndY=32.3611 EndZ=0
    g2: LineSegment StartX=81.2 StartY=32.3611 StartZ=0 EndX=93.9 EndY=32.3611 EndZ=0
    g3: LineSegment StartX=93.9 StartY=32.3611 StartZ=0 EndX=93.9 EndY=48.3611 EndZ=0
  constraints (11):
    c: Coincident(g0,g1)
    c: Coincident(g1,g2)
    c: Coincident(g2,g3)
    c: Coincident(g3,g0)
    c: Horizontal(g0)
    c: Horizontal(g2)
    c: Vertical(g1)
    c: Vertical(g3)
    c: PointOnObject(g0,g-3)
    c: DistanceY(g1,g1) = 16
    c: DistanceX(g0,g0) = 12.7
FEATURE [PartDesign::Pocket] Pocket092
  BaseFeature = -> Pad138
  Direction = (0,0,-1)
  Length = 122
  Length2 = 5
  Profile = -> Sketch111
  ReferenceAxis = -> Sketch111 [N_Axis]
  Refine = true
  Type = 0
FEATURE [PartDesign::Pocket] Pocket093
  BaseFeature = -> Pocket092
  Direction = (0,0,1)
  Length = 1
  Length2 = 5
  Profile = -> Pocket092 [Face46]
  Refine = true
  Type = 0
FEATURE [PartDesign::Pocket] Pocket094
  BaseFeature = -> Pocket093
  Direction = (0,0,-1)
  Length = 1
  Length2 = 5
  Profile = -> Pocket093 [Face45]
  Refine = true
  Type = 0
FEATURE [PartDesign::Pad] Pad140
  BaseFeature = -> Pocket094
  Direction = (1,0,0)
  Length = 2
  Length2 = 10
  Profile = -> Pocket094 [Face13]
  Refine = true
  Type = 0
FEATURE [PartDesign::Pad] Pad141
  BaseFeature = -> Pad140
  Direction = (0,-1,0)
  Length = 2.5
  Length2 = 10
  Profile = -> Pad140 [Face1]
  Refine = true
  Type = 0
FEATURE [PartDesign::Pad] Pad142
  BaseFeature = -> Pad141
  Direction = (0,1,0)
  Length = 3.5
  Length2 = 10
  Profile = -> Pad141 [Face19]
  Refine = true
  Type = 0
FEATURE [Sketcher::SketchObject] Sketch112
  ExternalGeometry = -> [Pad142]
  FullyConstrained = true
  MapMode = 5
  Placement = pos=(0,0,0) rot=(1,0,0;3.14159rad)
  Support = -> [Pad142]
  sketch-geometry (4):
    g0: LineSegment StartX=83.2 StartY=-33.8611 StartZ=0 EndX=81.7 EndY=-33.8611 EndZ=0
    g1: LineSegment StartX=81.7 StartY=-33.8611 StartZ=0 EndX=81.7 EndY=-47.8611 EndZ=0
    g2: LineSegment StartX=81.7 StartY=-47.8611 StartZ=0 EndX=83.2 EndY=-47.8611 EndZ=0
    g3: LineSegment StartX=83.2 StartY=-47.8611 StartZ=0 EndX=83.2 EndY=-33.8611 EndZ=0
  constraints (12):
    c: Coincident(g0,g1)
    c: Coincident(g1,g2)
    c: Coincident(g2,g3)
    c: Coincident(g3,g0)
    c: Horizontal(g0)
    c: Horizontal(g2)
    c: Vertical(g1)
    c: Vertical(g3)
    c: PointOnObject(g0,g-3)
    c: DistanceY(g-3,g0) = 2
    c: DistanceY(g2,g-3) = 2
    c: DistanceX(g0,g0) = 1.5
FEATURE [PartDesign::Pad] Pad143
  BaseFeature = -> Pad142
  Direction = (0,0,-1)
  Length = 38.4
  Length2 = 10
  Profile = -> Sketch112
  ReferenceAxis = -> Sketch112 [N_Axis]
  Refine = true
  Type = 0
FEATURE [Sketcher::SketchObject] Sketch113
  ExternalGeometry = -> [Pad143]
  FullyConstrained = true
  MapMode = 5
  Placement = pos=(83.2,0,3.24e-14) rot=(0.57735,0.57735,0.57735;2.0944rad)
  Support = -> [Pad143]
  sketch-geometry (8):
    g0: LineSegment StartX=47.8611 StartY=-3.55e-14 StartZ=0 EndX=45.8611 EndY=-3.55e-14 EndZ=0
    g1: LineSegment StartX=45.8611 StartY=-3.55e-14 StartZ=0 EndX=45.8611 EndY=-38.4 EndZ=0
    g2: LineSegment StartX=45.8611 StartY=-38.4 StartZ=0 EndX=47.8611 EndY=-38.4 EndZ=0
    g3: LineSegment StartX=47.8611 StartY=-38.4 StartZ=0 EndX=47.8611 EndY=-3.55e-14 EndZ=0
    g4: LineSegment StartX=33.8611 StartY=0 StartZ=0 EndX=35.8611 EndY=0 EndZ=0
    g5: LineSegment StartX=35.8611 StartY=0 StartZ=0 EndX=35.8611 EndY=-38.4 EndZ=0
    g6: LineSegment StartX=35.8611 StartY=-38.4 StartZ=0 EndX=33.8611 EndY=-38.4 EndZ=0
    g7: LineSegment StartX=33.8611 StartY=-38.4 StartZ=0 EndX=33.8611 EndY=0 EndZ=0
  constraints (23):
    c: Coincident(g0,g1)
    c: Coincident(g1,g2)
    c: Coincident(g2,g3)
    c: Coincident(g3,g0)
    c: Horizontal(g0)
    c: Horizontal(g2)
    c: Vertical(g1)
    c: Vertical(g3)
    c: Coincident(g0,g-4)
    c: PointOnObject(g1,g-5)
    c: DistanceX(g2,g2) = 2
    c: Coincident(g4,g5)
    c: Coincident(g5,g6)
    c: Coincident(g6,g7)
    c: Coincident(g7,g4)
    c: Horizontal(g4)
    c: Horizontal(g6)
    c: Vertical(g5)
    c: Vertical(g7)
    c: PointOnObject(g4,g-3)
    c: DistanceX(g4,g4) = 2
    c: PointOnObject(g5,g-5)
    c: PointOnObject(g4,g-1)
FEATURE [PartDesign::Pad] Pad144
  BaseFeature = -> Pad143
  Direction = (1,0,4e-16)
  Length = 9
  Length2 = 10
  Profile = -> Sketch113
  ReferenceAxis = -> Sketch113 [N_Axis]
  Refine = true
  Type = 0
FEATURE [Sketcher::SketchObject] Sketch114
  ExternalGeometry = -> [Pad144]
  FullyConstrained = true
  MapMode = 5
  Placement = pos=(83.2,0,3.24e-14) rot=(0.57735,0.57735,0.57735;2.0944rad)
  Support = -> [Pad144]
  sketch-geometry (4):
    g0: LineSegment StartX=35.8611 StartY=-33.4 StartZ=0 EndX=45.8611 EndY=-33.4 EndZ=0
    g1: LineSegment StartX=45.8611 StartY=-33.4 StartZ=0 EndX=45.8611 EndY=-36.4 EndZ=0
    g2: LineSegment StartX=45.8611 StartY=-36.4 StartZ=0 EndX=35.8611 EndY=-36.4 EndZ=0
    g3: LineSegment StartX=35.8611 StartY=-36.4 StartZ=0 EndX=35.8611 EndY=-33.4 EndZ=0
  constraints (12):
    c: Coincident(g0,g1)
    c: Coincident(g1,g2)
    c: Coincident(g2,g3)
    c: Coincident(g3,g0)
    c: Horizontal(g0)
    c: Horizontal(g2)
    c: Vertical(g1)
    c: Vertical(g3)
    c: DistanceY(g-3,g2) = 2
    c: DistanceY(g3,g3) = 3
    c: PointOnObject(g0,g-5)
    c: PointOnObject(g0,g-4)
FEATURE [PartDesign::Pad] Pad145
  BaseFeature = -> Pad144
  Direction = (1,0,4e-16)
  Length = 10.7
  Length2 = 10
  Profile = -> Sketch114
  ReferenceAxis = -> Sketch114 [N_Axis]
  Refine = true
  Type = 0
FEATURE [Sketcher::SketchObject] Sketch115
  ExternalGeometry = -> [Pad145]
  FullyConstrained = true
  MapMode = 5
  Placement = pos=(0,45.8611,0) rot=(1,0,0;1.5708rad)
  Support = -> [Pad145]
  sketch-geometry (4):
    g0: LineSegment StartX=91.9 StartY=-51.1 StartZ=0 EndX=93.9 EndY=-51.1 EndZ=0
    g1: LineSegment StartX=93.9 StartY=-51.1 StartZ=0 EndX=93.9 EndY=-36.4 EndZ=0
    g2: LineSegment StartX=93.9 StartY=-36.4 StartZ=0 EndX=91.9 EndY=-36.4 EndZ=0
    g3: LineSegment StartX=91.9 StartY=-36.4 StartZ=0 EndX=91.9 EndY=-51.1 EndZ=0
  constraints (11):
    c: Coincident(g0,g1)
    c: Coincident(g1,g2)
    c: Coincident(g2,g3)
    c: Coincident(g3,g0)
    c: Horizontal(g0)
    c: Horizontal(g2)
    c: Vertical(g1)
    c: Vertical(g3)
    c: Coincident(g0,g-3)
    c: PointOnObject(g0,g-5)
    c: PointOnObject(g1,g-4)
FEATURE [PartDesign::Pad] Pad146
  BaseFeature = -> Pad145
  Direction = (0,-1,2e-16)
  Length = 10
  Length2 = 10
  Profile = -> Sketch115
  ReferenceAxis = -> Sketch115 [N_Axis]
  Refine = true
  Type = 0
FEATURE [PartDesign::Fillet] Fillet009
  Base = -> Pad146 [Edge32,Edge28]
  BaseFeature = -> Pad146
  Radius = 2
  Refine = true
  SupportTransform = false
  UseAllEdges = false
FEATURE [PartDesign::Fillet] Fillet010
  Base = -> Fillet009 [Edge166,Edge164]
  BaseFeature = -> Fillet009
  Radius = 3
  Refine = true
  SupportTransform = false
  UseAllEdges = false
FEATURE [Sketcher::SketchObject] Sketch116
  ExternalGeometry = -> [Fillet010]
  FullyConstrained = true
  MapMode = 5
  Placement = pos=(1.6e-14,0,-36.4) rot=(1,0,0;3.14159rad)
  Support = -> [Fillet010]
  sketch-geometry (8):
    g0: LineSegment StartX=83.51 StartY=-36.0511 StartZ=0 EndX=86.81 EndY=-36.0511 EndZ=0
    g1: LineSegment StartX=86.81 StartY=-36.0511 StartZ=0 EndX=86.81 EndY=-38.0511 EndZ=0
    g2: LineSegment StartX=86.81 StartY=-38.0511 StartZ=0 EndX=83.51 EndY=-38.0511 EndZ=0
    g3: LineSegment StartX=83.51 StartY=-38.0511 StartZ=0 EndX=83.51 EndY=-36.0511 EndZ=0
    g4: LineSegment StartX=83.51 StartY=-45.4811 StartZ=0 EndX=86.81 EndY=-45.4811 EndZ=0
    g5: LineSegment StartX=86.81 StartY=-45.4811 StartZ=0 EndX=86.81 EndY=-43.4811 EndZ=0
    g6: LineSegment StartX=86.81 StartY=-43.4811 StartZ=0 EndX=83.51 EndY=-43.4811 EndZ=0
    g7: LineSegment StartX=83.51 StartY=-43.4811 StartZ=0 EndX=83.51 EndY=-45.4811 EndZ=0
  constraints (24):
    c: Coincident(g0,g1)
    c: Coincident(g1,g2)
    c: Coincident(g2,g3)
    c: Coincident(g3,g0)
    c: Horizontal(g0)
    c: Horizontal(g2)
    c: Vertical(g1)
    c: Vertical(g3)
    c: Coincident(g4,g5)
    c: Coincident(g5,g6)
    c: Coincident(g6,g7)
    c: Coincident(g7,g4)
    c: Horizontal(g4)
    c: Horizontal(g6)
    c: Vertical(g5)
    c: Vertical(g7)
    c: DistanceX(g0,g0) = 3.3
    c: DistanceY(g1,g1) = 2
    c: DistanceY(g5,g5) = 2
    c: DistanceX(g6,g6) = 3.3
    c: DistanceX(g-3,g2) = 0.31
    c: DistanceX(g-3,g4) = 0.31
    c: DistanceY(g2,g-3) = 2.19
    c: DistanceY(g-3,g6) = 2.38
FEATURE [PartDesign::Pocket] Pocket095
  BaseFeature = -> Fillet010
  Direction = (-4e-16,0,1)
  Length = 2.4
  Length2 = 5
  Profile = -> Sketch116
  ReferenceAxis = -> Sketch116 [N_Axis]
  Refine = true
  Type = 0
FEATURE [Sketcher::SketchObject] Sketch117
  ExternalGeometry = -> [Pocket095]
  FullyConstrained = true
  MapMode = 5
  Placement = pos=(1.6e-14,0,-36.4) rot=(1,0,0;3.14159rad)
  Support = -> [Pocket095]
  sketch-geometry (4):
    g0: LineSegment StartX=83.2 StartY=-39.8611 StartZ=0 EndX=91.9 EndY=-39.8611 EndZ=0
    g1: LineSegment StartX=91.9 StartY=-39.8611 StartZ=0 EndX=91.9 EndY=-41.8611 EndZ=0
    g2: LineSegment StartX=91.9 StartY=-41.8611 StartZ=0 EndX=83.2 EndY=-41.8611 EndZ=0
    g3: LineSegment StartX=83.2 StartY=-41.8611 StartZ=0 EndX=83.2 EndY=-39.8611 EndZ=0
  constraints (13):
    c: Coincident(g0,g1)
    c: Coincident(g1,g2)
    c: Coincident(g2,g3)
    c: Coincident(g3,g0)
    c: Horizontal(g0)
    c: Horizontal(g2)
    c: Vertical(g1)
    c: Vertical(g3)
    c: PointOnObject(g0,g-3)
    c: PointOnObject(g1,g-4)
    c: DistanceY(g3,g3) = 2
    c: DistanceY(g0,g-3) = 4
    c: DistanceY(g-3,g2) = 4
FEATURE [PartDesign::Pad] Pad147
  BaseFeature = -> Pocket095
  Direction = (4e-16,0,-1)
  Length = 2
  Length2 = 10
  Profile = -> Sketch117
  ReferenceAxis = -> Sketch117 [N_Axis]
  Refine = true
  Type = 0
FEATURE [PartDesign::Pad] Pad148
  BaseFeature = -> Pad147
  Direction = (0,-1,0)
  Length = 0.3
  Length2 = 10
  Profile = -> Pad147 [Face26]
  Refine = true
  Type = 0
FEATURE [PartDesign::Pad] Pad149
  BaseFeature = -> Pad148
  Direction = (0,0,-1)
  Length = 0.1
  Length2 = 10
  Profile = -> Pad148 [Face25]
  Refine = true
  Type = 0
FEATURE [Sketcher::SketchObject] Sketch118
  ExternalGeometry = -> [Pad149]
  FullyConstrained = true
  MapMode = 5
  Placement = pos=(-2e-16,16.7,-1e-15) rot=(0,0.707107,0.707107;3.14159rad)
  Support = -> [Pad149]
  sketch-geometry (4):
    g0: LineSegment StartX=-93.9 StartY=-28.8 StartZ=0 EndX=-92.2 EndY=-28.8 EndZ=0
    g1: LineSegment StartX=-92.2 StartY=-28.8 StartZ=0 EndX=-92.2 EndY=-39.8 EndZ=0
    g2: LineSegment StartX=-92.2 StartY=-39.8 StartZ=0 EndX=-93.9 EndY=-39.8 EndZ=0
    g3: LineSegment StartX=-93.9 StartY=-39.8 StartZ=0 EndX=-93.9 EndY=-28.8 EndZ=0
  constraints (11):
    c: Coincident(g0,g1)
    c: Coincident(g1,g2)
    c: Coincident(g2,g3)
    c: Coincident(g3,g0)
    c: Horizontal(g0)
    c: Horizontal(g2)
    c: Vertical(g1)
    c: Vertical(g3)
    c: Coincident(g0,g-3)
    c: DistanceY(g3,g3) = 11
    c: DistanceX(g0,g0) = 1.7
FEATURE [PartDesign::Pad] Pad150
  BaseFeature = -> Pad149
  Direction = (0,1,-2e-16)
  Length = 2
  Length2 = 10
  Profile = -> Sketch118
  ReferenceAxis = -> Sketch118 [N_Axis]
  Refine = true
  Type = 0
FEATURE [Part::Part2DObjectPython] ShapeString016  # Draft 2D object (typed FeaturePython)
  AttachmentOffset = pos=(-25,-17,0) rot=(0,0,1;3.14159rad)
  FontFile = <userpath>/Documents/FreeCad/Fonts/Stencil_tenada/Tenada.ttf
  MakeFace = true
  MapMode = 5
  Placement = pos=(25,101.15,-17) rot=(1,0,0;4.71239rad)
  Size = 3
  String = WaterLevel
  Support = -> [Pad150]
  Tracking = 0
FEATURE [PartDesign::Pad] Pad151
  BaseFeature = -> Pad150
  Direction = (0,1,-2e-16)
  Length = 1
  Length2 = 10
  Profile = -> ShapeString016
  ReferenceAxis = -> ShapeString016 [N_Axis]
  Refine = true
  Type = 0
FEATURE [Part::Part2DObjectPython] ShapeString017  # Draft 2D object (typed FeaturePython)
  AttachmentOffset = pos=(-43,-7,0) rot=(0,0,1;3.14159rad)
  FontFile = <userpath>/Documents/FreeCad/Fonts/Stencil_tenada/Tenada.ttf
  MakeFace = true
  MapMode = 5
  Placement = pos=(43,101.15,-7) rot=(1,0,0;4.71239rad)
  Size = 3
  String = .Pro
  Support = -> [Pad151]
  Tracking = 0
FEATURE [PartDesign::Pad] Pad152
  BaseFeature = -> Pad151
  Direction = (0,1,-2e-16)
  Length = 1
  Length2 = 10
  Profile = -> ShapeString017
  ReferenceAxis = -> ShapeString017 [N_Axis]
  Refine = true
  Type = 0
FEATURE [PartDesign::Pocket] Pocket096
  BaseFeature = -> Pad152
  Direction = (0,0,-1)
  Length = 0.7
  Length2 = 5
  Profile = -> ShapeString018
  ReferenceAxis = -> ShapeString018 [N_Axis]
  Refine = true
  Type = 0
FEATURE [PartDesign::Pocket] Pocket097
  BaseFeature = -> Pocket096
  Direction = (0,0,-1)
  Length = 0.7
  Length2 = 5
  Profile = -> ShapeString019
  ReferenceAxis = -> ShapeString019 [N_Axis]
  Refine = true
  Type = 0
FEATURE [PartDesign::Boolean] Boolean002
  BaseFeature = -> Pocket097
  Group = -> [Body006]
  Refine = true
  Type = 0
FEATURE [PartDesign::Pocket] Pocket098
  BaseFeature = -> Boolean002
  Direction = (0,-1,0)
  Length = 1.85
  Length2 = 5
  Profile = -> Boolean002 [Face74]
  Refine = true
  Type = 0
FEATURE [PartDesign::Pad] Pad153
  BaseFeature = -> Pocket098
  Direction = (0,0,-1)
  Length = 0.01
  Length2 = 10
  Profile = -> Pocket098 [Face40]
  Refine = true
  Type = 0
FEATURE [PartDesign::Pocket] Pocket099
  BaseFeature = -> Pad153
  Direction = (1,0,4e-16)
  Length = 4
  Length2 = 5
  Profile = -> Pad153 [Face65,Face62]
  Refine = true
  Type = 0
FEATURE [Sketcher::SketchObject] Sketch119
  ExternalGeometry = -> [Pocket099]
  FullyConstrained = true
  MapMode = 5
  Placement = pos=(0,0,0) rot=(1,0,0;3.14159rad)
  Support = -> [Pocket099]
  sketch-geometry (8):
    g0: LineSegment StartX=39.5 StartY=-65.35 StartZ=0 EndX=62.3 EndY=-65.35 EndZ=0
    g1: LineSegment StartX=62.3 StartY=-65.35 StartZ=0 EndX=62.3 EndY=-78.15 EndZ=0
    g2: LineSegment StartX=62.3 StartY=-78.15 StartZ=0 EndX=39.5 EndY=-78.15 EndZ=0
    g3: LineSegment StartX=39.5 StartY=-78.15 StartZ=0 EndX=39.5 EndY=-65.35 EndZ=0
    g4: LineSegment StartX=38.5 StartY=-64.35 StartZ=0 EndX=63.3 EndY=-64.35 EndZ=0
    g5: LineSegment StartX=63.3 StartY=-64.35 StartZ=0 EndX=63.3 EndY=-79.15 EndZ=0
    g6: LineSegment StartX=63.3 StartY=-79.15 StartZ=0 EndX=38.5 EndY=-79.15 EndZ=0
    g7: LineSegment StartX=38.5 StartY=-79.15 StartZ=0 EndX=38.5 EndY=-64.35 EndZ=0
  constraints (22):
    c: Coincident(g0,g1)
    c: Coincident(g1,g2)
    c: Coincident(g2,g3)
    c: Coincident(g3,g0)
    c: Horizontal(g0)
    c: Horizontal(g2)
    c: Vertical(g1)
    c: Vertical(g3)
    c: Coincident(g0,g-4)
    c: Coincident(g1,g-6)
    c: Coincident(g4,g5)
    c: Coincident(g5,g6)
    c: Coincident(g6,g7)
    c: Coincident(g7,g4)
    c: Horizontal(g4)
    c: Horizontal(g6)
    c: Vertical(g5)
    c: Vertical(g7)
    c: DistanceX(g0,g4) = 1
    c: DistanceX(g6,g2) = 1
    c: DistanceY(g0,g4) = 1
    c: DistanceY(g5,g1) = 1
FEATURE [PartDesign::Pad] Pad154
  BaseFeature = -> Pocket099
  Direction = (0,0,-1)
  Length = 1
  Length2 = 10
  Profile = -> Sketch119
  ReferenceAxis = -> Sketch119 [N_Axis]
  Refine = true
  Type = 0
FEATURE [PartDesign::Pad] Pad155
  BaseFeature = -> Pad154
  Direction = (0,0,-1)
  Length = 11.8
  Length2 = 10
  Profile = -> Pad154 [Face37]
  Refine = true
  Type = 0
FEATURE [PartDesign::Pad] Pad156
  BaseFeature = -> Pad155
  Direction = (0,-1,0)
  Length = 1
  Length2 = 10
  Profile = -> Pad155 [Face80]
  Refine = true
  Type = 0
FEATURE [Sketcher::SketchObject] Sketch120
  ExternalGeometry = -> [Pad156]
  FullyConstrained = true
  MapMode = 5
  Placement = pos=(93.9,9e-16,-5.6e-15) rot=(0.57735,0.57735,0.57735;2.0944rad)
  Support = -> [Pad156]
  sketch-geometry (1):
    g0: Circle CenterX=24.13 CenterY=-34.99 CenterZ=0 NormalX=0 NormalY=0 NormalZ=1 AngleXU=0 Radius=2.2
  constraints (3):
    c: Diameter(g0) = 4.4
    c: DistanceY(g-3,g0) = 5.61
    c: DistanceX(g0,g-3) = 5.97
FEATURE [PartDesign::Pocket] Pocket100
  BaseFeature = -> Pad156
  Direction = (-1,0,0)
  Length = 5
  Length2 = 5
  Profile = -> Sketch120
  ReferenceAxis = -> Sketch120 [N_Axis]
  Refine = true
  Type = 0
FEATURE [PartDesign::Pad] Pad157
  BaseFeature = -> Pocket100
  Direction = (0,0,1)
  Length = 1.7
  Length2 = 10
  Profile = -> Pocket100 [Face1089,Face1090,Face1091,Face1092,Face1093,Face1094,Face1095,Face1096,Face1105,Face1106,Face1107,Face1108,Face1110,Face1111,Face1109,Face1104,Face1103,Face1102,Face1099,Face1101,Face1100,Face1097,Face1098,Face1088,Face1087,Face1086,Face1085]
  Refine = true
  Type = 0
FEATURE [PartDesign::Pocket] Pocket101
  BaseFeature = -> Pad157
  Direction = (0,0,1)
  Length = 1
  Length2 = 5
  Profile = -> Pad157 [Face1129]
  Refine = true
  Type = 0
FEATURE [PartDesign::Pocket] Pocket102
  BaseFeature = -> Pocket101
  Direction = (0,0,1)
  Length = 1
  Length2 = 5
  Profile = -> Pocket101 [Face1110]
  Refine = true
  Type = 0
FEATURE [Sketcher::SketchObject] Sketch121
  ExternalGeometry = -> [Pocket102]
  FullyConstrained = true
  MapMode = 5
  Placement = pos=(0,0,-3) rot=(1,0,0;3.14159rad)
  Support = -> [Pocket102]
  sketch-geometry (4):
    g0: LineSegment StartX=35 StartY=-55.85 StartZ=0 EndX=66.8 EndY=-55.85 EndZ=0
    g1: LineSegment StartX=66.8 StartY=-55.85 StartZ=0 EndX=66.8 EndY=-84.65 EndZ=0
    g2: LineSegment StartX=66.8 StartY=-84.65 StartZ=0 EndX=35 EndY=-84.65 EndZ=0
    g3: LineSegment StartX=35 StartY=-84.65 StartZ=0 EndX=35 EndY=-55.85 EndZ=0
  constraints (12):
    c: Coincident(g0,g1)
    c: Coincident(g1,g2)
    c: Coincident(g2,g3)
    c: Coincident(g3,g0)
    c: Horizontal(g0)
    c: Horizontal(g2)
    c: Vertical(g1)
    c: Vertical(g3)
    c: PointOnObject(g0,g-4)
    c: PointOnObject(g1,g-5)
    c: PointOnObject(g-6,g0)
    c: PointOnObject(g-3,g2)
FEATURE [PartDesign::Pocket] Pocket103
  BaseFeature = -> Pocket102
  Direction = (0,0,1)
  Length = 2.99
  Length2 = 5
  Profile = -> Sketch121
  ReferenceAxis = -> Sketch121 [N_Axis]
  Refine = true
  Type = 0
FEATURE [Sketcher::SketchObject] Sketch122
  FullyConstrained = false
  MapMode = 5
  Placement = pos=(0,0,0) rot=(1,0,0;3.14159rad)
  Support = -> [Pocket103]
  sketch-geometry (4):
    g0: LineSegment StartX=-3.9777 StartY=-9.53597 StartZ=0 EndX=100.941 EndY=-9.53597 EndZ=0
    g1: LineSegment StartX=100.941 StartY=-9.53597 StartZ=0 EndX=100.941 EndY=-106.791 EndZ=0
    g2: LineSegment StartX=100.941 StartY=-106.791 StartZ=0 EndX=-3.9777 EndY=-106.791 EndZ=0
    g3: LineSegment StartX=-3.9777 StartY=-106.791 StartZ=0 EndX=-3.9777 EndY=-9.53597 EndZ=0
  constraints (8):
    c: Coincident(g0,g1)
    c: Coincident(g1,g2)
    c: Coincident(g2,g3)
    c: Coincident(g3,g0)
    c: Horizontal(g0)
    c: Horizontal(g2)
    c: Vertical(g1)
    c: Vertical(g3)
FEATURE [PartDesign::Pocket] Pocket104
  BaseFeature = -> Pocket103
  Direction = (0,0,1)
  Length = 500
  Length2 = 5
  Profile = -> Sketch122
  ReferenceAxis = -> Sketch122 [N_Axis]
  Refine = true
  Reversed = true
  Type = 0
FEATURE [PartDesign::Draft] Draft005
  Angle = 45
  Base = -> Pocket104 [Face13,Face19,Face11,Face16]
  BaseFeature = -> Pocket104
  NeutralPlane = -> Pocket104 [Face27]
  PullDirection = -> Pocket104 [Edge40]
  Refine = true
  Reversed = true
  SupportTransform = false
FEATURE [PartDesign::Draft] Draft004
  Angle = 45
  Base = -> Draft005 [Face26,Face24,Face12,Face18]
  BaseFeature = -> Draft005
  NeutralPlane = -> Draft005 [Face27]
  Refine = true
  Reversed = true
  SupportTransform = false
FEATURE [PartDesign::Draft] Draft006
  Angle = 45
  Base = -> Draft004 [Face20,Face22,Face14]
  BaseFeature = -> Draft004
  NeutralPlane = -> Draft004 [Face27]
  Refine = true
  Reversed = true
  SupportTransform = false
FEATURE [PartDesign::Draft] Draft007
  Angle = 45
  Base = -> Draft006 [Face25,Face23,Face21]
  BaseFeature = -> Draft006
  NeutralPlane = -> Draft006 [Face27]
  Refine = true
  Reversed = true
  SupportTransform = false
FEATURE [PartDesign::Pad] Pad158
  BaseFeature = -> Draft007
  Direction = (0,0,-1)
  Length = 1
  Length2 = 10
  Profile = -> Draft007 [Face5]
  Refine = true
  Type = 0
FEATURE [PartDesign::Pad] Pad159
  BaseFeature = -> Pad158
  Direction = (0,0,-1)
  Length = 1
  Length2 = 10
  Profile = -> Pad158 [Face784]
  Refine = true
  Type = 0
FEATURE [PartDesign::Chamfer] Chamfer007
  Angle = 45
  Base = -> Pad159 [Edge695,Edge693,Edge694,Edge696]
  BaseFeature = -> Pad159
  ChamferType = 0
  FlipDirection = false
  Refine = true
  Size = 2.7
  Size2 = 1
  SupportTransform = false
  UseAllEdges = false
FEATURE [PartDesign::Pocket] Pocket105
  BaseFeature = -> Pad113
  Direction = (0,0,-1)
  Length = 2
  Length2 = 5
  Profile = -> Pad113 [Face365]
  Refine = true
  Type = 0
FEATURE [PartDesign::Pad] Pad160
  BaseFeature = -> Pocket105
  Direction = (-1,0,0)
  Length = 0.5
  Length2 = 10
  Profile = -> Pocket105 [Face381]
  Refine = true
  Type = 0
FEATURE [Sketcher::SketchObject] Sketch123
  ExternalGeometry = -> [Pad160]
  FullyConstrained = false
  MapMode = 5
  Placement = pos=(0,0,0.56) rot=(0,0,1;0rad)
  Support = -> [Pad160]
  sketch-geometry (4):
    g0: LineSegment StartX=78.9 StartY=99.61 StartZ=0 EndX=79.4 EndY=99.61 EndZ=0
    g1: LineSegment StartX=79.4 StartY=99.61 StartZ=0 EndX=79.4 EndY=64.1567 EndZ=0
    g2: LineSegment StartX=79.4 StartY=64.1567 StartZ=0 EndX=78.9 EndY=64.1567 EndZ=0
    g3: LineSegment StartX=78.9 StartY=64.1567 StartZ=0 EndX=78.9 EndY=99.61 EndZ=0
  constraints (10):
    c: Coincident(g0,g1)
    c: Coincident(g1,g2)
    c: Coincident(g2,g3)
    c: Coincident(g3,g0)
    c: Horizontal(g0)
    c: Horizontal(g2)
    c: Vertical(g1)
    c: Vertical(g3)
    c: Coincident(g0,g-4)
    c: PointOnObject(g1,g-5)
FEATURE [PartDesign::Pocket] Pocket106
  BaseFeature = -> Pad160
  Direction = (0,0,-1)
  Length = 2.5
  Length2 = 5
  Profile = -> Sketch123
  ReferenceAxis = -> Sketch123 [N_Axis]
  Refine = true
  Type = 0
FEATURE [PartDesign::Body] Body001  label="LidB"
  Group = -> [Sketch008,Pad014,Sketch012,Pad017,Pad018,Pad019,Sketch013,Pad022,Sketch014,Pad023,Pocket002,Pad024,Pad025,Sketch015,Pad026,Sketch016,Pad027,Sketch017,Pad028,Pocket003,Sketch018,Pad029,Sketch019,Pad030,Sketch020,Pad031,Pad032,Pocket004,Pocket005,Pad033,Sketch021,Pocket006,Sketch023,Pocket008,Pocket010,Pocket011,Sketch025,Pocket012,Sketch026,Pad035,Sketch027,Pocket013,Sketch028,Pocket014,Sketch029,+79 more]
  Origin = -> Origin050
  Tip = -> Pocket106
FEATURE [Part::Cut] Cut  label="LidBottom"
  Base = -> Body001
  Refine = true
  Tool = -> Body003
FEATURE [PartDesign::Pad] Pad161
  BaseFeature = -> Chamfer007
  Direction = (0,0,-1)
  Length = 0.3
  Length2 = 10
  Profile = -> Chamfer007 [Face745]
  Refine = true
  Type = 0
FEATURE [PartDesign::Body] Body005  label="LidTop"
  Group = -> [Sketch089,Pad114,Sketch093,Pad117,Pad118,Pad119,Sketch094,Pad122,Sketch095,Pad123,Pocket075,Pad124,Pad125,Sketch096,Pad126,Sketch097,Pad127,Sketch098,Pad128,Pocket076,Sketch099,Pad129,Sketch100,Pad130,Sketch101,Pad131,Pad132,Pocket077,Pocket078,Pad133,Sketch102,Pocket079,Sketch103,Pocket080,Pocket081,Pocket082,Sketch104,Pocket083,Sketch105,Pad134,Sketch106,Pocket084,Sketch107,Pocket085,Sketch108,+69 more]
  Origin = -> Origin122
  Placement = pos=(0,0,0.29) rot=(0,0,1;0rad)
  Tip = -> Pad161
